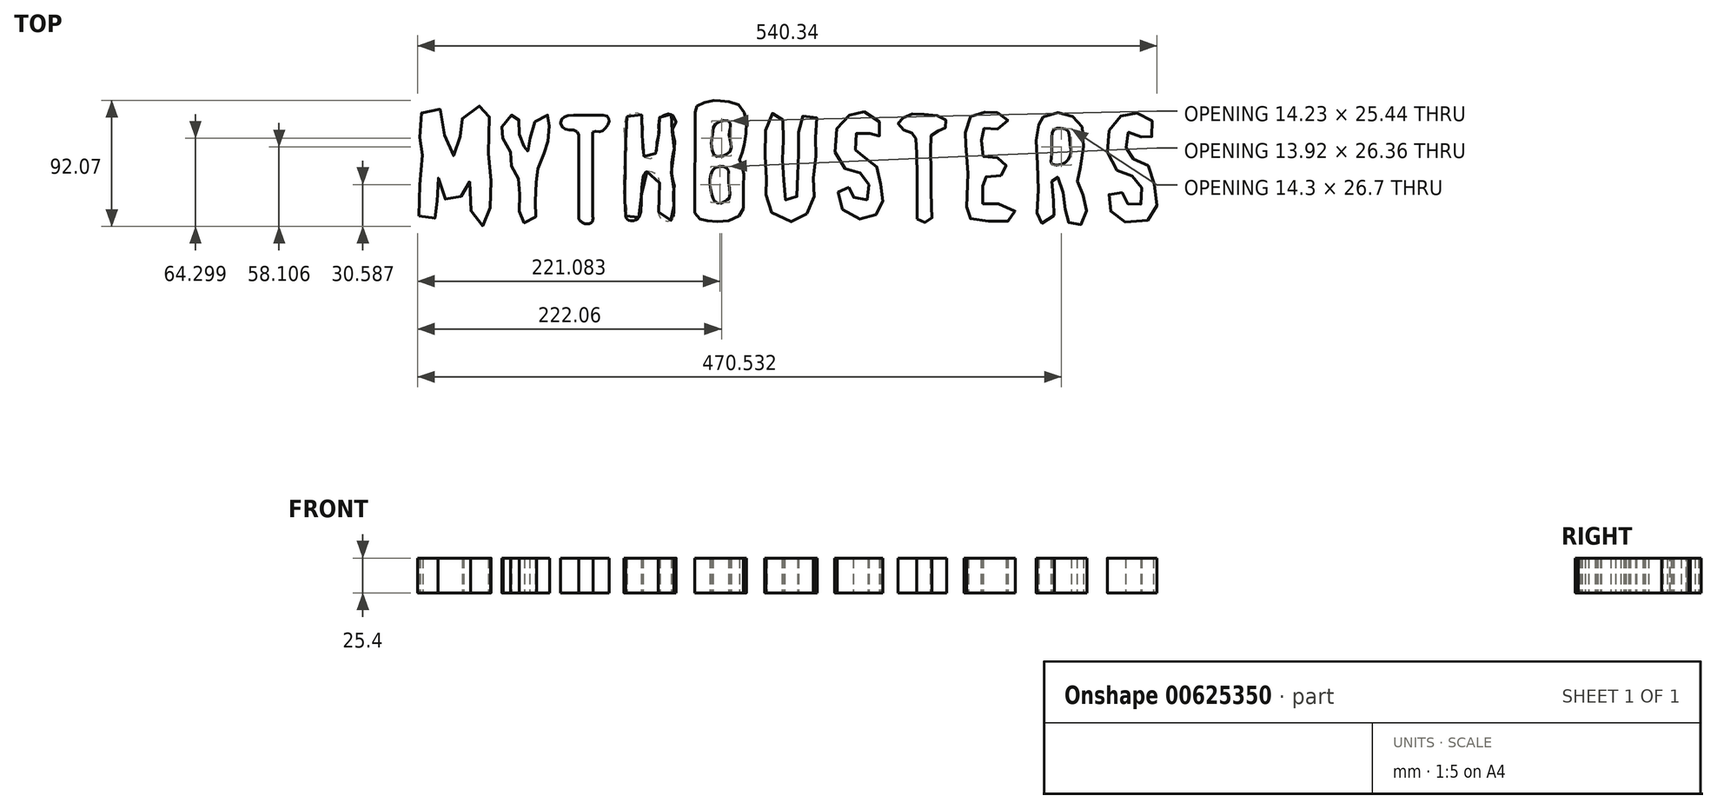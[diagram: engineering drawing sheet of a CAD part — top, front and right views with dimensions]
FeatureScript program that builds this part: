
annotation { "Feature Type Name" : "Feature", "Feature Type Description" : "" }
export const myFeature = defineFeature(function(context is Context, id is Id, definition is map)
    precondition{}
    {
        {
            var Q0;
            Q0=qCreatedBy(makeId("Top.planeOp"),FACE);
            var sketch = newSketch(context, id + "F0", { "sketchPlane" : qUnion([Q0])});
            skLineSegment(sketch, "E0", {"start": v(761.55, 2.5) * mm, "end": v(761.54, 2.5) * mm});
            skLineSegment(sketch, "E1", {"start": v(1000.17, -167.15) * mm, "end": v(1000.17, -167.15) * mm});
            skLineSegment(sketch, "E2", {"start": v(-212, -166.06) * mm, "end": v(-212, -166.06) * mm});
            skLineSegment(sketch, "E3", {"start": v(376.94, -160.6) * mm, "end": v(376.95, -160.6) * mm});
            skLineSegment(sketch, "E4", {"start": v(-451.88, -160.28) * mm, "end": v(-451.87, -160.28) * mm});
            skLineSegment(sketch, "E5", {"start": v(-22.25, -160.22) * mm, "end": v(-22.27, -160.22) * mm});
            skLineSegment(sketch, "E6", {"start": v(526.87, -156.12) * mm, "end": v(526.87, -156.12) * mm});
            skLineSegment(sketch, "E7", {"start": v(199.4, -158.96) * mm, "end": v(199.41, -158.96) * mm});
            skFitSpline(sketch, "E8", {"points": [v(827.87, -177.74) * mm, v(826.62, -176.42) * mm, v(824.58, -175.4) * mm, v(823.21, -175.4) * mm]});
            skFitSpline(sketch, "E9", {"points": [v(823.21, -175.4) * mm, v(821.38, -175.4) * mm, v(818.7, -173.24) * mm, v(812.38, -166.66) * mm]});
            skFitSpline(sketch, "E10", {"points": [v(812.38, -166.66) * mm, v(803.98, -157.92) * mm, v(803.98, -157.92) * mm, v(804.24, -147.06) * mm]});
            skFitSpline(sketch, "E11", {"points": [v(804.24, -147.06) * mm, v(804.47, -137.46) * mm, v(804.26, -135.72) * mm, v(802.42, -132.01) * mm]});
            skFitSpline(sketch, "E12", {"points": [v(802.42, -132.01) * mm, v(800.86, -128.86) * mm, v(800.35, -126.13) * mm, v(800.35, -121.02) * mm]});
            skFitSpline(sketch, "E13", {"points": [v(800.35, -121.02) * mm, v(800.35, -114.24) * mm, v(799.45, -111) * mm, v(796.32, -106.38) * mm]});
            skFitSpline(sketch, "E14", {"points": [v(796.32, -106.38) * mm, v(794.93, -104.33) * mm, v(794.84, -103.44) * mm, v(795.75, -100.82) * mm]});
            skFitSpline(sketch, "E15", {"points": [v(795.75, -100.82) * mm, v(796.71, -98.07) * mm, v(796.61, -97.52) * mm, v(794.93, -96.18) * mm]});
            skFitSpline(sketch, "E16", {"points": [v(794.93, -96.18) * mm, v(792.74, -94.43) * mm, v(791.1, -84.36) * mm, v(792.83, -83.3) * mm]});
            skFitSpline(sketch, "E17", {"points": [v(792.83, -83.3) * mm, v(793.5, -82.88) * mm, v(793.42, -82.2) * mm, v(792.6, -81.2) * mm]});
            skFitSpline(sketch, "E18", {"points": [v(792.6, -81.2) * mm, v(791.79, -80.22) * mm, v(791.36, -76.66) * mm, v(791.34, -70.66) * mm]});
            skFitSpline(sketch, "E19", {"points": [v(791.34, -70.66) * mm, v(791.32, -62.64) * mm, v(791.06, -61.25) * mm, v(789.09, -58.59) * mm]});
            skFitSpline(sketch, "E20", {"points": [v(789.09, -58.59) * mm, v(787.36, -56.25) * mm, v(786.98, -54.83) * mm, v(787.4, -52.24) * mm]});
            skFitSpline(sketch, "E21", {"points": [v(787.4, -52.24) * mm, v(787.91, -49.08) * mm, v(787.53, -48.46) * mm, v(780.65, -41.32) * mm]});
            skFitSpline(sketch, "E22", {"points": [v(780.65, -41.32) * mm, v(772.46, -32.82) * mm, v(772.52, -32.85) * mm, v(769.96, -36.1) * mm]});
            skFitSpline(sketch, "E23", {"points": [v(769.96, -36.1) * mm, v(768.72, -37.67) * mm, v(767.16, -38.46) * mm, v(765.3, -38.46) * mm]});
            skFitSpline(sketch, "E24", {"points": [v(765.3, -38.46) * mm, v(762.5, -38.46) * mm, v(762.5, -38.46) * mm, v(763.12, -45.42) * mm]});
            skFitSpline(sketch, "E25", {"points": [v(763.12, -45.42) * mm, v(763.56, -50.23) * mm, v(763.42, -52.58) * mm, v(762.67, -53.04) * mm]});
            skFitSpline(sketch, "E26", {"points": [v(762.67, -53.04) * mm, v(762.08, -53.4) * mm, v(761.86, -54.13) * mm, v(762.18, -54.64) * mm]});
            skFitSpline(sketch, "E27", {"points": [v(762.18, -54.64) * mm, v(763.28, -56.42) * mm, v(763.7, -92.06) * mm, v(762.63, -92.73) * mm]});
            skFitSpline(sketch, "E28", {"points": [v(762.63, -92.73) * mm, v(761.23, -93.6) * mm, v(761.37, -99.6) * mm, v(762.8, -100.09) * mm]});
            skFitSpline(sketch, "E29", {"points": [v(762.8, -100.09) * mm, v(763.73, -100.4) * mm, v(763.7, -100.82) * mm, v(762.7, -102.04) * mm]});
            skFitSpline(sketch, "E30", {"points": [v(762.7, -102.04) * mm, v(761, -104.1) * mm, v(761.91, -106.23) * mm, v(764.64, -106.62) * mm]});
            skFitSpline(sketch, "E31", {"points": [v(764.64, -106.62) * mm, v(766.75, -106.92) * mm, v(766.83, -107.25) * mm, v(767.02, -117.32) * mm]});
            skFitSpline(sketch, "E32", {"points": [v(767.02, -117.32) * mm, v(767.5, -143.53) * mm, v(767.34, -146.47) * mm, v(765.28, -148.22) * mm]});
            skFitSpline(sketch, "E33", {"points": [v(765.28, -148.22) * mm, v(764.22, -149.12) * mm, v(763.23, -150.95) * mm, v(763.09, -152.28) * mm]});
            skFitSpline(sketch, "E34", {"points": [v(763.09, -152.28) * mm, v(762.94, -153.61) * mm, v(761.92, -155.67) * mm, v(760.8, -156.85) * mm]});
            skFitSpline(sketch, "E35", {"points": [v(760.8, -156.85) * mm, v(759.7, -158.03) * mm, v(758.8, -159.92) * mm, v(758.8, -161.05) * mm]});
            skFitSpline(sketch, "E36", {"points": [v(758.8, -161.05) * mm, v(758.8, -162.22) * mm, v(757.07, -164.84) * mm, v(754.83, -167.08) * mm]});
            skFitSpline(sketch, "E37", {"points": [v(754.83, -167.08) * mm, v(750.86, -171.05) * mm, v(750.86, -171.05) * mm, v(739.06, -170.78) * mm]});
            skFitSpline(sketch, "E38", {"points": [v(739.06, -170.78) * mm, v(725.94, -170.49) * mm, v(724.88, -170) * mm, v(724.83, -164.25) * mm]});
            skFitSpline(sketch, "E39", {"points": [v(722.48, -159) * mm, v(720.17, -156.85) * mm, v(720.17, -156.85) * mm, v(720.1, -124.77) * mm]});
            skFitSpline(sketch, "E40", {"points": [v(720.1, -124.77) * mm, v(720.06, -102.89) * mm, v(720.37, -91.7) * mm, v(721.12, -89.58) * mm]});
            skFitSpline(sketch, "E41", {"points": [v(721.12, -89.58) * mm, v(721.96, -87.17) * mm, v(721.93, -85.97) * mm, v(721, -84.23) * mm]});
            skFitSpline(sketch, "E42", {"points": [v(721, -84.23) * mm, v(720.13, -82.6) * mm, v(719.99, -79.7) * mm, v(720.47, -73.68) * mm]});
            skFitSpline(sketch, "E43", {"points": [v(720.47, -73.68) * mm, v(720.83, -69.11) * mm, v(721.07, -64.63) * mm, v(720.99, -63.72) * mm]});
            skFitSpline(sketch, "E44", {"points": [v(720.99, -63.72) * mm, v(720.79, -61.46) * mm, v(720.59, -47.14) * mm, v(720.7, -43.66) * mm]});
            skFitSpline(sketch, "E45", {"points": [v(720.7, -43.66) * mm, v(720.75, -42.1) * mm, v(720.64, -26.59) * mm, v(720.44, -9.19) * mm]});
            skFitSpline(sketch, "E46", {"points": [v(720.44, -9.19) * mm, v(720.2, 12.32) * mm, v(720.42, 23.73) * mm, v(721.14, 26.46) * mm]});
            skFitSpline(sketch, "E47", {"points": [v(721.14, 26.46) * mm, v(721.86, 29.17) * mm, v(721.9, 30.85) * mm, v(721.25, 31.65) * mm]});
            skFitSpline(sketch, "E48", {"points": [v(721.25, 31.65) * mm, v(719.99, 33.22) * mm, v(719.67, 63.32) * mm, v(720.9, 64.8) * mm]});
            skFitSpline(sketch, "E49", {"points": [v(720.9, 64.8) * mm, v(721.5, 65.54) * mm, v(721.5, 67.46) * mm, v(720.87, 70.4) * mm]});
            skFitSpline(sketch, "E50", {"points": [v(720.87, 70.4) * mm, v(720.35, 72.87) * mm, v(720.16, 77.75) * mm, v(720.46, 81.25) * mm]});
            skFitSpline(sketch, "E51", {"points": [v(720.46, 81.25) * mm, v(721.35, 91.73) * mm, v(721.53, 98.62) * mm, v(720.92, 99) * mm]});
            skFitSpline(sketch, "E52", {"points": [v(720.92, 99) * mm, v(719.9, 99.64) * mm, v(719.98, 111.86) * mm, v(721.02, 113.11) * mm]});
            skFitSpline(sketch, "E53", {"points": [v(721.02, 113.11) * mm, v(721.75, 113.99) * mm, v(721.73, 115.57) * mm, v(720.96, 118.67) * mm]});
            skFitSpline(sketch, "E54", {"points": [v(720.96, 118.67) * mm, v(718.65, 127.82) * mm, v(722.57, 135.65) * mm, v(728.65, 134.06) * mm]});
            skFitSpline(sketch, "E55", {"points": [v(728.65, 134.06) * mm, v(729.6, 133.82) * mm, v(731.76, 134.63) * mm, v(733.44, 135.87) * mm]});
            skFitSpline(sketch, "E56", {"points": [v(733.44, 135.87) * mm, v(735.13, 137.12) * mm, v(737.68, 138.13) * mm, v(739.12, 138.13) * mm]});
            skFitSpline(sketch, "E57", {"points": [v(739.12, 138.13) * mm, v(740.74, 138.13) * mm, v(742.11, 138.83) * mm, v(742.72, 139.96) * mm]});
            skFitSpline(sketch, "E58", {"points": [v(742.72, 139.96) * mm, v(743.97, 142.3) * mm, v(746.9, 143.22) * mm, v(749.2, 142) * mm]});
            skFitSpline(sketch, "E59", {"points": [v(749.2, 142) * mm, v(750.57, 141.26) * mm, v(751.97, 141.49) * mm, v(754.86, 142.88) * mm]});
            skFitSpline(sketch, "E60", {"points": [v(754.86, 142.88) * mm, v(756.98, 143.9) * mm, v(759.1, 144.74) * mm, v(759.59, 144.74) * mm]});
            skFitSpline(sketch, "E61", {"points": [v(759.59, 144.74) * mm, v(760.07, 144.74) * mm, v(761, 145.38) * mm, v(761.64, 146.16) * mm]});
            skFitSpline(sketch, "E62", {"points": [v(761.64, 146.16) * mm, v(763.89, 148.87) * mm, v(776, 148.08) * mm, v(779.68, 145) * mm]});
            skFitSpline(sketch, "E63", {"points": [v(779.68, 145) * mm, v(782.74, 142.4) * mm, v(782.76, 142.4) * mm, v(795.72, 142.72) * mm]});
            skFitSpline(sketch, "E64", {"points": [v(795.72, 142.72) * mm, v(808.7, 143.04) * mm, v(808.7, 143.04) * mm, v(810.3, 140.59) * mm]});
            skFitSpline(sketch, "E65", {"points": [v(810.3, 140.59) * mm, v(811.79, 138.31) * mm, v(812.42, 138.13) * mm, v(818.86, 138.13) * mm]});
            skFitSpline(sketch, "E66", {"points": [v(818.86, 138.13) * mm, v(825.8, 138.13) * mm, v(825.8, 138.13) * mm, v(833.47, 130.34) * mm]});
            skFitSpline(sketch, "E67", {"points": [v(833.47, 130.34) * mm, v(841.9, 121.76) * mm, v(842.82, 120.2) * mm, v(842.15, 115.72) * mm]});
            skFitSpline(sketch, "E68", {"points": [v(842.15, 115.72) * mm, v(841.76, 113.07) * mm, v(842.1, 112.44) * mm, v(844.63, 111) * mm]});
            skFitSpline(sketch, "E69", {"points": [v(844.63, 111) * mm, v(847.48, 109.38) * mm, v(848.37, 107.57) * mm, v(846.8, 106.6) * mm]});
            skFitSpline(sketch, "E70", {"points": [v(846.8, 106.6) * mm, v(845.39, 105.73) * mm, v(847.8, 93.37) * mm, v(849.64, 92.04) * mm]});
            skFitSpline(sketch, "E71", {"points": [v(849.64, 92.04) * mm, v(851.69, 90.57) * mm, v(851.98, 83.8) * mm, v(850.2, 78.9) * mm]});
            skFitSpline(sketch, "E72", {"points": [v(850.2, 78.9) * mm, v(849.3, 76.41) * mm, v(849.3, 75.33) * mm, v(850.2, 73.9) * mm]});
            skFitSpline(sketch, "E73", {"points": [v(850.2, 73.9) * mm, v(851.67, 71.54) * mm, v(851.68, 65.04) * mm, v(850.21, 60.99) * mm]});
            skFitSpline(sketch, "E74", {"points": [v(850.21, 60.99) * mm, v(849.32, 58.52) * mm, v(849.33, 56.9) * mm, v(850.23, 53.5) * mm]});
            skFitSpline(sketch, "E75", {"points": [v(850.23, 53.5) * mm, v(851.11, 50.2) * mm, v(851.13, 48.83) * mm, v(850.3, 47.83) * mm]});
            skFitSpline(sketch, "E76", {"points": [v(850.3, 47.83) * mm, v(849.48, 46.84) * mm, v(849.47, 45.52) * mm, v(850.28, 42.5) * mm]});
            skFitSpline(sketch, "E77", {"points": [v(850.28, 42.5) * mm, v(850.99, 39.89) * mm, v(851.27, 30.32) * mm, v(851.11, 14.85) * mm]});
            skFitSpline(sketch, "E78", {"points": [v(851.11, 14.85) * mm, v(850.87, -8.8) * mm, v(850.87, -8.8) * mm, v(846.38, -13.16) * mm]});
            skFitSpline(sketch, "E79", {"points": [v(846.38, -13.16) * mm, v(843.38, -16.08) * mm, v(841.9, -18.3) * mm, v(841.9, -19.89) * mm]});
            skFitSpline(sketch, "E80", {"points": [v(841.9, -19.89) * mm, v(841.9, -21.41) * mm, v(840.46, -23.7) * mm, v(837.88, -26.31) * mm]});
            skFitSpline(sketch, "E81", {"points": [v(837.88, -26.31) * mm, v(833.87, -30.37) * mm, v(833.87, -30.37) * mm, v(833.7, -38.9) * mm]});
            skFitSpline(sketch, "E82", {"points": [v(833.7, -38.9) * mm, v(833.62, -43.6) * mm, v(833.24, -48.78) * mm, v(832.9, -50.43) * mm]});
            skFitSpline(sketch, "E83", {"points": [v(832.9, -50.43) * mm, v(832.3, -53.2) * mm, v(832.46, -53.45) * mm, v(834.95, -53.74) * mm]});
            skFitSpline(sketch, "E84", {"points": [v(834.95, -53.74) * mm, v(837.5, -54.03) * mm, v(837.66, -54.32) * mm, v(837.94, -59.17) * mm]});
            skFitSpline(sketch, "E85", {"points": [v(837.94, -59.17) * mm, v(838.15, -62.94) * mm, v(838.84, -65.02) * mm, v(840.53, -67.03) * mm]});
            skFitSpline(sketch, "E86", {"points": [v(840.53, -67.03) * mm, v(843.33, -70.36) * mm, v(843.43, -71.54) * mm, v(840.95, -72.19) * mm]});
            skFitSpline(sketch, "E87", {"points": [v(840.95, -72.19) * mm, v(838.02, -72.95) * mm, v(838.69, -74.96) * mm, v(843.35, -79.44) * mm]});
            skFitSpline(sketch, "E88", {"points": [v(843.35, -79.44) * mm, v(847.65, -83.55) * mm, v(847.65, -83.55) * mm, v(847.41, -90.27) * mm]});
            skFitSpline(sketch, "E89", {"points": [v(847.41, -90.27) * mm, v(847.21, -96.15) * mm, v(847.44, -97.24) * mm, v(849.26, -98.93) * mm]});
            skFitSpline(sketch, "E90", {"points": [v(849.26, -98.93) * mm, v(851.84, -101.33) * mm, v(852.33, -110.86) * mm, v(849.92, -111.78) * mm]});
            skFitSpline(sketch, "E91", {"points": [v(849.92, -111.78) * mm, v(847.52, -112.7) * mm, v(848.35, -115.82) * mm, v(851.81, -118.86) * mm]});
            skFitSpline(sketch, "E92", {"points": [v(851.81, -118.86) * mm, v(855.15, -121.8) * mm, v(855.93, -124.15) * mm, v(854.14, -125.94) * mm]});
            skFitSpline(sketch, "E93", {"points": [v(854.14, -125.94) * mm, v(853.07, -127.01) * mm, v(853.87, -130.07) * mm, v(855.22, -130.07) * mm]});
            skFitSpline(sketch, "E94", {"points": [v(855.22, -130.07) * mm, v(855.68, -130.07) * mm, v(856.06, -130.5) * mm, v(856.06, -131) * mm]});
            skFitSpline(sketch, "E95", {"points": [v(856.06, -131) * mm, v(856.06, -131.53) * mm, v(856.93, -132.82) * mm, v(857.98, -133.87) * mm]});
            skFitSpline(sketch, "E96", {"points": [v(857.98, -133.87) * mm, v(859.73, -135.63) * mm, v(859.89, -136.87) * mm, v(859.75, -147.98) * mm]});
            skFitSpline(sketch, "E97", {"points": [v(859.75, -147.98) * mm, v(859.6, -160.08) * mm, v(859.57, -160.19) * mm, v(856.88, -162.76) * mm]});
            skFitSpline(sketch, "E98", {"points": [v(856.88, -162.76) * mm, v(855.4, -164.2) * mm, v(854.17, -166.13) * mm, v(854.17, -167.07) * mm]});
            skFitSpline(sketch, "E99", {"points": [v(854.17, -167.07) * mm, v(854.17, -168.21) * mm, v(853.46, -168.79) * mm, v(852.05, -168.8) * mm]});
            skFitSpline(sketch, "E100", {"points": [v(852.05, -168.8) * mm, v(849.52, -168.82) * mm, v(848.4, -169.55) * mm, v(846.99, -172.09) * mm]});
            skFitSpline(sketch, "E101", {"points": [v(846.99, -172.09) * mm, v(846.41, -173.13) * mm, v(844.43, -174.4) * mm, v(842.58, -174.92) * mm]});
            skFitSpline(sketch, "E102", {"points": [v(842.58, -174.92) * mm, v(840.73, -175.44) * mm, v(838.2, -176.82) * mm, v(836.95, -178) * mm]});
            skFitSpline(sketch, "E103", {"points": [v(836.95, -178) * mm, v(834.01, -180.76) * mm, v(830.64, -180.66) * mm, v(827.87, -177.74) * mm]});
            skFitSpline(sketch, "E104", {"points": [v(761.54, 2.5) * mm, v(759.69, 3.43) * mm, v(759.32, 4.25) * mm, v(759.56, 6.9) * mm]});
            skFitSpline(sketch, "E105", {"points": [v(759.56, 6.9) * mm, v(760.68, 19.3) * mm, v(760.88, 24.3) * mm, v(760.86, 39.2) * mm]});
            skFitSpline(sketch, "E106", {"points": [v(760.86, 39.2) * mm, v(760.85, 49.16) * mm, v(761.21, 56.19) * mm, v(761.76, 56.53) * mm]});
            skFitSpline(sketch, "E107", {"points": [v(761.76, 56.53) * mm, v(762.92, 57.24) * mm, v(764.85, 61.79) * mm, v(764.53, 63.06) * mm]});
            skFitSpline(sketch, "E108", {"points": [v(764.53, 63.06) * mm, v(764.4, 63.58) * mm, v(764.3, 70.7) * mm, v(764.31, 78.88) * mm]});
            skFitSpline(sketch, "E109", {"points": [v(764.31, 78.88) * mm, v(764.33, 93.76) * mm, v(764.33, 93.76) * mm, v(768.14, 97.77) * mm]});
            skFitSpline(sketch, "E110", {"points": [v(768.14, 97.77) * mm, v(771.96, 101.77) * mm, v(771.96, 101.77) * mm, v(785.91, 101.77) * mm]});
            skFitSpline(sketch, "E111", {"points": [v(785.91, 101.77) * mm, v(799.87, 101.77) * mm, v(799.87, 101.77) * mm, v(805.07, 96.84) * mm]});
            skFitSpline(sketch, "E112", {"points": [v(805.07, 96.84) * mm, v(807.92, 94.12) * mm, v(810.58, 91.89) * mm, v(810.97, 91.88) * mm]});
            skFitSpline(sketch, "E113", {"points": [v(810.97, 91.88) * mm, v(812.3, 91.84) * mm, v(811.68, 88.29) * mm, v(810.26, 87.74) * mm]});
            skFitSpline(sketch, "E114", {"points": [v(810.26, 87.74) * mm, v(808.25, 86.97) * mm, v(808.5, 84.07) * mm, v(810.76, 82.14) * mm]});
            skFitSpline(sketch, "E115", {"points": [v(810.76, 82.14) * mm, v(812.4, 80.74) * mm, v(812.6, 79.8) * mm, v(812.06, 75.84) * mm]});
            skFitSpline(sketch, "E116", {"points": [v(812.06, 75.84) * mm, v(811.47, 71.38) * mm, v(811.55, 71.15) * mm, v(813.92, 70.56) * mm]});
            skFitSpline(sketch, "E117", {"points": [v(813.92, 70.56) * mm, v(816.27, 69.97) * mm, v(816.4, 69.62) * mm, v(816.4, 63.94) * mm]});
            skFitSpline(sketch, "E118", {"points": [v(816.4, 63.94) * mm, v(816.4, 59.42) * mm, v(816.03, 57.75) * mm, v(814.87, 57.1) * mm]});
            skFitSpline(sketch, "E119", {"points": [v(815.52, 52.2) * mm, v(816.7, 52.2) * mm, v(816.65, 48.68) * mm, v(815.46, 47.95) * mm]});
            skFitSpline(sketch, "E120", {"points": [v(815.46, 47.95) * mm, v(814.94, 47.63) * mm, v(814.52, 46.54) * mm, v(814.52, 45.53) * mm]});
            skFitSpline(sketch, "E121", {"points": [v(814.52, 45.53) * mm, v(814.52, 44.52) * mm, v(814.94, 43.7) * mm, v(815.46, 43.7) * mm]});
            skFitSpline(sketch, "E122", {"points": [v(815.46, 43.7) * mm, v(815.98, 43.7) * mm, v(816.4, 42.63) * mm, v(816.4, 41.34) * mm]});
            skFitSpline(sketch, "E123", {"points": [v(816.4, 41.34) * mm, v(816.4, 40.04) * mm, v(815.98, 38.98) * mm, v(815.46, 38.98) * mm]});
            skFitSpline(sketch, "E124", {"points": [v(815.46, 38.98) * mm, v(814.94, 38.98) * mm, v(814.52, 38.15) * mm, v(814.52, 37.14) * mm]});
            skFitSpline(sketch, "E125", {"points": [v(814.52, 37.14) * mm, v(814.52, 36.13) * mm, v(814.94, 35.05) * mm, v(815.46, 34.73) * mm]});
            skFitSpline(sketch, "E126", {"points": [v(815.46, 34.73) * mm, v(817.23, 33.63) * mm, v(816.47, 30) * mm, v(814.28, 29.05) * mm]});
            skFitSpline(sketch, "E127", {"points": [v(814.28, 29.05) * mm, v(812.7, 28.35) * mm, v(812.08, 27.18) * mm, v(811.86, 24.47) * mm]});
            skFitSpline(sketch, "E128", {"points": [v(811.86, 24.47) * mm, v(811.64, 21.8) * mm, v(811.06, 20.7) * mm, v(809.73, 20.34) * mm]});
            skFitSpline(sketch, "E129", {"points": [v(809.73, 20.34) * mm, v(808.49, 20.02) * mm, v(807.9, 19.04) * mm, v(807.9, 17.26) * mm]});
            skFitSpline(sketch, "E130", {"points": [v(807.9, 17.26) * mm, v(807.9, 14.42) * mm, v(803.9, 10.5) * mm, v(795.06, 4.68) * mm]});
            skFitSpline(sketch, "E131", {"points": [v(795.06, 4.68) * mm, v(790.23, 1.51) * mm, v(790.23, 1.51) * mm, v(777.03, 1.43) * mm]});
            skFitSpline(sketch, "E132", {"points": [v(777.03, 1.43) * mm, v(768.4, 1.38) * mm, v(763.04, 1.74) * mm, v(761.55, 2.5) * mm]});
            skFitSpline(sketch, "E133", {"points": [v(-892.4, -175.43) * mm, v(-892.77, -174.83) * mm, v(-893.99, -173.94) * mm, v(-895.1, -173.45) * mm]});
            skFitSpline(sketch, "E134", {"points": [v(-895.1, -173.45) * mm, v(-896.22, -172.96) * mm, v(-897.78, -172.2) * mm, v(-898.56, -171.77) * mm]});
            skFitSpline(sketch, "E135", {"points": [v(-898.56, -171.77) * mm, v(-899.33, -171.33) * mm, v(-900.82, -170.54) * mm, v(-901.86, -170.02) * mm]});
            skFitSpline(sketch, "E136", {"points": [v(-901.86, -170.02) * mm, v(-903.32, -169.28) * mm, v(-903.82, -167.94) * mm, v(-904.04, -164.17) * mm]});
            skFitSpline(sketch, "E137", {"points": [v(-904.04, -164.17) * mm, v(-904.23, -160.84) * mm, v(-905.09, -158.15) * mm, v(-906.7, -155.77) * mm]});
            skFitSpline(sketch, "E138", {"points": [v(-906.7, -155.77) * mm, v(-908.68, -152.86) * mm, v(-909, -151.53) * mm, v(-908.56, -148) * mm]});
            skFitSpline(sketch, "E139", {"points": [v(-908.56, -148) * mm, v(-907.5, -139.55) * mm, v(-907.9, -137.31) * mm, v(-910.86, -134.5) * mm]});
            skFitSpline(sketch, "E140", {"points": [v(-910.86, -134.5) * mm, v(-913.95, -131.59) * mm, v(-914.2, -130.27) * mm, v(-912.54, -125.68) * mm]});
            skFitSpline(sketch, "E141", {"points": [v(-912.54, -125.68) * mm, v(-911.66, -123.25) * mm, v(-911.68, -122.1) * mm, v(-912.61, -120.35) * mm]});
            skFitSpline(sketch, "E142", {"points": [v(-912.61, -120.35) * mm, v(-913.84, -118.05) * mm, v(-913.6, -84.08) * mm, v(-912.33, -82.04) * mm]});
            skFitSpline(sketch, "E143", {"points": [v(-912.33, -82.04) * mm, v(-912, -81.52) * mm, v(-912.18, -80.82) * mm, v(-912.7, -80.5) * mm]});
            skFitSpline(sketch, "E144", {"points": [v(-912.7, -80.5) * mm, v(-913.23, -80.17) * mm, v(-913.66, -76.33) * mm, v(-913.66, -71.96) * mm]});
            skFitSpline(sketch, "E145", {"points": [v(-913.66, -71.96) * mm, v(-913.66, -64.82) * mm, v(-913.87, -63.92) * mm, v(-915.69, -62.94) * mm]});
            skFitSpline(sketch, "E146", {"points": [v(-915.69, -62.94) * mm, v(-917.62, -61.91) * mm, v(-917.68, -61.41) * mm, v(-917.12, -52.29) * mm]});
            skFitSpline(sketch, "E147", {"points": [v(-917.12, -52.29) * mm, v(-916.53, -42.71) * mm, v(-916.53, -42.71) * mm, v(-918.64, -45.54) * mm]});
            skFitSpline(sketch, "E148", {"points": [v(-918.64, -45.54) * mm, v(-919.8, -47.1) * mm, v(-921.47, -49.09) * mm, v(-922.35, -49.97) * mm]});
            skFitSpline(sketch, "E149", {"points": [v(-922.35, -49.97) * mm, v(-923.23, -50.85) * mm, v(-924.16, -53.4) * mm, v(-924.41, -55.64) * mm]});
            skFitSpline(sketch, "E150", {"points": [v(-924.41, -55.64) * mm, v(-924.67, -57.88) * mm, v(-924.9, -59.82) * mm, v(-924.94, -59.95) * mm]});
            skFitSpline(sketch, "E151", {"points": [v(-924.94, -59.95) * mm, v(-924.97, -60.08) * mm, v(-925.59, -60.18) * mm, v(-926.31, -60.18) * mm]});
            skFitSpline(sketch, "E152", {"points": [v(-926.31, -60.18) * mm, v(-928.15, -60.18) * mm, v(-928.71, -62.15) * mm, v(-928.12, -66.54) * mm]});
            skFitSpline(sketch, "E153", {"points": [v(-928.12, -66.54) * mm, v(-927.67, -69.92) * mm, v(-927.9, -70.5) * mm, v(-930.56, -72.38) * mm]});
            skFitSpline(sketch, "E154", {"points": [v(-930.56, -72.38) * mm, v(-932.8, -73.98) * mm, v(-933.5, -75.2) * mm, v(-933.5, -77.5) * mm]});
            skFitSpline(sketch, "E155", {"points": [v(-933.5, -77.5) * mm, v(-933.5, -79.43) * mm, v(-934.14, -80.9) * mm, v(-935.3, -81.63) * mm]});
            skFitSpline(sketch, "E156", {"points": [v(-935.3, -81.63) * mm, v(-937.57, -83.05) * mm, v(-939.93, -89.67) * mm, v(-938.35, -90.2) * mm]});
            skFitSpline(sketch, "E157", {"points": [v(-938.35, -90.2) * mm, v(-934.38, -91.52) * mm, v(-939.2, -97.03) * mm, v(-944.16, -96.84) * mm]});
            skFitSpline(sketch, "E158", {"points": [v(-944.16, -96.84) * mm, v(-946.25, -96.76) * mm, v(-948.35, -97.34) * mm, v(-949.38, -98.28) * mm]});
            skFitSpline(sketch, "E159", {"points": [v(-949.38, -98.28) * mm, v(-950.77, -99.53) * mm, v(-953.12, -99.85) * mm, v(-961.16, -99.85) * mm]});
            skFitSpline(sketch, "E160", {"points": [v(-961.16, -99.85) * mm, v(-971.05, -99.85) * mm, v(-971.25, -99.89) * mm, v(-974.1, -102.68) * mm]});
            skFitSpline(sketch, "E161", {"points": [v(-974.1, -102.68) * mm, v(-977.96, -106.45) * mm, v(-978.77, -106.3) * mm, v(-984.4, -100.79) * mm]});
            skFitSpline(sketch, "E162", {"points": [v(-984.4, -100.79) * mm, v(-987.05, -98.2) * mm, v(-989.57, -96.07) * mm, v(-990, -96.07) * mm]});
            skFitSpline(sketch, "E163", {"points": [v(-990, -96.07) * mm, v(-990.43, -96.07) * mm, v(-991.24, -95.11) * mm, v(-991.8, -93.94) * mm]});
            skFitSpline(sketch, "E164", {"points": [v(-991.8, -93.94) * mm, v(-996.27, -84.63) * mm, v(-996.77, -82.9) * mm, v(-996.77, -76.81) * mm]});
            skFitSpline(sketch, "E165", {"points": [v(-996.77, -76.81) * mm, v(-996.77, -70.98) * mm, v(-997.01, -70.18) * mm, v(-999.6, -67.6) * mm]});
            skFitSpline(sketch, "E166", {"points": [v(-999.6, -67.6) * mm, v(-1001.16, -66.03) * mm, v(-1002.43, -63.87) * mm, v(-1002.43, -62.78) * mm]});
            skFitSpline(sketch, "E167", {"points": [v(-1002.43, -62.78) * mm, v(-1002.43, -61.7) * mm, v(-1003.02, -60.13) * mm, v(-1003.75, -59.31) * mm]});
            skFitSpline(sketch, "E168", {"points": [v(-1003.75, -59.31) * mm, v(-1005.84, -56.93) * mm, v(-1006.52, -52.12) * mm, v(-1004.97, -50.58) * mm]});
            skFitSpline(sketch, "E169", {"points": [v(-1004.97, -50.58) * mm, v(-1003.47, -49.08) * mm, v(-1004.8, -43.16) * mm, v(-1006.78, -42.51) * mm]});
            skFitSpline(sketch, "E170", {"points": [v(-1006.78, -42.51) * mm, v(-1008.16, -42.06) * mm, v(-1009.29, -64.8) * mm, v(-1008.36, -74.35) * mm]});
            skFitSpline(sketch, "E171", {"points": [v(-1008.36, -74.35) * mm, v(-1007.47, -83.4) * mm, v(-1007.82, -106.56) * mm, v(-1008.86, -107.6) * mm]});
            skFitSpline(sketch, "E172", {"points": [v(-1008.86, -107.6) * mm, v(-1009.3, -108.02) * mm, v(-1009.33, -110.6) * mm, v(-1008.94, -113.32) * mm]});
            skFitSpline(sketch, "E173", {"points": [v(-1008.94, -113.32) * mm, v(-1007.48, -123.56) * mm, v(-1007.88, -127.37) * mm, v(-1010.7, -130.32) * mm]});
            skFitSpline(sketch, "E174", {"points": [v(-1010.7, -130.32) * mm, v(-1013.27, -133) * mm, v(-1013.3, -133.16) * mm, v(-1013, -143.83) * mm]});
            skFitSpline(sketch, "E175", {"points": [v(-1013, -143.83) * mm, v(-1012.7, -154.63) * mm, v(-1012.7, -154.63) * mm, v(-1020.08, -162.55) * mm]});
            skFitSpline(sketch, "E176", {"points": [v(-1020.08, -162.55) * mm, v(-1027.5, -170.5) * mm, v(-1030.73, -172.25) * mm, v(-1032.43, -169.22) * mm]});
            skFitSpline(sketch, "E177", {"points": [v(-1032.43, -169.22) * mm, v(-1033.1, -168.01) * mm, v(-1033.46, -168.17) * mm, v(-1034.52, -170.16) * mm]});
            skFitSpline(sketch, "E178", {"points": [v(-1034.52, -170.16) * mm, v(-1035.23, -171.48) * mm, v(-1036.4, -172.56) * mm, v(-1037.13, -172.56) * mm]});
            skFitSpline(sketch, "E179", {"points": [v(-1037.13, -172.56) * mm, v(-1037.86, -172.56) * mm, v(-1039.1, -173.2) * mm, v(-1039.87, -173.98) * mm]});
            skFitSpline(sketch, "E180", {"points": [v(-1039.87, -173.98) * mm, v(-1041.79, -175.9) * mm, v(-1044.85, -175.77) * mm, v(-1045.62, -173.74) * mm]});
            skFitSpline(sketch, "E181", {"points": [v(-1045.62, -173.74) * mm, v(-1046.52, -171.4) * mm, v(-1049.5, -168.97) * mm, v(-1054.13, -166.8) * mm]});
            skFitSpline(sketch, "E182", {"points": [v(-1054.13, -166.8) * mm, v(-1056.97, -165.47) * mm, v(-1058.31, -164.18) * mm, v(-1058.74, -162.37) * mm]});
            skFitSpline(sketch, "E183", {"points": [v(-1058.74, -162.37) * mm, v(-1059.07, -160.96) * mm, v(-1060.35, -158.46) * mm, v(-1061.58, -156.8) * mm]});
            skFitSpline(sketch, "E184", {"points": [v(-1061.58, -156.8) * mm, v(-1063.8, -153.82) * mm, v(-1063.82, -153.6) * mm, v(-1063.82, -129.24) * mm]});
            skFitSpline(sketch, "E185", {"points": [v(-1063.82, -129.24) * mm, v(-1063.82, -115.19) * mm, v(-1063.44, -104.45) * mm, v(-1062.94, -104.14) * mm]});
            skFitSpline(sketch, "E186", {"points": [v(-1062.94, -104.14) * mm, v(-1062.4, -103.8) * mm, v(-1062.4, -102.42) * mm, v(-1062.94, -100.55) * mm]});
            skFitSpline(sketch, "E187", {"points": [v(-1062.94, -100.55) * mm, v(-1063.42, -98.87) * mm, v(-1063.82, -90.24) * mm, v(-1063.82, -81.37) * mm]});
            skFitSpline(sketch, "E188", {"points": [v(-1063.82, -81.37) * mm, v(-1063.82, -65.28) * mm, v(-1063.81, -65.23) * mm, v(-1061.4, -62.97) * mm]});
            skFitSpline(sketch, "E189", {"points": [v(-1061.4, -62.97) * mm, v(-1060.08, -61.72) * mm, v(-1059.17, -60) * mm, v(-1059.4, -59.16) * mm]});
            skFitSpline(sketch, "E190", {"points": [v(-1059.4, -59.16) * mm, v(-1059.61, -58.31) * mm, v(-1059.4, -56.9) * mm, v(-1058.91, -56.04) * mm]});
            skFitSpline(sketch, "E191", {"points": [v(-1058.91, -56.04) * mm, v(-1058.35, -55.03) * mm, v(-1058.44, -52.6) * mm, v(-1059.19, -49.28) * mm]});
            skFitSpline(sketch, "E192", {"points": [v(-1059.19, -49.28) * mm, v(-1060.12, -45.11) * mm, v(-1060.1, -43.66) * mm, v(-1059.12, -41.82) * mm]});
            skFitSpline(sketch, "E193", {"points": [v(-1059.12, -41.82) * mm, v(-1058.45, -40.56) * mm, v(-1058.2, -38.76) * mm, v(-1058.58, -37.82) * mm]});
            skFitSpline(sketch, "E194", {"points": [v(-1058.58, -37.82) * mm, v(-1060, -34.25) * mm, v(-1060.04, -11.02) * mm, v(-1058.63, -10.48) * mm]});
            skFitSpline(sketch, "E195", {"points": [v(-1058.63, -10.48) * mm, v(-1057.59, -10.08) * mm, v(-1057.54, -9.5) * mm, v(-1058.4, -7.62) * mm]});
            skFitSpline(sketch, "E196", {"points": [v(-1058.38, -3.53) * mm, v(-1057.53, -2.17) * mm, v(-1057.6, -1.55) * mm, v(-1058.67, -0.65) * mm]});
            skFitSpline(sketch, "E197", {"points": [v(-1058.67, -0.65) * mm, v(-1060.32, 0.72) * mm, v(-1060.56, 9.74) * mm, v(-1059, 11.31) * mm]});
            skFitSpline(sketch, "E198", {"points": [v(-1059, 11.31) * mm, v(-1058.23, 12.08) * mm, v(-1058.26, 13.31) * mm, v(-1059.12, 15.9) * mm]});
            skFitSpline(sketch, "E199", {"points": [v(-1059.12, 15.9) * mm, v(-1060.23, 19.28) * mm, v(-1060.17, 19.55) * mm, v(-1057.8, 21.27) * mm]});
            skFitSpline(sketch, "E200", {"points": [v(-1057.8, 21.27) * mm, v(-1055.71, 22.8) * mm, v(-1055.32, 23.8) * mm, v(-1055.32, 27.65) * mm]});
            skFitSpline(sketch, "E201", {"points": [v(-1055.32, 27.65) * mm, v(-1055.32, 30.59) * mm, v(-1054.78, 32.77) * mm, v(-1053.81, 33.74) * mm]});
            skFitSpline(sketch, "E202", {"points": [v(-1053.81, 33.74) * mm, v(-1051.96, 35.6) * mm, v(-1052.73, 38.03) * mm, v(-1055.17, 38.03) * mm]});
            skFitSpline(sketch, "E203", {"points": [v(-1055.17, 38.03) * mm, v(-1056.17, 38.03) * mm, v(-1057.4, 38.56) * mm, v(-1057.91, 39.21) * mm]});
            skFitSpline(sketch, "E204", {"points": [v(-1057.91, 39.21) * mm, v(-1059.15, 40.77) * mm, v(-1060.4, 63.2) * mm, v(-1059.3, 63.88) * mm]});
            skFitSpline(sketch, "E205", {"points": [v(-1059.3, 63.88) * mm, v(-1058.8, 64.18) * mm, v(-1058.76, 66.36) * mm, v(-1059.19, 68.92) * mm]});
            skFitSpline(sketch, "E206", {"points": [v(-1059.19, 68.92) * mm, v(-1060.39, 76.22) * mm, v(-1060.18, 81.12) * mm, v(-1058.62, 82.42) * mm]});
            skFitSpline(sketch, "E207", {"points": [v(-1058.62, 82.42) * mm, v(-1056.72, 84) * mm, v(-1056.83, 87.11) * mm, v(-1058.86, 88.69) * mm]});
            skFitSpline(sketch, "E208", {"points": [v(-1058.86, 88.69) * mm, v(-1060.32, 89.82) * mm, v(-1060.35, 90.1) * mm, v(-1059.09, 91.15) * mm]});
            skFitSpline(sketch, "E209", {"points": [v(-1059.09, 91.15) * mm, v(-1057.61, 92.38) * mm, v(-1057.66, 96.38) * mm, v(-1059.18, 97.95) * mm]});
            skFitSpline(sketch, "E210", {"points": [v(-1059.18, 97.95) * mm, v(-1060.28, 99.1) * mm, v(-1060.31, 111.96) * mm, v(-1059.22, 113.15) * mm]});
            skFitSpline(sketch, "E211", {"points": [v(-1059.22, 113.15) * mm, v(-1057.54, 114.99) * mm, v(-1057.17, 119.03) * mm, v(-1058.63, 119.59) * mm]});
            skFitSpline(sketch, "E212", {"points": [v(-1058.63, 119.59) * mm, v(-1060.43, 120.28) * mm, v(-1060.52, 126.17) * mm, v(-1058.75, 127.64) * mm]});
            skFitSpline(sketch, "E213", {"points": [v(-1058.75, 127.64) * mm, v(-1057.48, 128.7) * mm, v(-1057.56, 129.78) * mm, v(-1059.57, 138.73) * mm]});
            skFitSpline(sketch, "E214", {"points": [v(-1059.57, 138.73) * mm, v(-1060.36, 142.23) * mm, v(-1058.1, 146.37) * mm, v(-1054.95, 147.16) * mm]});
            skFitSpline(sketch, "E215", {"points": [v(-1054.95, 147.16) * mm, v(-1052.9, 147.68) * mm, v(-1048.7, 152.9) * mm, v(-1048.7, 154.95) * mm]});
            skFitSpline(sketch, "E216", {"points": [v(-1047.9, 156.08) * mm, v(-1047.47, 156.08) * mm, v(-1046.13, 156.93) * mm, v(-1044.93, 157.96) * mm]});
            skFitSpline(sketch, "E217", {"points": [v(-1044.93, 157.96) * mm, v(-1043.73, 159) * mm, v(-1042.15, 159.85) * mm, v(-1041.42, 159.85) * mm]});
            skFitSpline(sketch, "E218", {"points": [v(-1041.42, 159.85) * mm, v(-1040.68, 159.85) * mm, v(-1038.55, 161.02) * mm, v(-1036.68, 162.45) * mm]});
            skFitSpline(sketch, "E219", {"points": [v(-1036.68, 162.45) * mm, v(-1033.49, 164.89) * mm, v(-1032.58, 165.07) * mm, v(-1022.1, 165.38) * mm]});
            skFitSpline(sketch, "E220", {"points": [v(-1022.1, 165.38) * mm, v(-1015.35, 165.59) * mm, v(-1010.93, 165.36) * mm, v(-1010.93, 164.8) * mm]});
            skFitSpline(sketch, "E221", {"points": [v(-1010.93, 164.8) * mm, v(-1010.93, 164.31) * mm, v(-1007.32, 160.33) * mm, v(-1002.91, 155.97) * mm]});
            skFitSpline(sketch, "E222", {"points": [v(-1002.91, 155.97) * mm, v(-994.63, 147.8) * mm, v(-993.84, 146.16) * mm, v(-995.96, 141.51) * mm]});
            skFitSpline(sketch, "E223", {"points": [v(-995.96, 141.51) * mm, v(-996.78, 139.7) * mm, v(-996.78, 138.8) * mm, v(-995.94, 137.8) * mm]});
            skFitSpline(sketch, "E224", {"points": [v(-995.94, 137.8) * mm, v(-995.23, 136.94) * mm, v(-995.05, 135.04) * mm, v(-995.45, 132.57) * mm]});
            skFitSpline(sketch, "E225", {"points": [v(-995.45, 132.57) * mm, v(-996, 129.06) * mm, v(-995.88, 128.69) * mm, v(-994.1, 128.69) * mm]});
            skFitSpline(sketch, "E226", {"points": [v(-994.1, 128.69) * mm, v(-990.68, 128.69) * mm, v(-990.16, 125.83) * mm, v(-990.16, 107.1) * mm]});
            skFitSpline(sketch, "E227", {"points": [v(-990.16, 107.1) * mm, v(-990.16, 89.98) * mm, v(-990.07, 89.13) * mm, v(-988.27, 88.55) * mm]});
            skFitSpline(sketch, "E228", {"points": [v(-988.27, 88.55) * mm, v(-986.67, 88.05) * mm, v(-986.38, 87.12) * mm, v(-986.38, 82.53) * mm]});
            skFitSpline(sketch, "E229", {"points": [v(-986.38, 82.53) * mm, v(-986.38, 77.73) * mm, v(-986.05, 76.79) * mm, v(-983.55, 74.39) * mm]});
            skFitSpline(sketch, "E230", {"points": [v(-983.55, 74.39) * mm, v(-980.85, 71.8) * mm, v(-979.65, 67.3) * mm, v(-981.66, 67.3) * mm]});
            skFitSpline(sketch, "E231", {"points": [v(-981.66, 67.3) * mm, v(-982.18, 67.3) * mm, v(-982.6, 66.24) * mm, v(-982.6, 64.94) * mm]});
            skFitSpline(sketch, "E232", {"points": [v(-982.6, 64.94) * mm, v(-982.6, 63.3) * mm, v(-982.09, 62.58) * mm, v(-980.9, 62.58) * mm]});
            skFitSpline(sketch, "E233", {"points": [v(-980.9, 62.58) * mm, v(-976.83, 62.58) * mm, v(-975.67, 58.4) * mm, v(-979.3, 56.75) * mm]});
            skFitSpline(sketch, "E234", {"points": [v(-979.3, 56.75) * mm, v(-981.77, 55.62) * mm, v(-982.78, 51.57) * mm, v(-980.36, 52.5) * mm]});
            skFitSpline(sketch, "E235", {"points": [v(-980.36, 52.5) * mm, v(-978.74, 53.12) * mm, v(-976.94, 51.4) * mm, v(-976.94, 49.24) * mm]});
            skFitSpline(sketch, "E236", {"points": [v(-970.1, 39.62) * mm, v(-967.77, 38.28) * mm, v(-967.5, 37.58) * mm, v(-967.5, 33.1) * mm]});
            skFitSpline(sketch, "E237", {"points": [v(-967.5, 33.1) * mm, v(-967.5, 29.14) * mm, v(-967.07, 27.7) * mm, v(-965.5, 26.36) * mm]});
            skFitSpline(sketch, "E238", {"points": [v(-965.5, 26.36) * mm, v(-963.99, 25.06) * mm, v(-963.65, 24) * mm, v(-964.09, 21.9) * mm]});
            skFitSpline(sketch, "E239", {"points": [v(-964.09, 21.9) * mm, v(-964.4, 20.38) * mm, v(-964.93, 17.87) * mm, v(-965.25, 16.31) * mm]});
            skFitSpline(sketch, "E240", {"points": [v(-965.25, 16.31) * mm, v(-965.87, 13.36) * mm, v(-964.83, 12.75) * mm, v(-961.43, 14.05) * mm]});
            skFitSpline(sketch, "E241", {"points": [v(-961.43, 14.05) * mm, v(-959.76, 14.7) * mm, v(-959.38, 17.25) * mm, v(-960.95, 17.25) * mm]});
            skFitSpline(sketch, "E242", {"points": [v(-960.95, 17.25) * mm, v(-962.8, 17.25) * mm, v(-961.4, 21.49) * mm, v(-959.23, 22.44) * mm]});
            skFitSpline(sketch, "E243", {"points": [v(-959.23, 22.44) * mm, v(-957.3, 23.29) * mm, v(-957.1, 24) * mm, v(-957.1, 30.7) * mm]});
            skFitSpline(sketch, "E244", {"points": [v(-957.1, 30.7) * mm, v(-957.1, 37) * mm, v(-956.84, 38.18) * mm, v(-955.22, 39.2) * mm]});
            skFitSpline(sketch, "E245", {"points": [v(-955.22, 39.2) * mm, v(-954.07, 39.91) * mm, v(-953.33, 41.4) * mm, v(-953.33, 42.99) * mm]});
            skFitSpline(sketch, "E246", {"points": [v(-953.33, 42.99) * mm, v(-953.33, 44.62) * mm, v(-952.24, 46.74) * mm, v(-950.44, 48.63) * mm]});
            skFitSpline(sketch, "E247", {"points": [v(-950.44, 48.63) * mm, v(-948.38, 50.78) * mm, v(-947.72, 52.2) * mm, v(-948.14, 53.58) * mm]});
            skFitSpline(sketch, "E248", {"points": [v(-948.14, 53.58) * mm, v(-950.03, 59.74) * mm, v(-949.57, 62.36) * mm, v(-945.74, 66.99) * mm]});
            skFitSpline(sketch, "E249", {"points": [v(-945.74, 66.99) * mm, v(-941.92, 71.61) * mm, v(-941.26, 73.35) * mm, v(-942.94, 74.39) * mm]});
            skFitSpline(sketch, "E250", {"points": [v(-942.94, 74.39) * mm, v(-943.46, 74.7) * mm, v(-943.89, 77.63) * mm, v(-943.89, 80.88) * mm]});
            skFitSpline(sketch, "E251", {"points": [v(-943.89, 80.88) * mm, v(-943.89, 86.33) * mm, v(-943.67, 86.94) * mm, v(-941.08, 88.86) * mm]});
            skFitSpline(sketch, "E252", {"points": [v(-941.08, 88.86) * mm, v(-938.58, 90.7) * mm, v(-938.39, 91.2) * mm, v(-939.33, 93.26) * mm]});
            skFitSpline(sketch, "E253", {"points": [v(-939.33, 93.26) * mm, v(-940.13, 95.01) * mm, v(-940.1, 95.92) * mm, v(-939.24, 96.96) * mm]});
            skFitSpline(sketch, "E254", {"points": [v(-939.24, 96.96) * mm, v(-938.4, 97.98) * mm, v(-938.36, 98.86) * mm, v(-939.1, 100.24) * mm]});
            skFitSpline(sketch, "E255", {"points": [v(-939.1, 100.24) * mm, v(-940.65, 103.14) * mm, v(-940.39, 103.87) * mm, v(-936.33, 107.8) * mm]});
            skFitSpline(sketch, "E256", {"points": [v(-936.33, 107.8) * mm, v(-932.17, 111.84) * mm, v(-931.28, 116.22) * mm, v(-934.05, 119) * mm]});
            skFitSpline(sketch, "E257", {"points": [v(-934.05, 119) * mm, v(-935.18, 120.12) * mm, v(-935.4, 121.46) * mm, v(-934.93, 124.36) * mm]});
            skFitSpline(sketch, "E258", {"points": [v(-934.93, 124.36) * mm, v(-934.6, 126.48) * mm, v(-934.33, 130.08) * mm, v(-934.34, 132.36) * mm]});
            skFitSpline(sketch, "E259", {"points": [v(-934.34, 132.36) * mm, v(-934.36, 135.09) * mm, v(-933.74, 137.31) * mm, v(-932.52, 138.86) * mm]});
            skFitSpline(sketch, "E260", {"points": [v(-932.52, 138.86) * mm, v(-931.5, 140.16) * mm, v(-930.66, 141.84) * mm, v(-930.66, 142.6) * mm]});
            skFitSpline(sketch, "E261", {"points": [v(-928.78, 146.37) * mm, v(-927.74, 147.7) * mm, v(-926.89, 149.9) * mm, v(-926.89, 151.26) * mm]});
            skFitSpline(sketch, "E262", {"points": [v(-926.89, 151.26) * mm, v(-926.89, 152.63) * mm, v(-925.82, 155.31) * mm, v(-924.53, 157.22) * mm]});
            skFitSpline(sketch, "E263", {"points": [v(-924.53, 157.22) * mm, v(-923.23, 159.13) * mm, v(-922.17, 161.11) * mm, v(-922.17, 161.62) * mm]});
            skFitSpline(sketch, "E264", {"points": [v(-922.17, 161.62) * mm, v(-922.17, 164.13) * mm, v(-919.02, 165.56) * mm, v(-913.87, 165.39) * mm]});
            skFitSpline(sketch, "E265", {"points": [v(-913.87, 165.39) * mm, v(-909.4, 165.24) * mm, v(-908.38, 165.53) * mm, v(-907.24, 167.26) * mm]});
            skFitSpline(sketch, "E266", {"points": [v(-907.24, 167.26) * mm, v(-906, 169.13) * mm, v(-905.07, 169.3) * mm, v(-896.2, 169.3) * mm]});
            skFitSpline(sketch, "E267", {"points": [v(-896.2, 169.3) * mm, v(-887.27, 169.3) * mm, v(-886.4, 169.46) * mm, v(-885.14, 171.37) * mm]});
            skFitSpline(sketch, "E268", {"points": [v(-885.14, 171.37) * mm, v(-884, 173.07) * mm, v(-882.68, 173.5) * mm, v(-877.7, 173.77) * mm]});
            skFitSpline(sketch, "E269", {"points": [v(-877.7, 173.77) * mm, v(-870.2, 174.17) * mm, v(-867.34, 172.83) * mm, v(-866.2, 168.35) * mm]});
            skFitSpline(sketch, "E270", {"points": [v(-866.2, 168.35) * mm, v(-865.73, 166.53) * mm, v(-864.41, 163.98) * mm, v(-863.26, 162.69) * mm]});
            skFitSpline(sketch, "E271", {"points": [v(-863.26, 162.69) * mm, v(-861.16, 160.32) * mm, v(-861.16, 160.32) * mm, v(-861.33, 112.16) * mm]});
            skFitSpline(sketch, "E272", {"points": [v(-861.33, 112.16) * mm, v(-861.46, 77.7) * mm, v(-861.83, 63.2) * mm, v(-862.63, 61.17) * mm]});
            skFitSpline(sketch, "E273", {"points": [v(-862.63, 61.17) * mm, v(-863.51, 58.93) * mm, v(-863.48, 57.85) * mm, v(-862.49, 55.98) * mm]});
            skFitSpline(sketch, "E274", {"points": [v(-862.49, 55.98) * mm, v(-860.76, 52.73) * mm, v(-860.89, 33.34) * mm, v(-862.66, 30.02) * mm]});
            skFitSpline(sketch, "E275", {"points": [v(-862.66, 30.02) * mm, v(-863.66, 28.16) * mm, v(-863.7, 27.35) * mm, v(-862.84, 26.5) * mm]});
            skFitSpline(sketch, "E276", {"points": [v(-862.84, 26.5) * mm, v(-861.44, 25.1) * mm, v(-861.4, 21.74) * mm, v(-862.76, 20.38) * mm]});
            skFitSpline(sketch, "E277", {"points": [v(-862.76, 20.38) * mm, v(-863.5, 19.63) * mm, v(-863.45, 18.73) * mm, v(-862.57, 17.12) * mm]});
            skFitSpline(sketch, "E278", {"points": [v(-862.57, 17.12) * mm, v(-861.7, 15.53) * mm, v(-861.42, 11.2) * mm, v(-861.62, 1.87) * mm]});
            skFitSpline(sketch, "E279", {"points": [v(-861.62, 1.87) * mm, v(-861.88, -10.78) * mm, v(-861.82, -11.24) * mm, v(-859.52, -14.26) * mm]});
            skFitSpline(sketch, "E280", {"points": [v(-859.52, -14.26) * mm, v(-857.22, -17.28) * mm, v(-857.14, -17.84) * mm, v(-857.06, -32.88) * mm]});
            skFitSpline(sketch, "E281", {"points": [v(-857.06, -32.88) * mm, v(-857.02, -41.4) * mm, v(-857.38, -49.75) * mm, v(-857.87, -51.43) * mm]});
            skFitSpline(sketch, "E282", {"points": [v(-857.87, -51.43) * mm, v(-858.41, -53.3) * mm, v(-858.41, -54.7) * mm, v(-857.88, -55.03) * mm]});
            skFitSpline(sketch, "E283", {"points": [v(-857.88, -55.03) * mm, v(-856.37, -55.96) * mm, v(-856.8, -67.72) * mm, v(-858.36, -68.32) * mm]});
            skFitSpline(sketch, "E284", {"points": [v(-858.36, -68.32) * mm, v(-859.1, -68.6) * mm, v(-860, -70.19) * mm, v(-860.36, -71.83) * mm]});
            skFitSpline(sketch, "E285", {"points": [v(-860.36, -71.83) * mm, v(-860.71, -73.47) * mm, v(-861.4, -75.31) * mm, v(-861.88, -75.92) * mm]});
            skFitSpline(sketch, "E286", {"points": [v(-861.88, -75.92) * mm, v(-862.43, -76.6) * mm, v(-862.4, -77.24) * mm, v(-861.78, -77.62) * mm]});
            skFitSpline(sketch, "E287", {"points": [v(-861.78, -77.62) * mm, v(-860.57, -78.37) * mm, v(-860.72, -85.3) * mm, v(-862, -88.51) * mm]});
            skFitSpline(sketch, "E288", {"points": [v(-862, -88.51) * mm, v(-862.97, -90.9) * mm, v(-862.93, -94.86) * mm, v(-861.94, -96.48) * mm]});
            skFitSpline(sketch, "E289", {"points": [v(-861.94, -96.48) * mm, v(-860.93, -98.12) * mm, v(-861.4, -113.52) * mm, v(-862.5, -115.6) * mm]});
            skFitSpline(sketch, "E290", {"points": [v(-862.5, -115.6) * mm, v(-864.01, -118.4) * mm, v(-863.9, -120.47) * mm, v(-862.14, -122.23) * mm]});
            skFitSpline(sketch, "E291", {"points": [v(-862.14, -122.23) * mm, v(-861.05, -123.32) * mm, v(-860.82, -124.68) * mm, v(-861.27, -127.32) * mm]});
            skFitSpline(sketch, "E292", {"points": [v(-861.27, -127.32) * mm, v(-861.77, -130.31) * mm, v(-861.46, -131.48) * mm, v(-859.44, -134.13) * mm]});
            skFitSpline(sketch, "E293", {"points": [v(-859.44, -134.13) * mm, v(-856.27, -138.29) * mm, v(-856.2, -143.28) * mm, v(-859.25, -147.36) * mm]});
            skFitSpline(sketch, "E294", {"points": [v(-859.25, -147.36) * mm, v(-860.74, -149.35) * mm, v(-861.66, -152.12) * mm, v(-861.96, -155.52) * mm]});
            skFitSpline(sketch, "E295", {"points": [v(-861.96, -155.52) * mm, v(-862.22, -158.36) * mm, v(-862.92, -160.84) * mm, v(-863.51, -161.04) * mm]});
            skFitSpline(sketch, "E296", {"points": [v(-863.51, -161.04) * mm, v(-865.93, -161.84) * mm, v(-867.32, -164.2) * mm, v(-866.83, -166.7) * mm]});
            skFitSpline(sketch, "E297", {"points": [v(-866.83, -166.7) * mm, v(-865.97, -171.05) * mm, v(-872.64, -175.4) * mm, v(-880.2, -175.4) * mm]});
            skFitSpline(sketch, "E298", {"points": [v(-880.2, -175.4) * mm, v(-883.41, -175.4) * mm, v(-887.32, -175.65) * mm, v(-888.88, -175.96) * mm]});
            skFitSpline(sketch, "E299", {"points": [v(-888.88, -175.96) * mm, v(-890.6, -176.3) * mm, v(-891.98, -176.1) * mm, v(-892.4, -175.43) * mm]});
            skFitSpline(sketch, "E300", {"points": [v(-752.74, -170.95) * mm, v(-754.94, -170.67) * mm, v(-757.68, -168.48) * mm, v(-763.92, -162.03) * mm]});
            skFitSpline(sketch, "E301", {"points": [v(-763.92, -162.03) * mm, v(-772.18, -153.48) * mm, v(-772.18, -153.48) * mm, v(-771.62, -148.62) * mm]});
            skFitSpline(sketch, "E302", {"points": [v(-771.57, -135.62) * mm, v(-772, -132.76) * mm, v(-771.87, -131.03) * mm, v(-771.18, -130.6) * mm]});
            skFitSpline(sketch, "E303", {"points": [v(-771.18, -130.6) * mm, v(-769.87, -129.8) * mm, v(-769.79, -125.66) * mm, v(-771.07, -124.87) * mm]});
            skFitSpline(sketch, "E304", {"points": [v(-771.07, -124.87) * mm, v(-772.48, -124) * mm, v(-772.23, -114.3) * mm, v(-770.76, -112.92) * mm]});
            skFitSpline(sketch, "E305", {"points": [v(-770.76, -112.92) * mm, v(-769.46, -111.7) * mm, v(-769.73, -107.75) * mm, v(-771.18, -106.86) * mm]});
            skFitSpline(sketch, "E306", {"points": [v(-771.18, -106.86) * mm, v(-772.65, -105.95) * mm, v(-772.12, -100) * mm, v(-770.49, -99.09) * mm]});
            skFitSpline(sketch, "E307", {"points": [v(-770.14, -96.03) * mm, v(-771.64, -93.23) * mm, v(-772.14, -79.2) * mm, v(-770.82, -76.74) * mm]});
            skFitSpline(sketch, "E308", {"points": [v(-770.82, -76.74) * mm, v(-769.6, -74.44) * mm, v(-769.74, -68.7) * mm, v(-771.05, -67.38) * mm]});
            skFitSpline(sketch, "E309", {"points": [v(-771.05, -67.38) * mm, v(-771.58, -66.85) * mm, v(-772.01, -64.12) * mm, v(-772.01, -61.32) * mm]});
            skFitSpline(sketch, "E310", {"points": [v(-772.01, -61.32) * mm, v(-772.01, -57.6) * mm, v(-772.54, -55.56) * mm, v(-773.97, -53.74) * mm]});
            skFitSpline(sketch, "E311", {"points": [v(-773.97, -53.74) * mm, v(-775.68, -51.57) * mm, v(-775.89, -50.2) * mm, v(-775.62, -42.88) * mm]});
            skFitSpline(sketch, "E312", {"points": [v(-775.62, -42.88) * mm, v(-775.32, -34.72) * mm, v(-775.38, -34.45) * mm, v(-777.91, -32.44) * mm]});
            skFitSpline(sketch, "E313", {"points": [v(-777.91, -32.44) * mm, v(-779.34, -31.3) * mm, v(-780.51, -29.49) * mm, v(-780.51, -28.42) * mm]});
            skFitSpline(sketch, "E314", {"points": [v(-780.51, -28.42) * mm, v(-780.51, -27.35) * mm, v(-781.35, -25.45) * mm, v(-782.38, -24.2) * mm]});
            skFitSpline(sketch, "E315", {"points": [v(-782.38, -24.2) * mm, v(-784.26, -21.91) * mm, v(-784.7, -21.47) * mm, v(-788.23, -18.28) * mm]});
            skFitSpline(sketch, "E316", {"points": [v(-788.23, -18.28) * mm, v(-789.82, -16.84) * mm, v(-790.08, -15.79) * mm, v(-789.64, -12.57) * mm]});
            skFitSpline(sketch, "E317", {"points": [v(-789.64, -12.57) * mm, v(-789.19, -9.28) * mm, v(-789.48, -8.17) * mm, v(-791.42, -5.92) * mm]});
            skFitSpline(sketch, "E318", {"points": [v(-791.42, -5.92) * mm, v(-793.4, -3.62) * mm, v(-793.73, -2.27) * mm, v(-793.73, 3.34) * mm]});
            skFitSpline(sketch, "E319", {"points": [v(-793.73, 3.34) * mm, v(-793.73, 9.28) * mm, v(-793.97, 10.08) * mm, v(-796.18, 11.83) * mm]});
            skFitSpline(sketch, "E320", {"points": [v(-796.18, 11.83) * mm, v(-798.55, 13.69) * mm, v(-798.62, 14.05) * mm, v(-798.3, 22.3) * mm]});
            skFitSpline(sketch, "E321", {"points": [v(-798.3, 22.3) * mm, v(-798, 30.15) * mm, v(-798.16, 31.04) * mm, v(-800.1, 32.99) * mm]});
            skFitSpline(sketch, "E322", {"points": [v(-800.1, 32.99) * mm, v(-801.48, 34.36) * mm, v(-802.23, 36.25) * mm, v(-802.23, 38.35) * mm]});
            skFitSpline(sketch, "E323", {"points": [v(-802.23, 38.35) * mm, v(-802.23, 40.8) * mm, v(-802.7, 41.7) * mm, v(-804.12, 42.08) * mm]});
            skFitSpline(sketch, "E324", {"points": [v(-804.12, 42.08) * mm, v(-805.2, 42.36) * mm, v(-806, 43.37) * mm, v(-806, 44.44) * mm]});
            skFitSpline(sketch, "E325", {"points": [v(-806, 44.44) * mm, v(-806, 45.46) * mm, v(-806.65, 46.83) * mm, v(-807.43, 47.47) * mm]});
            skFitSpline(sketch, "E326", {"points": [v(-807.43, 47.47) * mm, v(-808.2, 48.12) * mm, v(-808.84, 49.05) * mm, v(-808.84, 49.55) * mm]});
            skFitSpline(sketch, "E327", {"points": [v(-808.84, 49.55) * mm, v(-808.84, 50.04) * mm, v(-809.48, 51.08) * mm, v(-810.26, 51.86) * mm]});
            skFitSpline(sketch, "E328", {"points": [v(-810.26, 51.86) * mm, v(-811.04, 52.64) * mm, v(-811.68, 54.75) * mm, v(-811.68, 56.54) * mm]});
            skFitSpline(sketch, "E329", {"points": [v(-813.1, 60.35) * mm, v(-813.87, 60.65) * mm, v(-814.5, 61.66) * mm, v(-814.5, 62.6) * mm]});
            skFitSpline(sketch, "E330", {"points": [v(-814.5, 62.6) * mm, v(-814.5, 63.53) * mm, v(-816.03, 66.1) * mm, v(-817.88, 68.33) * mm]});
            skFitSpline(sketch, "E331", {"points": [v(-817.88, 68.33) * mm, v(-821.25, 72.37) * mm, v(-821.25, 72.37) * mm, v(-821.01, 85.9) * mm]});
            skFitSpline(sketch, "E332", {"points": [v(-821.01, 85.9) * mm, v(-820.8, 98.2) * mm, v(-820.93, 99.54) * mm, v(-822.54, 100.72) * mm]});
            skFitSpline(sketch, "E333", {"points": [v(-822.54, 100.72) * mm, v(-823.88, 101.7) * mm, v(-824.42, 103.54) * mm, v(-824.7, 108.14) * mm]});
            skFitSpline(sketch, "E334", {"points": [v(-824.7, 108.14) * mm, v(-825.4, 118.96) * mm, v(-815.54, 134.53) * mm, v(-805.06, 139.18) * mm]});
            skFitSpline(sketch, "E335", {"points": [v(-805.06, 139.18) * mm, v(-802.73, 140.21) * mm, v(-799.5, 142.34) * mm, v(-797.88, 143.9) * mm]});
            skFitSpline(sketch, "E336", {"points": [v(-797.88, 143.9) * mm, v(-793.5, 148.13) * mm, v(-784.89, 148.98) * mm, v(-783.23, 145.34) * mm]});
            skFitSpline(sketch, "E337", {"points": [v(-783.23, 145.34) * mm, v(-782.6, 143.97) * mm, v(-781.82, 142.85) * mm, v(-781.48, 142.85) * mm]});
            skFitSpline(sketch, "E338", {"points": [v(-781.48, 142.85) * mm, v(-781.14, 142.85) * mm, v(-779.94, 142) * mm, v(-778.8, 140.94) * mm]});
            skFitSpline(sketch, "E339", {"points": [v(-778.8, 140.94) * mm, v(-776.87, 139.13) * mm, v(-776.77, 138.34) * mm, v(-777.1, 127.95) * mm]});
            skFitSpline(sketch, "E340", {"points": [v(-777.1, 127.95) * mm, v(-777.42, 117.98) * mm, v(-777.27, 116.68) * mm, v(-775.6, 114.85) * mm]});
            skFitSpline(sketch, "E341", {"points": [v(-775.6, 114.85) * mm, v(-774.17, 113.29) * mm, v(-773.75, 111.52) * mm, v(-773.8, 107.3) * mm]});
            skFitSpline(sketch, "E342", {"points": [v(-773.8, 107.3) * mm, v(-773.98, 90.17) * mm, v(-774.03, 90.55) * mm, v(-771.53, 88.71) * mm]});
            skFitSpline(sketch, "E343", {"points": [v(-771.53, 88.71) * mm, v(-768.85, 86.74) * mm, v(-768.56, 85.05) * mm, v(-770.57, 83.05) * mm]});
            skFitSpline(sketch, "E344", {"points": [v(-770.57, 83.05) * mm, v(-771.8, 81.82) * mm, v(-771.74, 81.38) * mm, v(-770.1, 79.3) * mm]});
            skFitSpline(sketch, "E345", {"points": [v(-770.1, 79.3) * mm, v(-769.07, 77.99) * mm, v(-768.23, 75.62) * mm, v(-768.23, 74.04) * mm]});
            skFitSpline(sketch, "E346", {"points": [v(-768.23, 74.04) * mm, v(-768.23, 72.12) * mm, v(-767.6, 70.81) * mm, v(-766.35, 70.14) * mm]});
            skFitSpline(sketch, "E347", {"points": [v(-766.35, 70.14) * mm, v(-764.1, 68.94) * mm, v(-763.97, 67.92) * mm, v(-765.82, 66.08) * mm]});
            skFitSpline(sketch, "E348", {"points": [v(-765.82, 66.08) * mm, v(-767.2, 64.69) * mm, v(-766.82, 60.7) * mm, v(-765.3, 60.7) * mm]});
            skFitSpline(sketch, "E349", {"points": [v(-765.3, 60.7) * mm, v(-764.83, 60.7) * mm, v(-764.46, 59.38) * mm, v(-764.46, 57.76) * mm]});
            skFitSpline(sketch, "E350", {"points": [v(-764.46, 57.76) * mm, v(-764.46, 56) * mm, v(-763.5, 53.7) * mm, v(-762.05, 51.97) * mm]});
            skFitSpline(sketch, "E351", {"points": [v(-762.05, 51.97) * mm, v(-759.84, 49.34) * mm, v(-759.66, 48.45) * mm, v(-759.81, 40.84) * mm]});
            skFitSpline(sketch, "E352", {"points": [v(-759.81, 40.84) * mm, v(-759.9, 36.3) * mm, v(-759.69, 32.1) * mm, v(-759.33, 31.53) * mm]});
            skFitSpline(sketch, "E353", {"points": [v(-759.33, 31.53) * mm, v(-758.08, 29.51) * mm, v(-755.08, 30.45) * mm, v(-753.6, 33.3) * mm]});
            skFitSpline(sketch, "E354", {"points": [v(-753.6, 33.3) * mm, v(-752.8, 34.87) * mm, v(-751.72, 36.14) * mm, v(-751.21, 36.14) * mm]});
            skFitSpline(sketch, "E355", {"points": [v(-751.21, 36.14) * mm, v(-750.7, 36.14) * mm, v(-750.3, 37.6) * mm, v(-750.3, 39.4) * mm]});
            skFitSpline(sketch, "E356", {"points": [v(-750.3, 39.4) * mm, v(-750.3, 41.49) * mm, v(-749.67, 43.08) * mm, v(-748.54, 43.88) * mm]});
            skFitSpline(sketch, "E357", {"points": [v(-748.54, 43.88) * mm, v(-745.64, 45.92) * mm, v(-745.19, 49.05) * mm, v(-747.4, 51.86) * mm]});
            skFitSpline(sketch, "E358", {"points": [v(-747.4, 51.86) * mm, v(-749.97, 55.13) * mm, v(-749.86, 56.77) * mm, v(-747, 57.86) * mm]});
            skFitSpline(sketch, "E359", {"points": [v(-747, 57.86) * mm, v(-744.9, 58.66) * mm, v(-744.67, 59.25) * mm, v(-744.77, 63.7) * mm]});
            skFitSpline(sketch, "E360", {"points": [v(-744.77, 63.7) * mm, v(-744.86, 67.76) * mm, v(-744.53, 68.87) * mm, v(-742.86, 69.97) * mm]});
            skFitSpline(sketch, "E361", {"points": [v(-742.86, 69.97) * mm, v(-741.03, 71.2) * mm, v(-740.85, 72.16) * mm, v(-740.85, 80.77) * mm]});
            skFitSpline(sketch, "E362", {"points": [v(-740.85, 80.77) * mm, v(-740.85, 89.75) * mm, v(-740.72, 90.34) * mm, v(-738.39, 92.5) * mm]});
            skFitSpline(sketch, "E363", {"points": [v(-738.39, 92.5) * mm, v(-736.24, 94.5) * mm, v(-736, 95.3) * mm, v(-736.51, 98.75) * mm]});
            skFitSpline(sketch, "E364", {"points": [v(-736.51, 98.75) * mm, v(-737.2, 103.36) * mm, v(-735.92, 108.58) * mm, v(-733.72, 110.19) * mm]});
            skFitSpline(sketch, "E365", {"points": [v(-733.72, 110.19) * mm, v(-732.88, 110.8) * mm, v(-731.97, 112.99) * mm, v(-731.7, 115.04) * mm]});
            skFitSpline(sketch, "E366", {"points": [v(-731.7, 115.04) * mm, v(-731.42, 117.1) * mm, v(-730.44, 119.84) * mm, v(-729.52, 121.13) * mm]});
            skFitSpline(sketch, "E367", {"points": [v(-729.52, 121.13) * mm, v(-728.6, 122.43) * mm, v(-727.64, 125.34) * mm, v(-727.38, 127.6) * mm]});
            skFitSpline(sketch, "E368", {"points": [v(-727.38, 127.6) * mm, v(-726.8, 132.63) * mm, v(-725.13, 134.42) * mm, v(-720.62, 134.84) * mm]});
            skFitSpline(sketch, "E369", {"points": [v(-720.62, 134.84) * mm, v(-717.43, 135.14) * mm, v(-715.4, 136.72) * mm, v(-712.37, 141.28) * mm]});
            skFitSpline(sketch, "E370", {"points": [v(-712.37, 141.28) * mm, v(-712.03, 141.8) * mm, v(-707.26, 142.41) * mm, v(-701.78, 142.66) * mm]});
            skFitSpline(sketch, "E371", {"points": [v(-701.78, 142.66) * mm, v(-691.83, 143.1) * mm, v(-691.81, 143.1) * mm, v(-690.71, 140.69) * mm]});
            skFitSpline(sketch, "E372", {"points": [v(-690.71, 140.69) * mm, v(-690.11, 139.36) * mm, v(-688.66, 138.04) * mm, v(-687.49, 137.74) * mm]});
            skFitSpline(sketch, "E373", {"points": [v(-687.49, 137.74) * mm, v(-686.31, 137.45) * mm, v(-685.1, 136.25) * mm, v(-684.78, 135.07) * mm]});
            skFitSpline(sketch, "E374", {"points": [v(-684.78, 135.07) * mm, v(-683.67, 130.93) * mm, v(-684.13, 102.32) * mm, v(-685.33, 100.38) * mm]});
            skFitSpline(sketch, "E375", {"points": [v(-685.33, 100.38) * mm, v(-686.24, 98.94) * mm, v(-686.24, 97.86) * mm, v(-685.33, 95.37) * mm]});
            skFitSpline(sketch, "E376", {"points": [v(-685.33, 95.37) * mm, v(-683.73, 90.93) * mm, v(-683.9, 89.34) * mm, v(-686.12, 87.78) * mm]});
            skFitSpline(sketch, "E377", {"points": [v(-686.12, 87.78) * mm, v(-687.8, 86.6) * mm, v(-688.2, 84.78) * mm, v(-689.1, 74.27) * mm]});
            skFitSpline(sketch, "E378", {"points": [v(-689.1, 74.27) * mm, v(-690.12, 62.11) * mm, v(-690.12, 62.11) * mm, v(-693.86, 58.7) * mm]});
            skFitSpline(sketch, "E379", {"points": [v(-693.86, 58.7) * mm, v(-696.56, 56.23) * mm, v(-697.68, 54.4) * mm, v(-697.85, 52.16) * mm]});
            skFitSpline(sketch, "E380", {"points": [v(-697.85, 52.16) * mm, v(-697.99, 50.45) * mm, v(-698.72, 48.6) * mm, v(-699.49, 48.03) * mm]});
            skFitSpline(sketch, "E381", {"points": [v(-699.49, 48.03) * mm, v(-701.18, 46.78) * mm, v(-702.18, 43.1) * mm, v(-702.79, 35.9) * mm]});
            skFitSpline(sketch, "E382", {"points": [v(-702.79, 35.9) * mm, v(-703.13, 31.83) * mm, v(-703.73, 30.13) * mm, v(-705.18, 29.11) * mm]});
            skFitSpline(sketch, "E383", {"points": [v(-705.18, 29.11) * mm, v(-706.8, 27.97) * mm, v(-707.03, 27.05) * mm, v(-706.62, 23.39) * mm]});
            skFitSpline(sketch, "E384", {"points": [v(-706.62, 23.39) * mm, v(-706.13, 19.04) * mm, v(-706.36, 18.52) * mm, v(-709.91, 16.04) * mm]});
            skFitSpline(sketch, "E385", {"points": [v(-709.91, 16.04) * mm, v(-711.2, 15.15) * mm, v(-711.58, 13.44) * mm, v(-711.64, 8.28) * mm]});
            skFitSpline(sketch, "E386", {"points": [v(-711.64, 8.28) * mm, v(-711.73, 0.36) * mm, v(-712.2, -1.63) * mm, v(-714, -1.63) * mm]});
            skFitSpline(sketch, "E387", {"points": [v(-714, -1.63) * mm, v(-715.01, -1.63) * mm, v(-715.35, -2.96) * mm, v(-715.35, -6.92) * mm]});
            skFitSpline(sketch, "E388", {"points": [v(-715.35, -6.92) * mm, v(-715.35, -11.76) * mm, v(-716.51, -15.2) * mm, v(-719.6, -19.48) * mm]});
            skFitSpline(sketch, "E389", {"points": [v(-719.6, -19.48) * mm, v(-720.12, -20.21) * mm, v(-720.65, -23.82) * mm, v(-720.77, -27.51) * mm]});
            skFitSpline(sketch, "E390", {"points": [v(-720.77, -27.51) * mm, v(-720.9, -31.2) * mm, v(-721.26, -35.58) * mm, v(-721.58, -37.25) * mm]});
            skFitSpline(sketch, "E391", {"points": [v(-721.58, -37.25) * mm, v(-721.9, -38.92) * mm, v(-721.75, -41.48) * mm, v(-721.25, -42.92) * mm]});
            skFitSpline(sketch, "E392", {"points": [v(-721.25, -42.92) * mm, v(-720.22, -45.89) * mm, v(-721.27, -49.8) * mm, v(-723.43, -51.01) * mm]});
            skFitSpline(sketch, "E393", {"points": [v(-723.43, -51.01) * mm, v(-724.5, -51.62) * mm, v(-724.8, -54.28) * mm, v(-724.8, -63.55) * mm]});
            skFitSpline(sketch, "E394", {"points": [v(-724.8, -63.55) * mm, v(-724.8, -71.28) * mm, v(-725.2, -75.96) * mm, v(-725.97, -77.2) * mm]});
            skFitSpline(sketch, "E395", {"points": [v(-725.97, -77.2) * mm, v(-726.9, -78.69) * mm, v(-726.9, -79.45) * mm, v(-725.97, -80.95) * mm]});
            skFitSpline(sketch, "E396", {"points": [v(-725.97, -80.95) * mm, v(-724.4, -83.46) * mm, v(-724.34, -106.57) * mm, v(-725.9, -108.13) * mm]});
            skFitSpline(sketch, "E397", {"points": [v(-725.9, -108.13) * mm, v(-726.75, -108.98) * mm, v(-726.75, -109.8) * mm, v(-725.9, -111.67) * mm]});
            skFitSpline(sketch, "E398", {"points": [v(-725.9, -111.67) * mm, v(-724.5, -114.74) * mm, v(-724.45, -124.63) * mm, v(-725.84, -126) * mm]});
            skFitSpline(sketch, "E399", {"points": [v(-725.84, -126) * mm, v(-726.6, -126.77) * mm, v(-726.6, -128.37) * mm, v(-725.84, -131.9) * mm]});
            skFitSpline(sketch, "E400", {"points": [v(-725.84, -131.9) * mm, v(-723.86, -141.11) * mm, v(-724.44, -150.2) * mm, v(-727.15, -152.55) * mm]});
            skFitSpline(sketch, "E401", {"points": [v(-727.15, -152.55) * mm, v(-728.46, -153.7) * mm, v(-729.52, -155.63) * mm, v(-729.52, -156.9) * mm]});
            skFitSpline(sketch, "E402", {"points": [v(-729.52, -156.9) * mm, v(-729.52, -159.72) * mm, v(-731.8, -162.17) * mm, v(-734.45, -162.17) * mm]});
            skFitSpline(sketch, "E403", {"points": [v(-734.45, -162.17) * mm, v(-735.53, -162.17) * mm, v(-738.66, -164.3) * mm, v(-741.4, -166.9) * mm]});
            skFitSpline(sketch, "E404", {"points": [v(-741.4, -166.9) * mm, v(-744.15, -169.5) * mm, v(-747.17, -171.55) * mm, v(-748.11, -171.47) * mm]});
            skFitSpline(sketch, "E405", {"points": [v(-748.11, -171.47) * mm, v(-749.05, -171.38) * mm, v(-751.13, -171.15) * mm, v(-752.74, -170.95) * mm]});
            skFitSpline(sketch, "E406", {"points": [v(-588.8, -169.1) * mm, v(-590.26, -167.9) * mm, v(-592.23, -166.9) * mm, v(-593.2, -166.89) * mm]});
            skFitSpline(sketch, "E407", {"points": [v(-593.2, -166.89) * mm, v(-594.16, -166.88) * mm, v(-596.7, -165.2) * mm, v(-598.85, -163.14) * mm]});
            skFitSpline(sketch, "E408", {"points": [v(-598.85, -163.14) * mm, v(-602.75, -159.41) * mm, v(-602.75, -159.41) * mm, v(-602.77, -134.59) * mm]});
            skFitSpline(sketch, "E409", {"points": [v(-602.77, -134.59) * mm, v(-602.79, -118.34) * mm, v(-602.43, -109) * mm, v(-601.75, -107.58) * mm]});
            skFitSpline(sketch, "E410", {"points": [v(-601.75, -107.58) * mm, v(-600.97, -105.95) * mm, v(-601, -104.93) * mm, v(-601.84, -103.58) * mm]});
            skFitSpline(sketch, "E411", {"points": [v(-601.84, -103.58) * mm, v(-603.25, -101.32) * mm, v(-603.41, -78.51) * mm, v(-602.03, -77.65) * mm]});
            skFitSpline(sketch, "E412", {"points": [v(-602.03, -77.65) * mm, v(-601.5, -77.33) * mm, v(-601.08, -76.06) * mm, v(-601.08, -74.82) * mm]});
            skFitSpline(sketch, "E413", {"points": [v(-601.08, -74.82) * mm, v(-601.08, -73.58) * mm, v(-601.5, -72.3) * mm, v(-602.03, -71.99) * mm]});
            skFitSpline(sketch, "E414", {"points": [v(-602.03, -71.99) * mm, v(-602.56, -71.66) * mm, v(-602.97, -66.96) * mm, v(-602.97, -61.13) * mm]});
            skFitSpline(sketch, "E415", {"points": [v(-602.97, -61.13) * mm, v(-602.97, -55.3) * mm, v(-602.56, -50.6) * mm, v(-602.03, -50.27) * mm]});
            skFitSpline(sketch, "E416", {"points": [v(-602.03, -50.27) * mm, v(-600.83, -49.52) * mm, v(-600.8, -45.73) * mm, v(-601.99, -44.55) * mm]});
            skFitSpline(sketch, "E417", {"points": [v(-601.99, -44.55) * mm, v(-603.1, -43.43) * mm, v(-603.4, -28.71) * mm, v(-602.63, -12.55) * mm]});
            skFitSpline(sketch, "E418", {"points": [v(-602.63, -12.55) * mm, v(-602.04, -0.34) * mm, v(-602.04, -0.34) * mm, v(-605.41, 2.75) * mm]});
            skFitSpline(sketch, "E419", {"points": [v(-605.41, 2.75) * mm, v(-609.25, 6.26) * mm, v(-609.2, 8.76) * mm, v(-605.25, 12.1) * mm]});
            skFitSpline(sketch, "E420", {"points": [v(-605.25, 12.1) * mm, v(-603.73, 13.38) * mm, v(-602.97, 15.01) * mm, v(-602.97, 17) * mm]});
            skFitSpline(sketch, "E421", {"points": [v(-602.97, 17) * mm, v(-602.97, 18.64) * mm, v(-602.55, 20.24) * mm, v(-602.03, 20.56) * mm]});
            skFitSpline(sketch, "E422", {"points": [v(-602.03, 20.56) * mm, v(-601.5, 20.88) * mm, v(-601.08, 22.16) * mm, v(-601.08, 23.4) * mm]});
            skFitSpline(sketch, "E423", {"points": [v(-601.08, 23.4) * mm, v(-601.08, 24.63) * mm, v(-601.5, 25.9) * mm, v(-602.03, 26.23) * mm]});
            skFitSpline(sketch, "E424", {"points": [v(-602.03, 26.23) * mm, v(-602.55, 26.55) * mm, v(-602.97, 29.3) * mm, v(-602.97, 32.36) * mm]});
            skFitSpline(sketch, "E425", {"points": [v(-602.97, 32.36) * mm, v(-602.97, 35.42) * mm, v(-602.55, 38.18) * mm, v(-602.03, 38.5) * mm]});
            skFitSpline(sketch, "E426", {"points": [v(-602.03, 38.5) * mm, v(-601.5, 38.82) * mm, v(-601.08, 40.1) * mm, v(-601.08, 41.34) * mm]});
            skFitSpline(sketch, "E427", {"points": [v(-601.08, 41.34) * mm, v(-601.08, 42.57) * mm, v(-601.5, 43.85) * mm, v(-602.03, 44.17) * mm]});
            skFitSpline(sketch, "E428", {"points": [v(-602.03, 44.17) * mm, v(-602.55, 44.49) * mm, v(-602.97, 45.95) * mm, v(-602.97, 47.42) * mm]});
            skFitSpline(sketch, "E429", {"points": [v(-602.97, 47.42) * mm, v(-602.97, 49.23) * mm, v(-603.74, 50.6) * mm, v(-605.33, 51.64) * mm]});
            skFitSpline(sketch, "E430", {"points": [v(-605.33, 51.64) * mm, v(-607.52, 53.07) * mm, v(-608.68, 56.92) * mm, v(-606.92, 56.92) * mm]});
            skFitSpline(sketch, "E431", {"points": [v(-606.92, 56.92) * mm, v(-606.5, 56.92) * mm, v(-605.47, 58.36) * mm, v(-604.63, 60.12) * mm]});
            skFitSpline(sketch, "E432", {"points": [v(-604.63, 60.12) * mm, v(-603.11, 63.3) * mm, v(-603.12, 63.35) * mm, v(-605.91, 65.84) * mm]});
            skFitSpline(sketch, "E433", {"points": [v(-605.91, 65.84) * mm, v(-609.16, 68.73) * mm, v(-608.97, 71.2) * mm, v(-605.26, 74.58) * mm]});
            skFitSpline(sketch, "E434", {"points": [v(-605.26, 74.58) * mm, v(-600.23, 79.16) * mm, v(-604.53, 90.91) * mm, v(-611.24, 90.91) * mm]});
            skFitSpline(sketch, "E435", {"points": [v(-611.24, 90.91) * mm, v(-612.36, 90.91) * mm, v(-614.29, 91.93) * mm, v(-615.52, 93.17) * mm]});
            skFitSpline(sketch, "E436", {"points": [v(-615.52, 93.17) * mm, v(-617.64, 95.28) * mm, v(-618.28, 95.4) * mm, v(-626.2, 94.97) * mm]});
            skFitSpline(sketch, "E437", {"points": [v(-626.2, 94.97) * mm, v(-634.6, 94.53) * mm, v(-634.6, 94.53) * mm, v(-643.27, 103.07) * mm]});
            skFitSpline(sketch, "E438", {"points": [v(-643.27, 103.07) * mm, v(-651.94, 111.62) * mm, v(-651.94, 111.62) * mm, v(-651.73, 119.79) * mm]});
            skFitSpline(sketch, "E439", {"points": [v(-651.73, 119.79) * mm, v(-651.53, 127.6) * mm, v(-651.4, 128.02) * mm, v(-648.99, 129.29) * mm]});
            skFitSpline(sketch, "E440", {"points": [v(-648.99, 129.29) * mm, v(-647.6, 130.02) * mm, v(-646, 131.46) * mm, v(-645.46, 132.48) * mm]});
            skFitSpline(sketch, "E441", {"points": [v(-645.46, 132.48) * mm, v(-644.9, 133.51) * mm, v(-644, 134.36) * mm, v(-643.46, 134.36) * mm]});
            skFitSpline(sketch, "E442", {"points": [v(-643.46, 134.36) * mm, v(-642.9, 134.36) * mm, v(-641.33, 135.16) * mm, v(-639.95, 136.14) * mm]});
            skFitSpline(sketch, "E443", {"points": [v(-639.95, 136.14) * mm, v(-637.2, 138.09) * mm, v(-638.99, 138) * mm, v(-603.43, 138.02) * mm]});
            skFitSpline(sketch, "E444", {"points": [v(-603.43, 138.02) * mm, v(-591.48, 138.03) * mm, v(-580.1, 137.68) * mm, v(-578.17, 137.24) * mm]});
            skFitSpline(sketch, "E445", {"points": [v(-578.17, 137.24) * mm, v(-576.13, 136.78) * mm, v(-574.64, 136.8) * mm, v(-574.64, 137.29) * mm]});
            skFitSpline(sketch, "E446", {"points": [v(-574.64, 137.29) * mm, v(-574.64, 138.45) * mm, v(-557.9, 138.36) * mm, v(-557.17, 137.19) * mm]});
            skFitSpline(sketch, "E447", {"points": [v(-557.17, 137.19) * mm, v(-556.85, 136.67) * mm, v(-555.15, 136.24) * mm, v(-553.4, 136.24) * mm]});
            skFitSpline(sketch, "E448", {"points": [v(-553.4, 136.24) * mm, v(-551.64, 136.24) * mm, v(-549.94, 136.67) * mm, v(-549.61, 137.19) * mm]});
            skFitSpline(sketch, "E449", {"points": [v(-549.61, 137.19) * mm, v(-548.8, 138.5) * mm, v(-545.04, 138.37) * mm, v(-543.64, 136.98) * mm]});
            skFitSpline(sketch, "E450", {"points": [v(-543.64, 136.98) * mm, v(-542.73, 136.06) * mm, v(-542.1, 136.06) * mm, v(-540.63, 136.98) * mm]});
            skFitSpline(sketch, "E451", {"points": [v(-540.63, 136.98) * mm, v(-538.2, 138.5) * mm, v(-524.4, 138.51) * mm, v(-522.89, 137) * mm]});
            skFitSpline(sketch, "E452", {"points": [v(-522.89, 137) * mm, v(-522.27, 136.38) * mm, v(-521.76, 134.7) * mm, v(-521.76, 133.26) * mm]});
            skFitSpline(sketch, "E453", {"points": [v(-521.76, 133.26) * mm, v(-521.76, 131.67) * mm, v(-520.8, 129.77) * mm, v(-519.31, 128.39) * mm]});
            skFitSpline(sketch, "E454", {"points": [v(-519.31, 128.39) * mm, v(-517.55, 126.75) * mm, v(-516.76, 124.9) * mm, v(-516.46, 121.73) * mm]});
            skFitSpline(sketch, "E455", {"points": [v(-516.46, 121.73) * mm, v(-516.05, 117.33) * mm, v(-516.05, 117.33) * mm, v(-524.18, 108.9) * mm]});
            skFitSpline(sketch, "E456", {"points": [v(-524.18, 108.9) * mm, v(-529.59, 103.29) * mm, v(-533.25, 100.26) * mm, v(-535.14, 99.85) * mm]});
            skFitSpline(sketch, "E457", {"points": [v(-535.14, 99.85) * mm, v(-536.7, 99.5) * mm, v(-538.89, 98.2) * mm, v(-539.98, 96.93) * mm]});
            skFitSpline(sketch, "E458", {"points": [v(-539.98, 96.93) * mm, v(-541.85, 94.78) * mm, v(-542.47, 94.66) * mm, v(-549.57, 95.02) * mm]});
            skFitSpline(sketch, "E459", {"points": [v(-549.57, 95.02) * mm, v(-561.95, 95.65) * mm, v(-560.75, 99.09) * mm, v(-561.09, 62.04) * mm]});
            skFitSpline(sketch, "E460", {"points": [v(-561.09, 62.04) * mm, v(-561.25, 44.42) * mm, v(-561.41, 28.94) * mm, v(-561.45, 27.64) * mm]});
            skFitSpline(sketch, "E461", {"points": [v(-561.45, 27.64) * mm, v(-561.5, 26.34) * mm, v(-561.25, 23.77) * mm, v(-560.92, 21.92) * mm]});
            skFitSpline(sketch, "E462", {"points": [v(-560.92, 21.92) * mm, v(-560.47, 19.45) * mm, v(-560.7, 18.24) * mm, v(-561.8, 17.32) * mm]});
            skFitSpline(sketch, "E463", {"points": [v(-561.8, 17.32) * mm, v(-563.7, 15.76) * mm, v(-563.75, 10.65) * mm, v(-561.92, 8.23) * mm]});
            skFitSpline(sketch, "E464", {"points": [v(-561.92, 8.23) * mm, v(-559.84, 5.47) * mm, v(-559.84, -25.42) * mm, v(-561.93, -27.5) * mm]});
            skFitSpline(sketch, "E465", {"points": [v(-561.93, -27.5) * mm, v(-563.24, -28.82) * mm, v(-563.24, -29.24) * mm, v(-561.93, -31.78) * mm]});
            skFitSpline(sketch, "E466", {"points": [v(-561.93, -31.78) * mm, v(-559.9, -35.7) * mm, v(-559.87, -51.9) * mm, v(-561.89, -53.57) * mm]});
            skFitSpline(sketch, "E467", {"points": [v(-561.89, -53.57) * mm, v(-563.77, -55.13) * mm, v(-563.69, -57.99) * mm, v(-561.73, -59.08) * mm]});
            skFitSpline(sketch, "E468", {"points": [v(-561.73, -59.08) * mm, v(-560.26, -59.9) * mm, v(-560.27, -60.2) * mm, v(-561.81, -63.45) * mm]});
            skFitSpline(sketch, "E469", {"points": [v(-561.81, -63.45) * mm, v(-563.32, -66.64) * mm, v(-563.34, -67.08) * mm, v(-561.97, -68.6) * mm]});
            skFitSpline(sketch, "E470", {"points": [v(-561.97, -68.6) * mm, v(-560.1, -70.66) * mm, v(-560.06, -73.44) * mm, v(-561.86, -75.82) * mm]});
            skFitSpline(sketch, "E471", {"points": [v(-561.86, -75.82) * mm, v(-563.56, -78.07) * mm, v(-563.7, -80.67) * mm, v(-562.15, -81.19) * mm]});
            skFitSpline(sketch, "E472", {"points": [v(-562.15, -81.19) * mm, v(-560.57, -81.71) * mm, v(-560.12, -112.3) * mm, v(-561.63, -116.55) * mm]});
            skFitSpline(sketch, "E473", {"points": [v(-561.63, -116.55) * mm, v(-562.32, -118.49) * mm, v(-562.38, -120) * mm, v(-561.8, -120.8) * mm]});
            skFitSpline(sketch, "E474", {"points": [v(-561.8, -120.8) * mm, v(-561.29, -121.5) * mm, v(-560.9, -130.26) * mm, v(-560.92, -140.7) * mm]});
            skFitSpline(sketch, "E475", {"points": [v(-560.92, -140.7) * mm, v(-560.95, -159.35) * mm, v(-560.95, -159.35) * mm, v(-565.9, -163.84) * mm]});
            skFitSpline(sketch, "E476", {"points": [v(-565.9, -163.84) * mm, v(-568.63, -166.31) * mm, v(-570.86, -168.86) * mm, v(-570.86, -169.5) * mm]});
            skFitSpline(sketch, "E477", {"points": [v(-570.86, -169.5) * mm, v(-570.86, -170.83) * mm, v(-570.88, -170.83) * mm, v(-579.7, -171.11) * mm]});
            skFitSpline(sketch, "E478", {"points": [v(-579.7, -171.11) * mm, v(-585.3, -171.3) * mm, v(-586.54, -171.02) * mm, v(-588.8, -169.1) * mm]});
            skFitSpline(sketch, "E479", {"points": [v(1000.17, -167.15) * mm, v(999.84, -166.82) * mm, v(993.4, -166.66) * mm, v(985.87, -166.8) * mm]});
            skFitSpline(sketch, "E480", {"points": [v(985.87, -166.8) * mm, v(972.17, -167.04) * mm, v(972.17, -167.04) * mm, v(967.79, -162.72) * mm]});
            skFitSpline(sketch, "E481", {"points": [v(967.79, -162.72) * mm, v(964.8, -159.78) * mm, v(962.6, -158.4) * mm, v(960.9, -158.4) * mm]});
            skFitSpline(sketch, "E482", {"points": [v(960.9, -158.4) * mm, v(959.22, -158.4) * mm, v(957.72, -157.47) * mm, v(956.31, -155.56) * mm]});
            skFitSpline(sketch, "E483", {"points": [v(956.31, -155.56) * mm, v(954.82, -153.54) * mm, v(953.43, -152.73) * mm, v(951.46, -152.73) * mm]});
            skFitSpline(sketch, "E484", {"points": [v(951.46, -152.73) * mm, v(949.87, -152.73) * mm, v(948.33, -152.06) * mm, v(947.82, -151.16) * mm]});
            skFitSpline(sketch, "E485", {"points": [v(947.82, -151.16) * mm, v(947.3, -150.23) * mm, v(945.23, -149.35) * mm, v(942.82, -149.02) * mm]});
            skFitSpline(sketch, "E486", {"points": [v(942.82, -149.02) * mm, v(939.01, -148.51) * mm, v(938.69, -148.25) * mm, v(938.61, -145.64) * mm]});
            skFitSpline(sketch, "E487", {"points": [v(938.61, -145.64) * mm, v(938.48, -140.85) * mm, v(938.34, -140.69) * mm, v(933.97, -140.03) * mm]});
            skFitSpline(sketch, "E488", {"points": [v(933.97, -140.03) * mm, v(929.97, -139.43) * mm, v(929.72, -139.22) * mm, v(929.72, -136.43) * mm]});
            skFitSpline(sketch, "E489", {"points": [v(929.72, -136.43) * mm, v(929.72, -134.4) * mm, v(928.81, -132.52) * mm, v(926.86, -130.5) * mm]});
            skFitSpline(sketch, "E490", {"points": [v(926.86, -130.5) * mm, v(923.8, -127.36) * mm, v(923.93, -128.25) * mm, v(924.3, -112.6) * mm]});
            skFitSpline(sketch, "E491", {"points": [v(924.3, -112.6) * mm, v(924.37, -109.48) * mm, v(924.29, -106.08) * mm, v(924.1, -105.04) * mm]});
            skFitSpline(sketch, "E492", {"points": [v(924.1, -105.04) * mm, v(923.9, -104) * mm, v(923.83, -99.75) * mm, v(923.92, -95.6) * mm]});
            skFitSpline(sketch, "E493", {"points": [v(923.92, -95.6) * mm, v(924.07, -88.13) * mm, v(924.12, -88) * mm, v(927.92, -84.03) * mm]});
            skFitSpline(sketch, "E494", {"points": [v(927.92, -84.03) * mm, v(931.51, -80.27) * mm, v(932.07, -80.01) * mm, v(936.9, -80.01) * mm]});
            skFitSpline(sketch, "E495", {"points": [v(936.9, -80.01) * mm, v(940.65, -80.01) * mm, v(942.2, -80.4) * mm, v(942.61, -81.45) * mm]});
            skFitSpline(sketch, "E496", {"points": [v(942.61, -81.45) * mm, v(943.01, -82.5) * mm, v(943.49, -82.63) * mm, v(944.37, -81.9) * mm]});
            skFitSpline(sketch, "E497", {"points": [v(944.37, -81.9) * mm, v(946.77, -79.9) * mm, v(964.51, -79.16) * mm, v(965.83, -81) * mm]});
            skFitSpline(sketch, "E498", {"points": [v(965.83, -81) * mm, v(970.66, -87.68) * mm, v(971.37, -89.47) * mm, v(971.4, -94.9) * mm]});
            skFitSpline(sketch, "E499", {"points": [v(971.4, -94.9) * mm, v(971.42, -99.91) * mm, v(971.75, -100.9) * mm, v(974.15, -103.2) * mm]});
            skFitSpline(sketch, "E500", {"points": [v(974.15, -103.2) * mm, v(976.1, -105.06) * mm, v(976.84, -106.64) * mm, v(976.76, -108.75) * mm]});
            skFitSpline(sketch, "E501", {"points": [v(976.76, -108.75) * mm, v(976.7, -110.37) * mm, v(977.68, -113.55) * mm, v(978.94, -115.82) * mm]});
            skFitSpline(sketch, "E502", {"points": [v(978.94, -115.82) * mm, v(981.23, -119.93) * mm, v(981.23, -119.93) * mm, v(995.71, -119.9) * mm]});
            skFitSpline(sketch, "E503", {"points": [v(995.71, -119.9) * mm, v(1011.68, -119.85) * mm, v(1011.8, -119.8) * mm, v(1012.56, -113.89) * mm]});
            skFitSpline(sketch, "E504", {"points": [v(1012.56, -113.89) * mm, v(1012.85, -111.62) * mm, v(1013.88, -109) * mm, v(1014.84, -108.07) * mm]});
            skFitSpline(sketch, "E505", {"points": [v(1014.84, -108.07) * mm, v(1016.64, -106.34) * mm, v(1016.9, -105.27) * mm, v(1016.66, -100.32) * mm]});
            skFitSpline(sketch, "E506", {"points": [v(1016.66, -100.32) * mm, v(1016.58, -98.43) * mm, v(1017.36, -96.6) * mm, v(1019.03, -94.82) * mm]});
            skFitSpline(sketch, "E507", {"points": [v(1019.03, -94.82) * mm, v(1020.44, -93.32) * mm, v(1021.6, -90.88) * mm, v(1021.73, -89.21) * mm]});
            skFitSpline(sketch, "E508", {"points": [v(1021.73, -89.21) * mm, v(1021.84, -87.6) * mm, v(1022.43, -86.1) * mm, v(1023.04, -85.9) * mm]});
            skFitSpline(sketch, "E509", {"points": [v(1023.04, -85.9) * mm, v(1024.68, -85.35) * mm, v(1024.4, -82.13) * mm, v(1022.63, -81.14) * mm]});
            skFitSpline(sketch, "E510", {"points": [v(1022.63, -81.14) * mm, v(1021.3, -80.4) * mm, v(1021.26, -79.86) * mm, v(1022.34, -76.88) * mm]});
            skFitSpline(sketch, "E511", {"points": [v(1022.34, -76.88) * mm, v(1023.35, -74.08) * mm, v(1023.35, -73.06) * mm, v(1022.34, -71.17) * mm]});
            skFitSpline(sketch, "E512", {"points": [v(1022.34, -71.17) * mm, v(1021.66, -69.9) * mm, v(1021.36, -68.45) * mm, v(1021.67, -67.94) * mm]});
            skFitSpline(sketch, "E513", {"points": [v(1021.67, -67.94) * mm, v(1021.99, -67.43) * mm, v(1020.95, -65.39) * mm, v(1019.36, -63.4) * mm]});
            skFitSpline(sketch, "E514", {"points": [v(1019.36, -63.4) * mm, v(1016.81, -60.19) * mm, v(1016.51, -59.16) * mm, v(1016.7, -54.3) * mm]});
            skFitSpline(sketch, "E515", {"points": [v(1016.7, -54.3) * mm, v(1016.9, -49.68) * mm, v(1016.6, -48.52) * mm, v(1014.83, -46.86) * mm]});
            skFitSpline(sketch, "E516", {"points": [v(1014.83, -46.86) * mm, v(1013.6, -45.72) * mm, v(1012.84, -44.04) * mm, v(1013, -42.86) * mm]});
            skFitSpline(sketch, "E517", {"points": [v(1013, -42.86) * mm, v(1013.45, -39.72) * mm, v(1008.8, -36.13) * mm, v(1006.14, -37.56) * mm]});
            skFitSpline(sketch, "E518", {"points": [v(1006.14, -37.56) * mm, v(1005.02, -38.16) * mm, v(1001.04, -38.71) * mm, v(997.3, -38.8) * mm]});
            skFitSpline(sketch, "E519", {"points": [v(997.3, -38.8) * mm, v(990.77, -38.93) * mm, v(990.36, -38.8) * mm, v(987.37, -35.82) * mm]});
            skFitSpline(sketch, "E520", {"points": [v(987.37, -35.82) * mm, v(984.81, -33.26) * mm, v(983.77, -32.8) * mm, v(981.56, -33.3) * mm]});
            skFitSpline(sketch, "E521", {"points": [v(981.56, -33.3) * mm, v(977.5, -34.18) * mm, v(969.12, -31.37) * mm, v(965.47, -27.9) * mm]});
            skFitSpline(sketch, "E522", {"points": [v(965.47, -27.9) * mm, v(963.73, -26.23) * mm, v(961.65, -24.96) * mm, v(960.84, -25.08) * mm]});
            skFitSpline(sketch, "E523", {"points": [v(960.84, -25.08) * mm, v(960.04, -25.2) * mm, v(958.37, -24.22) * mm, v(957.13, -22.9) * mm]});
            skFitSpline(sketch, "E524", {"points": [v(957.13, -22.9) * mm, v(955.9, -21.6) * mm, v(953.86, -20.52) * mm, v(952.6, -20.52) * mm]});
            skFitSpline(sketch, "E525", {"points": [v(952.6, -20.52) * mm, v(949.62, -20.52) * mm, v(932.07, -3.32) * mm, v(932.88, -1.2) * mm]});
            skFitSpline(sketch, "E526", {"points": [v(932.88, -1.2) * mm, v(933.18, -0.43) * mm, v(932.66, 0.75) * mm, v(931.73, 1.41) * mm]});
            skFitSpline(sketch, "E527", {"points": [v(931.73, 1.41) * mm, v(929.4, 3.08) * mm, v(928.65, 6.6) * mm, v(930.28, 8.24) * mm]});
            skFitSpline(sketch, "E528", {"points": [v(930.28, 8.24) * mm, v(931.93, 9.89) * mm, v(928.86, 15.86) * mm, v(925.88, 16.8) * mm]});
            skFitSpline(sketch, "E529", {"points": [v(925.88, 16.8) * mm, v(923.51, 17.56) * mm, v(922.55, 21.53) * mm, v(924.06, 24.34) * mm]});
            skFitSpline(sketch, "E530", {"points": [v(924.06, 24.34) * mm, v(924.74, 25.62) * mm, v(924.98, 27.7) * mm, v(924.63, 29.23) * mm]});
            skFitSpline(sketch, "E531", {"points": [v(924.63, 29.23) * mm, v(923.58, 33.77) * mm, v(923.28, 53.52) * mm, v(924.23, 55.33) * mm]});
            skFitSpline(sketch, "E532", {"points": [v(924.23, 55.33) * mm, v(924.84, 56.49) * mm, v(924.76, 57.49) * mm, v(923.98, 58.43) * mm]});
            skFitSpline(sketch, "E533", {"points": [v(923.98, 58.43) * mm, v(923.07, 59.53) * mm, v(923.07, 61.22) * mm, v(924, 66.44) * mm]});
            skFitSpline(sketch, "E534", {"points": [v(924, 66.44) * mm, v(924.65, 70.07) * mm, v(924.88, 74.2) * mm, v(924.51, 75.6) * mm]});
            skFitSpline(sketch, "E535", {"points": [v(924.51, 75.6) * mm, v(924.15, 77.01) * mm, v(923.82, 81.94) * mm, v(923.8, 86.54) * mm]});
            skFitSpline(sketch, "E536", {"points": [v(923.8, 86.54) * mm, v(923.74, 94.92) * mm, v(923.74, 94.92) * mm, v(927.6, 98.13) * mm]});
            skFitSpline(sketch, "E537", {"points": [v(927.6, 98.13) * mm, v(932.09, 101.86) * mm, v(937.02, 109.8) * mm, v(934.85, 109.8) * mm]});
            skFitSpline(sketch, "E538", {"points": [v(934.85, 109.8) * mm, v(933.04, 109.8) * mm, v(933.13, 113.2) * mm, v(934.98, 114.72) * mm]});
            skFitSpline(sketch, "E539", {"points": [v(934.98, 114.72) * mm, v(935.8, 115.4) * mm, v(937.34, 116.73) * mm, v(938.4, 117.7) * mm]});
            skFitSpline(sketch, "E540", {"points": [v(938.4, 117.7) * mm, v(939.46, 118.67) * mm, v(941.43, 119.76) * mm, v(942.77, 120.12) * mm]});
            skFitSpline(sketch, "E541", {"points": [v(942.77, 120.12) * mm, v(944.48, 120.58) * mm, v(945.45, 121.68) * mm, v(945.99, 123.78) * mm]});
            skFitSpline(sketch, "E542", {"points": [v(945.99, 123.78) * mm, v(946.42, 125.44) * mm, v(947.82, 127.48) * mm, v(949.1, 128.32) * mm]});
            skFitSpline(sketch, "E543", {"points": [v(949.1, 128.32) * mm, v(950.4, 129.16) * mm, v(951.44, 130.6) * mm, v(951.44, 131.53) * mm]});
            skFitSpline(sketch, "E544", {"points": [v(951.44, 131.53) * mm, v(951.44, 133.66) * mm, v(953.32, 134.38) * mm, v(957.29, 133.78) * mm]});
            skFitSpline(sketch, "E545", {"points": [v(957.29, 133.78) * mm, v(961.43, 133.16) * mm, v(973.16, 140.43) * mm, v(973.16, 143.62) * mm]});
            skFitSpline(sketch, "E546", {"points": [v(973.16, 143.62) * mm, v(973.16, 144.08) * mm, v(973.98, 145.2) * mm, v(974.98, 146.1) * mm]});
            skFitSpline(sketch, "E547", {"points": [v(974.98, 146.1) * mm, v(977.53, 148.4) * mm, v(1013.54, 147.77) * mm, v(1018.26, 145.34) * mm]});
            skFitSpline(sketch, "E548", {"points": [v(1018.26, 145.34) * mm, v(1019.9, 144.5) * mm, v(1021.8, 143.8) * mm, v(1022.5, 143.8) * mm]});
            skFitSpline(sketch, "E549", {"points": [v(1022.5, 143.8) * mm, v(1023.19, 143.8) * mm, v(1025.23, 142.54) * mm, v(1027.03, 141) * mm]});
            skFitSpline(sketch, "E550", {"points": [v(1027.03, 141) * mm, v(1028.82, 139.47) * mm, v(1031.09, 138.2) * mm, v(1032.06, 138.17) * mm]});
            skFitSpline(sketch, "E551", {"points": [v(1032.06, 138.17) * mm, v(1034.4, 138.12) * mm, v(1041.42, 131.02) * mm, v(1041.7, 128.4) * mm]});
            skFitSpline(sketch, "E552", {"points": [v(1041.7, 128.4) * mm, v(1041.84, 127.26) * mm, v(1041.98, 126) * mm, v(1042.02, 125.62) * mm]});
            skFitSpline(sketch, "E553", {"points": [v(1042.02, 125.62) * mm, v(1042.06, 125.23) * mm, v(1043.3, 124.91) * mm, v(1044.79, 124.91) * mm]});
            skFitSpline(sketch, "E554", {"points": [v(1044.79, 124.91) * mm, v(1049.97, 124.91) * mm, v(1050.6, 123) * mm, v(1050.6, 107.14) * mm]});
            skFitSpline(sketch, "E555", {"points": [v(1050.6, 107.14) * mm, v(1050.6, 93.84) * mm, v(1050.46, 92.74) * mm, v(1048.7, 91.64) * mm]});
            skFitSpline(sketch, "E556", {"points": [v(1048.7, 91.64) * mm, v(1047.05, 90.6) * mm, v(1046.82, 89.44) * mm, v(1046.82, 81.93) * mm]});
            skFitSpline(sketch, "E557", {"points": [v(1046.82, 81.93) * mm, v(1046.82, 70.06) * mm, v(1046.12, 69.2) * mm, v(1036.58, 69.2) * mm]});
            skFitSpline(sketch, "E558", {"points": [v(1036.58, 69.2) * mm, v(1029.27, 69.2) * mm, v(1029.27, 69.2) * mm, v(1025.1, 73.44) * mm]});
            skFitSpline(sketch, "E559", {"points": [v(1025.1, 73.44) * mm, v(1022.8, 75.78) * mm, v(1020.45, 77.7) * mm, v(1019.87, 77.7) * mm]});
            skFitSpline(sketch, "E560", {"points": [v(1019.87, 77.7) * mm, v(1019.3, 77.7) * mm, v(1017.57, 79.26) * mm, v(1016.06, 81.17) * mm]});
            skFitSpline(sketch, "E561", {"points": [v(1016.06, 81.17) * mm, v(1014.54, 83.08) * mm, v(1012.13, 85.73) * mm, v(1010.7, 87.05) * mm]});
            skFitSpline(sketch, "E562", {"points": [v(1010.7, 87.05) * mm, v(1009.27, 88.37) * mm, v(1008.1, 90.39) * mm, v(1008.1, 91.54) * mm]});
            skFitSpline(sketch, "E563", {"points": [v(1008.1, 91.54) * mm, v(1008.1, 94.32) * mm, v(1007.3, 94.7) * mm, v(1000.47, 95.14) * mm]});
            skFitSpline(sketch, "E564", {"points": [v(1000.47, 95.14) * mm, v(995.29, 95.47) * mm, v(994.44, 95.26) * mm, v(992.54, 93.21) * mm]});
            skFitSpline(sketch, "E565", {"points": [v(992.54, 93.21) * mm, v(991.3, 91.86) * mm, v(989.35, 90.91) * mm, v(987.84, 90.91) * mm]});
            skFitSpline(sketch, "E566", {"points": [v(987.84, 90.91) * mm, v(985.37, 90.91) * mm, v(979.77, 86.73) * mm, v(979.77, 84.88) * mm]});
            skFitSpline(sketch, "E567", {"points": [v(979.77, 84.88) * mm, v(979.77, 84.42) * mm, v(979.08, 83.54) * mm, v(978.24, 82.92) * mm]});
            skFitSpline(sketch, "E568", {"points": [v(978.24, 82.92) * mm, v(975.76, 81.1) * mm, v(975.21, 72.6) * mm, v(976.33, 53.14) * mm]});
            skFitSpline(sketch, "E569", {"points": [v(976.33, 53.14) * mm, v(976.56, 49.24) * mm, v(976.32, 45.55) * mm, v(975.82, 44.92) * mm]});
            skFitSpline(sketch, "E570", {"points": [v(975.82, 44.92) * mm, v(975.3, 44.3) * mm, v(975.17, 42.91) * mm, v(975.51, 41.84) * mm]});
            skFitSpline(sketch, "E571", {"points": [v(975.51, 41.84) * mm, v(975.85, 40.77) * mm, v(976.26, 37.24) * mm, v(976.42, 34) * mm]});
            skFitSpline(sketch, "E572", {"points": [v(976.42, 34) * mm, v(976.7, 28.38) * mm, v(979.78, 21.18) * mm, v(981.96, 21.07) * mm]});
            skFitSpline(sketch, "E573", {"points": [v(981.96, 21.07) * mm, v(982.4, 21.05) * mm, v(983.38, 20.4) * mm, v(984.15, 19.62) * mm]});
            skFitSpline(sketch, "E574", {"points": [v(984.15, 19.62) * mm, v(984.93, 18.84) * mm, v(986.58, 18.2) * mm, v(987.8, 18.2) * mm]});
            skFitSpline(sketch, "E575", {"points": [v(987.8, 18.2) * mm, v(989.26, 18.2) * mm, v(991.6, 16.53) * mm, v(994.58, 13.37) * mm]});
            skFitSpline(sketch, "E576", {"points": [v(994.58, 13.37) * mm, v(999.13, 8.54) * mm, v(999.13, 8.54) * mm, v(1005.6, 9.07) * mm]});
            skFitSpline(sketch, "E577", {"points": [v(1005.6, 9.07) * mm, v(1011.53, 9.56) * mm, v(1012.25, 9.42) * mm, v(1014.32, 7.34) * mm]});
            skFitSpline(sketch, "E578", {"points": [v(1014.32, 7.34) * mm, v(1015.98, 5.69) * mm, v(1017.54, 5.11) * mm, v(1020.14, 5.2) * mm]});
            skFitSpline(sketch, "E579", {"points": [v(1020.14, 5.2) * mm, v(1025.64, 5.39) * mm, v(1039.53, -3.77) * mm, v(1039.08, -7.3) * mm]});
            skFitSpline(sketch, "E580", {"points": [v(1039.08, -7.3) * mm, v(1038.98, -8.08) * mm, v(1040.68, -10.57) * mm, v(1042.86, -12.85) * mm]});
            skFitSpline(sketch, "E581", {"points": [v(1042.86, -12.85) * mm, v(1045.04, -15.12) * mm, v(1046.82, -17.86) * mm, v(1046.82, -18.95) * mm]});
            skFitSpline(sketch, "E582", {"points": [v(1046.82, -18.95) * mm, v(1046.82, -20.04) * mm, v(1048.83, -22.97) * mm, v(1051.29, -25.46) * mm]});
            skFitSpline(sketch, "E583", {"points": [v(1051.29, -25.46) * mm, v(1055.23, -29.47) * mm, v(1055.62, -30.21) * mm, v(1054.6, -31.86) * mm]});
            skFitSpline(sketch, "E584", {"points": [v(1054.6, -31.86) * mm, v(1053.16, -34.14) * mm, v(1053.09, -37.2) * mm, v(1054.43, -38.03) * mm]});
            skFitSpline(sketch, "E585", {"points": [v(1054.43, -38.03) * mm, v(1055.1, -38.44) * mm, v(1055.37, -44.68) * mm, v(1055.24, -56.48) * mm]});
            skFitSpline(sketch, "E586", {"points": [v(1055.24, -56.48) * mm, v(1055.03, -74.32) * mm, v(1055.03, -74.32) * mm, v(1057.53, -76.3) * mm]});
            skFitSpline(sketch, "E587", {"points": [v(1057.53, -76.3) * mm, v(1060, -78.23) * mm, v(1060.04, -78.44) * mm, v(1060.04, -89.8) * mm]});
            skFitSpline(sketch, "E588", {"points": [v(1060.04, -89.8) * mm, v(1060.04, -96.16) * mm, v(1059.66, -101.76) * mm, v(1059.2, -102.25) * mm]});
            skFitSpline(sketch, "E589", {"points": [v(1059.2, -102.25) * mm, v(1057.88, -103.66) * mm, v(1059.09, -108.92) * mm, v(1061.27, -111.27) * mm]});
            skFitSpline(sketch, "E590", {"points": [v(1061.27, -111.27) * mm, v(1063.86, -114.04) * mm, v(1064.75, -123.66) * mm, v(1062.65, -126.09) * mm]});
            skFitSpline(sketch, "E591", {"points": [v(1062.65, -126.09) * mm, v(1061.87, -126.98) * mm, v(1060.95, -128.94) * mm, v(1060.59, -130.45) * mm]});
            skFitSpline(sketch, "E592", {"points": [v(1060.59, -130.45) * mm, v(1060.23, -131.95) * mm, v(1058.68, -134.35) * mm, v(1057.15, -135.78) * mm]});
            skFitSpline(sketch, "E593", {"points": [v(1057.15, -135.78) * mm, v(1055.63, -137.2) * mm, v(1054.38, -139.11) * mm, v(1054.38, -140) * mm]});
            skFitSpline(sketch, "E594", {"points": [v(1054.38, -140) * mm, v(1054.38, -140.9) * mm, v(1049.8, -146.2) * mm, v(1044.22, -151.76) * mm]});
            skFitSpline(sketch, "E595", {"points": [v(1044.22, -151.76) * mm, v(1034.8, -161.17) * mm, v(1033.75, -161.93) * mm, v(1029.57, -162.49) * mm]});
            skFitSpline(sketch, "E596", {"points": [v(1029.57, -162.49) * mm, v(1027.1, -162.82) * mm, v(1023.9, -163.9) * mm, v(1022.49, -164.9) * mm]});
            skFitSpline(sketch, "E597", {"points": [v(1022.49, -164.9) * mm, v(1019.89, -166.72) * mm, v(1001.59, -168.57) * mm, v(1000.17, -167.15) * mm]});
            skFitSpline(sketch, "E598", {"points": [v(-212, -166.06) * mm, v(-212, -165.6) * mm, v(-212.86, -165) * mm, v(-213.9, -164.73) * mm]});
            skFitSpline(sketch, "E599", {"points": [v(-213.9, -164.73) * mm, v(-214.94, -164.46) * mm, v(-215.78, -163.67) * mm, v(-215.78, -162.97) * mm]});
            skFitSpline(sketch, "E600", {"points": [v(-215.78, -162.97) * mm, v(-215.78, -161.94) * mm, v(-219.1, -161.75) * mm, v(-233.07, -161.98) * mm]});
            skFitSpline(sketch, "E601", {"points": [v(-233.07, -161.98) * mm, v(-252.16, -162.28) * mm, v(-252.23, -162.26) * mm, v(-254.22, -156.03) * mm]});
            skFitSpline(sketch, "E602", {"points": [v(-254.22, -156.03) * mm, v(-254.88, -153.96) * mm, v(-255.8, -153.12) * mm, v(-257.63, -152.9) * mm]});
            skFitSpline(sketch, "E603", {"points": [v(-257.63, -152.9) * mm, v(-260.62, -152.55) * mm, v(-263, -149.5) * mm, v(-263, -146.04) * mm]});
            skFitSpline(sketch, "E604", {"points": [v(-263, -146.04) * mm, v(-263, -144.66) * mm, v(-263.83, -142.49) * mm, v(-264.85, -141.2) * mm]});
            skFitSpline(sketch, "E605", {"points": [v(-264.85, -141.2) * mm, v(-266.76, -138.76) * mm, v(-266.82, -137.92) * mm, v(-266.64, -114.96) * mm]});
            skFitSpline(sketch, "E606", {"points": [v(-266.64, -114.96) * mm, v(-266.61, -110.54) * mm, v(-266.6, -101.4) * mm, v(-266.63, -94.65) * mm]});
            skFitSpline(sketch, "E607", {"points": [v(-266.63, -94.65) * mm, v(-266.65, -87.9) * mm, v(-266.63, -80.89) * mm, v(-266.57, -79.07) * mm]});
            skFitSpline(sketch, "E608", {"points": [v(-266.57, -79.07) * mm, v(-266.5, -77.25) * mm, v(-266.48, -67.48) * mm, v(-266.5, -57.35) * mm]});
            skFitSpline(sketch, "E609", {"points": [v(-266.5, -57.35) * mm, v(-266.53, -47.22) * mm, v(-266.53, -37.23) * mm, v(-266.5, -35.16) * mm]});
            skFitSpline(sketch, "E610", {"points": [v(-266.5, -35.16) * mm, v(-266.44, -29.65) * mm, v(-266.5, 102.98) * mm, v(-266.57, 107.44) * mm]});
            skFitSpline(sketch, "E611", {"points": [v(-266.57, 107.44) * mm, v(-267.25, 153.7) * mm, v(-266.95, 157.77) * mm, v(-262.52, 161.84) * mm]});
            skFitSpline(sketch, "E612", {"points": [v(-262.52, 161.84) * mm, v(-260, 164.17) * mm, v(-258.28, 166.6) * mm, v(-258.28, 167.8) * mm]});
            skFitSpline(sketch, "E613", {"points": [v(-258.28, 167.8) * mm, v(-258.28, 168.96) * mm, v(-256.54, 171.56) * mm, v(-254.26, 173.78) * mm]});
            skFitSpline(sketch, "E614", {"points": [v(-254.26, 173.78) * mm, v(-250.25, 177.72) * mm, v(-250.25, 177.72) * mm, v(-236.56, 177.83) * mm]});
            skFitSpline(sketch, "E615", {"points": [v(-236.56, 177.83) * mm, v(-229.02, 177.89) * mm, v(-221.09, 178.33) * mm, v(-218.91, 178.8) * mm]});
            skFitSpline(sketch, "E616", {"points": [v(-218.91, 178.8) * mm, v(-216.74, 179.27) * mm, v(-210.16, 179.77) * mm, v(-204.28, 179.9) * mm]});
            skFitSpline(sketch, "E617", {"points": [v(-204.28, 179.9) * mm, v(-193.79, 180.15) * mm, v(-193.49, 180.1) * mm, v(-188.26, 177.14) * mm]});
            skFitSpline(sketch, "E618", {"points": [v(-188.26, 177.14) * mm, v(-182.93, 174.12) * mm, v(-182.93, 174.12) * mm, v(-170.96, 175.18) * mm]});
            skFitSpline(sketch, "E619", {"points": [v(-170.96, 175.18) * mm, v(-161.87, 175.99) * mm, v(-158.25, 175.97) * mm, v(-155.92, 175.13) * mm]});
            skFitSpline(sketch, "E620", {"points": [v(-155.92, 175.13) * mm, v(-154.23, 174.52) * mm, v(-151.48, 174.02) * mm, v(-149.82, 174.02) * mm]});
            skFitSpline(sketch, "E621", {"points": [v(-149.82, 174.02) * mm, v(-147.5, 174.02) * mm, v(-146.6, 173.5) * mm, v(-145.94, 171.76) * mm]});
            skFitSpline(sketch, "E622", {"points": [v(-145.94, 171.76) * mm, v(-145.46, 170.51) * mm, v(-144.73, 169.34) * mm, v(-144.3, 169.16) * mm]});
            skFitSpline(sketch, "E623", {"points": [v(-144.3, 169.16) * mm, v(-143.88, 168.97) * mm, v(-142.55, 166.8) * mm, v(-141.34, 164.34) * mm]});
            skFitSpline(sketch, "E624", {"points": [v(-141.34, 164.34) * mm, v(-139.63, 160.83) * mm, v(-138.66, 159.85) * mm, v(-136.88, 159.85) * mm]});
            skFitSpline(sketch, "E625", {"points": [v(-136.88, 159.85) * mm, v(-132.63, 159.85) * mm, v(-127.65, 153.81) * mm, v(-127.72, 148.76) * mm]});
            skFitSpline(sketch, "E626", {"points": [v(-127.72, 148.76) * mm, v(-127.77, 145.12) * mm, v(-127.33, 143.98) * mm, v(-125.04, 141.83) * mm]});
            skFitSpline(sketch, "E627", {"points": [v(-125.04, 141.83) * mm, v(-122.29, 139.26) * mm, v(-122.29, 139.26) * mm, v(-122.29, 114.52) * mm]});
            skFitSpline(sketch, "E628", {"points": [v(-122.29, 114.52) * mm, v(-122.29, 89.78) * mm, v(-122.29, 89.78) * mm, v(-125.2, 87.07) * mm]});
            skFitSpline(sketch, "E629", {"points": [v(-125.2, 87.07) * mm, v(-128.1, 84.35) * mm, v(-128.1, 84.35) * mm, v(-127.54, 75.12) * mm]});
            skFitSpline(sketch, "E630", {"points": [v(-127.54, 75.12) * mm, v(-127.22, 70.04) * mm, v(-126.56, 64.19) * mm, v(-126.07, 62.11) * mm]});
            skFitSpline(sketch, "E631", {"points": [v(-126.07, 62.11) * mm, v(-124.43, 55.25) * mm, v(-124.87, 51.25) * mm, v(-127.48, 49.2) * mm]});
            skFitSpline(sketch, "E632", {"points": [v(-127.48, 49.2) * mm, v(-129.77, 47.4) * mm, v(-130.7, 44.64) * mm, v(-129, 44.64) * mm]});
            skFitSpline(sketch, "E633", {"points": [v(-129, 44.64) * mm, v(-127.68, 44.64) * mm, v(-127, 40.6) * mm, v(-128.1, 39.28) * mm]});
            skFitSpline(sketch, "E634", {"points": [v(-128.1, 39.28) * mm, v(-128.76, 38.47) * mm, v(-128.8, 37.2) * mm, v(-128.2, 35.45) * mm]});
            skFitSpline(sketch, "E635", {"points": [v(-128.2, 35.45) * mm, v(-126.84, 31.48) * mm, v(-127.9, 21.02) * mm, v(-129.87, 18.9) * mm]});
            skFitSpline(sketch, "E636", {"points": [v(-129.87, 18.9) * mm, v(-131.8, 16.83) * mm, v(-131.37, 9.9) * mm, v(-129.22, 8.28) * mm]});
            skFitSpline(sketch, "E637", {"points": [v(-129.22, 8.28) * mm, v(-127.44, 6.95) * mm, v(-127.04, -5.2) * mm, v(-128.74, -6.25) * mm]});
            skFitSpline(sketch, "E638", {"points": [v(-128.74, -6.25) * mm, v(-129.69, -6.84) * mm, v(-129.49, -7.17) * mm, v(-127.94, -7.58) * mm]});
            skFitSpline(sketch, "E639", {"points": [v(-127.94, -7.58) * mm, v(-126.57, -7.93) * mm, v(-126.13, -8.52) * mm, v(-126.62, -9.32) * mm]});
            skFitSpline(sketch, "E640", {"points": [v(-126.62, -9.32) * mm, v(-127.45, -10.66) * mm, v(-128.2, -75.8) * mm, v(-127.41, -78.31) * mm]});
            skFitSpline(sketch, "E641", {"points": [v(-127.41, -78.31) * mm, v(-127.14, -79.2) * mm, v(-126.15, -80.16) * mm, v(-125.22, -80.46) * mm]});
            skFitSpline(sketch, "E642", {"points": [v(-125.22, -80.46) * mm, v(-120.77, -81.87) * mm, v(-120.9, -87.72) * mm, v(-125.46, -90.7) * mm]});
            skFitSpline(sketch, "E643", {"points": [v(-125.46, -90.7) * mm, v(-127.95, -92.33) * mm, v(-129, -101.45) * mm, v(-126.85, -102.78) * mm]});
            skFitSpline(sketch, "E644", {"points": [v(-126.85, -102.78) * mm, v(-125.33, -103.72) * mm, v(-127.87, -116.93) * mm, v(-129.97, -118.98) * mm]});
            skFitSpline(sketch, "E645", {"points": [v(-129.97, -118.98) * mm, v(-130.9, -119.89) * mm, v(-131.51, -121.16) * mm, v(-131.32, -121.8) * mm]});
            skFitSpline(sketch, "E646", {"points": [v(-131.32, -121.8) * mm, v(-128.8, -130.31) * mm, v(-128.7, -131.81) * mm, v(-130.4, -135.66) * mm]});
            skFitSpline(sketch, "E647", {"points": [v(-130.4, -135.66) * mm, v(-131.33, -137.77) * mm, v(-132.45, -139.5) * mm, v(-132.89, -139.5) * mm]});
            skFitSpline(sketch, "E648", {"points": [v(-132.89, -139.5) * mm, v(-133.33, -139.5) * mm, v(-135.1, -140.9) * mm, v(-136.83, -142.58) * mm]});
            skFitSpline(sketch, "E649", {"points": [v(-136.83, -142.58) * mm, v(-145.39, -150.92) * mm, v(-147.74, -152.73) * mm, v(-150.03, -152.73) * mm]});
            skFitSpline(sketch, "E650", {"points": [v(-150.03, -152.73) * mm, v(-151.62, -152.73) * mm, v(-153.17, -153.7) * mm, v(-154.55, -155.56) * mm]});
            skFitSpline(sketch, "E651", {"points": [v(-154.55, -155.56) * mm, v(-156.32, -157.96) * mm, v(-157.28, -158.4) * mm, v(-160.75, -158.4) * mm]});
            skFitSpline(sketch, "E652", {"points": [v(-160.75, -158.4) * mm, v(-163.6, -158.4) * mm, v(-165.5, -159) * mm, v(-166.94, -160.33) * mm]});
            skFitSpline(sketch, "E653", {"points": [v(-166.94, -160.33) * mm, v(-168.09, -161.4) * mm, v(-169.77, -162.08) * mm, v(-170.68, -161.84) * mm]});
            skFitSpline(sketch, "E654", {"points": [v(-170.68, -161.84) * mm, v(-171.6, -161.6) * mm, v(-172.34, -161.68) * mm, v(-172.34, -162.03) * mm]});
            skFitSpline(sketch, "E655", {"points": [v(-172.34, -162.03) * mm, v(-172.34, -162.37) * mm, v(-179.46, -162.5) * mm, v(-188.16, -162.32) * mm]});
            skFitSpline(sketch, "E656", {"points": [v(-188.16, -162.32) * mm, v(-203.98, -162) * mm, v(-203.98, -162) * mm, v(-206.62, -164.44) * mm]});
            skFitSpline(sketch, "E657", {"points": [v(-206.62, -164.44) * mm, v(-209.23, -166.86) * mm, v(-212, -167.7) * mm, v(-212, -166.06) * mm]});
            skFitSpline(sketch, "E658", {"points": [v(-199.38, -114.3) * mm, v(-200.48, -114.09) * mm, v(-202.36, -112.87) * mm, v(-203.55, -111.6) * mm]});
            skFitSpline(sketch, "E659", {"points": [v(-203.55, -111.6) * mm, v(-204.85, -110.22) * mm, v(-206.79, -109.29) * mm, v(-208.36, -109.29) * mm]});
            skFitSpline(sketch, "E660", {"points": [v(-208.36, -109.29) * mm, v(-209.93, -109.29) * mm, v(-211.36, -108.6) * mm, v(-211.9, -107.6) * mm]});
            skFitSpline(sketch, "E661", {"points": [v(-211.9, -107.6) * mm, v(-212.4, -106.67) * mm, v(-213.88, -105.33) * mm, v(-215.2, -104.63) * mm]});
            skFitSpline(sketch, "E662", {"points": [v(-215.2, -104.63) * mm, v(-217.3, -103.5) * mm, v(-217.63, -102.64) * mm, v(-217.87, -97.68) * mm]});
            skFitSpline(sketch, "E663", {"points": [v(-217.87, -97.68) * mm, v(-218.09, -93.17) * mm, v(-218.53, -91.8) * mm, v(-220.03, -90.97) * mm]});
            skFitSpline(sketch, "E664", {"points": [v(-220.03, -90.97) * mm, v(-222.89, -89.4) * mm, v(-223.2, -88.57) * mm, v(-222.25, -85.1) * mm]});
            skFitSpline(sketch, "E665", {"points": [v(-222.29, -80.22) * mm, v(-222.81, -79.24) * mm, v(-223.17, -69.04) * mm, v(-223.12, -56.38) * mm]});
            skFitSpline(sketch, "E666", {"points": [v(-223.12, -56.38) * mm, v(-223.05, -34.26) * mm, v(-223.05, -34.26) * mm, v(-220.4, -31.94) * mm]});
            skFitSpline(sketch, "E667", {"points": [v(-220.4, -31.94) * mm, v(-218.05, -29.88) * mm, v(-217.82, -29.17) * mm, v(-218.3, -25.59) * mm]});
            skFitSpline(sketch, "E668", {"points": [v(-218.3, -25.59) * mm, v(-218.83, -21.77) * mm, v(-218.63, -21.33) * mm, v(-214.56, -17.26) * mm]});
            skFitSpline(sketch, "E669", {"points": [v(-214.56, -17.26) * mm, v(-212.1, -14.8) * mm, v(-209.4, -12.96) * mm, v(-208.22, -12.96) * mm]});
            skFitSpline(sketch, "E670", {"points": [v(-208.22, -12.96) * mm, v(-207.09, -12.96) * mm, v(-205.09, -12.11) * mm, v(-203.77, -11.08) * mm]});
            skFitSpline(sketch, "E671", {"points": [v(-203.77, -11.08) * mm, v(-200.23, -8.3) * mm, v(-187.05, -8.3) * mm, v(-185.56, -11.08) * mm]});
            skFitSpline(sketch, "E672", {"points": [v(-185.56, -11.08) * mm, v(-184.74, -12.61) * mm, v(-183.59, -12.96) * mm, v(-179.4, -12.96) * mm]});
            skFitSpline(sketch, "E673", {"points": [v(-179.4, -12.96) * mm, v(-171.9, -12.96) * mm, v(-170.46, -14.7) * mm, v(-170.46, -23.77) * mm]});
            skFitSpline(sketch, "E674", {"points": [v(-170.46, -23.77) * mm, v(-170.46, -27.63) * mm, v(-170.83, -31.03) * mm, v(-171.29, -31.3) * mm]});
            skFitSpline(sketch, "E675", {"points": [v(-171.29, -31.3) * mm, v(-172.77, -32.23) * mm, v(-173.08, -36.52) * mm, v(-171.74, -37.63) * mm]});
            skFitSpline(sketch, "E676", {"points": [v(-171.74, -37.63) * mm, v(-170.1, -38.99) * mm, v(-170.01, -49.85) * mm, v(-171.6, -54.25) * mm]});
            skFitSpline(sketch, "E677", {"points": [v(-171.6, -54.25) * mm, v(-172.5, -56.74) * mm, v(-172.5, -57.82) * mm, v(-171.6, -59.26) * mm]});
            skFitSpline(sketch, "E678", {"points": [v(-171.6, -59.26) * mm, v(-170.8, -60.55) * mm, v(-170.46, -67) * mm, v(-170.46, -80.95) * mm]});
            skFitSpline(sketch, "E679", {"points": [v(-170.46, -80.95) * mm, v(-170.46, -102.69) * mm, v(-170.93, -104.57) * mm, v(-176.48, -104.57) * mm]});
            skFitSpline(sketch, "E680", {"points": [v(-176.48, -104.57) * mm, v(-177.84, -104.57) * mm, v(-179.35, -105.5) * mm, v(-180.28, -106.93) * mm]});
            skFitSpline(sketch, "E681", {"points": [v(-180.28, -106.93) * mm, v(-181.2, -108.34) * mm, v(-182.72, -109.29) * mm, v(-184.05, -109.29) * mm]});
            skFitSpline(sketch, "E682", {"points": [v(-184.05, -109.29) * mm, v(-186.95, -109.29) * mm, v(-192.46, -111.61) * mm, v(-194.02, -113.48) * mm]});
            skFitSpline(sketch, "E683", {"points": [v(-194.02, -113.48) * mm, v(-195.24, -114.96) * mm, v(-195.68, -115.03) * mm, v(-199.38, -114.3) * mm]});
            skFitSpline(sketch, "E684", {"points": [v(-211.84, 26.05) * mm, v(-212.97, 27.25) * mm, v(-213.9, 28.78) * mm, v(-213.9, 29.45) * mm]});
            skFitSpline(sketch, "E685", {"points": [v(-213.9, 29.45) * mm, v(-213.9, 30.11) * mm, v(-214.82, 31.96) * mm, v(-215.96, 33.55) * mm]});
            skFitSpline(sketch, "E686", {"points": [v(-215.96, 33.55) * mm, v(-217.94, 36.33) * mm, v(-218.03, 37.45) * mm, v(-218.3, 63.09) * mm]});
            skFitSpline(sketch, "E687", {"points": [v(-218.3, 63.09) * mm, v(-218.58, 89.73) * mm, v(-218.58, 89.73) * mm, v(-215.77, 92.67) * mm]});
            skFitSpline(sketch, "E688", {"points": [v(-215.77, 92.67) * mm, v(-212.8, 95.78) * mm, v(-211.93, 100.85) * mm, v(-214.02, 102.93) * mm]});
            skFitSpline(sketch, "E689", {"points": [v(-214.02, 102.93) * mm, v(-215.6, 104.51) * mm, v(-214.17, 108.77) * mm, v(-211.69, 109.9) * mm]});
            skFitSpline(sketch, "E690", {"points": [v(-211.69, 109.9) * mm, v(-210.5, 110.44) * mm, v(-209.07, 112.13) * mm, v(-208.5, 113.65) * mm]});
            skFitSpline(sketch, "E691", {"points": [v(-208.5, 113.65) * mm, v(-207.51, 116.25) * mm, v(-207.14, 116.41) * mm, v(-202.17, 116.41) * mm]});
            skFitSpline(sketch, "E692", {"points": [v(-202.17, 116.41) * mm, v(-198.16, 116.41) * mm, v(-196.45, 116.86) * mm, v(-195, 118.3) * mm]});
            skFitSpline(sketch, "E693", {"points": [v(-195, 118.3) * mm, v(-193.37, 119.94) * mm, v(-191.86, 120.19) * mm, v(-183.57, 120.19) * mm]});
            skFitSpline(sketch, "E694", {"points": [v(-183.57, 120.19) * mm, v(-174.01, 120.19) * mm, v(-174.01, 120.19) * mm, v(-170.24, 116.18) * mm]});
            skFitSpline(sketch, "E695", {"points": [v(-170.24, 116.18) * mm, v(-166.46, 112.17) * mm, v(-166.46, 112.17) * mm, v(-166.86, 101) * mm]});
            skFitSpline(sketch, "E696", {"points": [v(-166.86, 101) * mm, v(-167.26, 89.83) * mm, v(-167.26, 89.83) * mm, v(-164.72, 88.52) * mm]});
            skFitSpline(sketch, "E697", {"points": [v(-164.72, 88.52) * mm, v(-161.17, 86.68) * mm, v(-159.8, 79.58) * mm, v(-163, 79.58) * mm]});
            skFitSpline(sketch, "E698", {"points": [v(-163, 79.58) * mm, v(-164.16, 79.58) * mm, v(-164.07, 75.11) * mm, v(-162.9, 74.39) * mm]});
            skFitSpline(sketch, "E699", {"points": [v(-162.9, 74.39) * mm, v(-161.36, 73.44) * mm, v(-161.82, 70.88) * mm, v(-163.94, 68.62) * mm]});
            skFitSpline(sketch, "E700", {"points": [v(-163.94, 68.62) * mm, v(-165.93, 66.5) * mm, v(-165.93, 66.5) * mm, v(-163.94, 64.8) * mm]});
            skFitSpline(sketch, "E701", {"points": [v(-163.94, 64.8) * mm, v(-161.9, 63.06) * mm, v(-161.07, 56.92) * mm, v(-162.88, 56.92) * mm]});
            skFitSpline(sketch, "E702", {"points": [v(-162.88, 56.92) * mm, v(-164.82, 56.92) * mm, v(-166.99, 50.78) * mm, v(-166.77, 45.91) * mm]});
            skFitSpline(sketch, "E703", {"points": [v(-166.77, 45.91) * mm, v(-166.65, 43.23) * mm, v(-167, 40.15) * mm, v(-167.56, 39.06) * mm]});
            skFitSpline(sketch, "E704", {"points": [v(-167.56, 39.06) * mm, v(-168.11, 37.98) * mm, v(-169, 36.24) * mm, v(-169.51, 35.21) * mm]});
            skFitSpline(sketch, "E705", {"points": [v(-169.51, 35.21) * mm, v(-170.03, 34.18) * mm, v(-170.46, 32.73) * mm, v(-170.46, 31.98) * mm]});
            skFitSpline(sketch, "E706", {"points": [v(-170.46, 31.98) * mm, v(-170.46, 31.24) * mm, v(-171.9, 29.74) * mm, v(-173.67, 28.64) * mm]});
            skFitSpline(sketch, "E707", {"points": [v(-173.67, 28.64) * mm, v(-175.43, 27.55) * mm, v(-177.12, 26.03) * mm, v(-177.42, 25.26) * mm]});
            skFitSpline(sketch, "E708", {"points": [v(-177.42, 25.26) * mm, v(-177.86, 24.1) * mm, v(-180.69, 23.87) * mm, v(-193.87, 23.87) * mm]});
            skFitSpline(sketch, "E709", {"points": [v(-193.87, 23.87) * mm, v(-209.29, 23.87) * mm, v(-209.85, 23.93) * mm, v(-211.84, 26.05) * mm]});
            skFitSpline(sketch, "E710", {"points": [v(376.95, -160.6) * mm, v(373.54, -157.13) * mm, v(370.48, -153.12) * mm, v(370.17, -151.69) * mm]});
            skFitSpline(sketch, "E711", {"points": [v(370.17, -151.69) * mm, v(369.56, -148.92) * mm, v(371.81, -143.4) * mm, v(374.1, -142.06) * mm]});
            skFitSpline(sketch, "E712", {"points": [v(374.1, -142.06) * mm, v(375.94, -140.98) * mm, v(375.69, -137.6) * mm, v(373.59, -135.32) * mm]});
            skFitSpline(sketch, "E713", {"points": [v(373.59, -135.32) * mm, v(370.6, -132.09) * mm, v(370.01, -122.3) * mm, v(370.43, -83.32) * mm]});
            skFitSpline(sketch, "E714", {"points": [v(370.43, -83.32) * mm, v(370.84, -44.27) * mm, v(370.84, -45) * mm, v(370.87, -30.44) * mm]});
            skFitSpline(sketch, "E715", {"points": [v(370.87, -30.44) * mm, v(370.88, -25.24) * mm, v(370.9, -18.02) * mm, v(370.91, -14.38) * mm]});
            skFitSpline(sketch, "E716", {"points": [v(370.91, -14.38) * mm, v(370.93, -10.75) * mm, v(370.86, 10.1) * mm, v(370.75, 31.92) * mm]});
            skFitSpline(sketch, "E717", {"points": [v(370.75, 31.92) * mm, v(370.64, 53.75) * mm, v(370.82, 72.32) * mm, v(371.16, 73.2) * mm]});
            skFitSpline(sketch, "E718", {"points": [v(371.16, 73.2) * mm, v(371.55, 74.21) * mm, v(370.9, 75.65) * mm, v(369.32, 77.22) * mm]});
            skFitSpline(sketch, "E719", {"points": [v(369.32, 77.22) * mm, v(366.5, 80.04) * mm, v(366.22, 81.95) * mm, v(368.44, 83.2) * mm]});
            skFitSpline(sketch, "E720", {"points": [v(368.44, 83.2) * mm, v(370.34, 84.26) * mm, v(369.4, 87.58) * mm, v(367.42, 86.82) * mm]});
            skFitSpline(sketch, "E721", {"points": [v(367.42, 86.82) * mm, v(366.02, 86.29) * mm, v(357.92, 92.06) * mm, v(357.12, 94.16) * mm]});
            skFitSpline(sketch, "E722", {"points": [v(357.12, 94.16) * mm, v(356.76, 95.08) * mm, v(354.48, 95.28) * mm, v(347.83, 94.96) * mm]});
            skFitSpline(sketch, "E723", {"points": [v(347.83, 94.96) * mm, v(339.02, 94.53) * mm, v(339.02, 94.53) * mm, v(333.84, 99.33) * mm]});
            skFitSpline(sketch, "E724", {"points": [v(333.84, 99.33) * mm, v(331, 101.97) * mm, v(327.98, 104.14) * mm, v(327.14, 104.14) * mm]});
            skFitSpline(sketch, "E725", {"points": [v(327.14, 104.14) * mm, v(323.48, 104.14) * mm, v(322.03, 107.69) * mm, v(321.7, 117.51) * mm]});
            skFitSpline(sketch, "E726", {"points": [v(321.7, 117.51) * mm, v(321.28, 129.32) * mm, v(322.26, 132.08) * mm, v(327.35, 133.45) * mm]});
            skFitSpline(sketch, "E727", {"points": [v(327.35, 133.45) * mm, v(329.37, 134) * mm, v(331.55, 135.27) * mm, v(332.18, 136.29) * mm]});
            skFitSpline(sketch, "E728", {"points": [v(332.18, 136.29) * mm, v(332.94, 137.5) * mm, v(334.38, 138.13) * mm, v(336.36, 138.13) * mm]});
            skFitSpline(sketch, "E729", {"points": [v(336.36, 138.13) * mm, v(338.02, 138.13) * mm, v(339.65, 138.56) * mm, v(339.97, 139.1) * mm]});
            skFitSpline(sketch, "E730", {"points": [v(339.97, 139.1) * mm, v(342.22, 142.72) * mm, v(372.53, 144.69) * mm, v(380.7, 141.73) * mm]});
            skFitSpline(sketch, "E731", {"points": [v(386.06, 141.81) * mm, v(387.75, 142.72) * mm, v(392.45, 142.88) * mm, v(405.21, 142.47) * mm]});
            skFitSpline(sketch, "E732", {"points": [v(405.21, 142.47) * mm, v(414.51, 142.17) * mm, v(423.66, 141.9) * mm, v(425.54, 141.88) * mm]});
            skFitSpline(sketch, "E733", {"points": [v(425.54, 141.88) * mm, v(427.71, 141.86) * mm, v(429.58, 141.17) * mm, v(430.65, 140) * mm]});
            skFitSpline(sketch, "E734", {"points": [v(430.65, 140) * mm, v(432.1, 138.39) * mm, v(433.58, 138.13) * mm, v(441.51, 138.13) * mm]});
            skFitSpline(sketch, "E735", {"points": [v(441.51, 138.13) * mm, v(451.56, 138.13) * mm, v(452.15, 137.85) * mm, v(453.3, 132.48) * mm]});
            skFitSpline(sketch, "E736", {"points": [v(453.3, 132.48) * mm, v(453.69, 130.67) * mm, v(454.65, 128.72) * mm, v(455.44, 128.14) * mm]});
            skFitSpline(sketch, "E737", {"points": [v(455.44, 128.14) * mm, v(456.54, 127.33) * mm, v(456.92, 124.76) * mm, v(457.09, 117.04) * mm]});
            skFitSpline(sketch, "E738", {"points": [v(457.09, 117.04) * mm, v(457.3, 106.36) * mm, v(457.1, 105.8) * mm, v(452.55, 104.71) * mm]});
            skFitSpline(sketch, "E739", {"points": [v(452.55, 104.71) * mm, v(451.1, 104.37) * mm, v(449.2, 103.25) * mm, v(448.32, 102.22) * mm]});
            skFitSpline(sketch, "E740", {"points": [v(448.32, 102.22) * mm, v(447.3, 101.02) * mm, v(445.54, 100.36) * mm, v(443.38, 100.36) * mm]});
            skFitSpline(sketch, "E741", {"points": [v(443.38, 100.36) * mm, v(440.83, 100.36) * mm, v(439.82, 99.86) * mm, v(439.1, 98.25) * mm]});
            skFitSpline(sketch, "E742", {"points": [v(439.1, 98.25) * mm, v(438.6, 97.09) * mm, v(436.9, 95.76) * mm, v(435.34, 95.3) * mm]});
            skFitSpline(sketch, "E743", {"points": [v(435.34, 95.3) * mm, v(433.78, 94.83) * mm, v(430.43, 93.65) * mm, v(427.9, 92.68) * mm]});
            skFitSpline(sketch, "E744", {"points": [v(427.9, 92.68) * mm, v(425.36, 91.7) * mm, v(421.05, 90.91) * mm, v(418.32, 90.91) * mm]});
            skFitSpline(sketch, "E745", {"points": [v(418.32, 90.91) * mm, v(413.19, 90.91) * mm, v(411.56, 89.68) * mm, v(413.22, 87.05) * mm]});
            skFitSpline(sketch, "E746", {"points": [v(413.22, 87.05) * mm, v(413.7, 86.3) * mm, v(414.02, 37.55) * mm, v(413.97, -25.54) * mm]});
            skFitSpline(sketch, "E747", {"points": [v(413.97, -25.54) * mm, v(413.9, -136.8) * mm, v(413.9, -136.8) * mm, v(416.02, -139.07) * mm]});
            skFitSpline(sketch, "E748", {"points": [v(416.02, -139.07) * mm, v(418.51, -141.73) * mm, v(418.19, -150.53) * mm, v(415.53, -152.02) * mm]});
            skFitSpline(sketch, "E749", {"points": [v(415.53, -152.02) * mm, v(414.74, -152.46) * mm, v(414.1, -153.78) * mm, v(414.1, -154.95) * mm]});
            skFitSpline(sketch, "E750", {"points": [v(414.1, -154.95) * mm, v(414.1, -156.97) * mm, v(412.2, -160.02) * mm, v(407.98, -164.79) * mm]});
            skFitSpline(sketch, "E751", {"points": [v(407.98, -164.79) * mm, v(406.25, -166.75) * mm, v(405.33, -166.9) * mm, v(394.64, -166.9) * mm]});
            skFitSpline(sketch, "E752", {"points": [v(394.64, -166.9) * mm, v(383.15, -166.9) * mm, v(383.15, -166.9) * mm, v(376.94, -160.6) * mm]});
            skFitSpline(sketch, "E753", {"points": [v(-451.87, -160.28) * mm, v(-452.58, -158.96) * mm, v(-453.85, -158.4) * mm, v(-456.12, -158.4) * mm]});
            skFitSpline(sketch, "E754", {"points": [v(-456.12, -158.4) * mm, v(-458.52, -158.4) * mm, v(-459.65, -157.85) * mm, v(-460.47, -156.27) * mm]});
            skFitSpline(sketch, "E755", {"points": [v(-460.47, -156.27) * mm, v(-461.08, -155.1) * mm, v(-462.85, -153.07) * mm, v(-464.4, -151.76) * mm]});
            skFitSpline(sketch, "E756", {"points": [v(-464.4, -151.76) * mm, v(-467.38, -149.22) * mm, v(-467.45, -148.4) * mm, v(-465.52, -137.5) * mm]});
            skFitSpline(sketch, "E757", {"points": [v(-465.52, -137.5) * mm, v(-465.15, -135.39) * mm, v(-465.31, -133.82) * mm, v(-465.95, -133.43) * mm]});
            skFitSpline(sketch, "E758", {"points": [v(-465.95, -133.43) * mm, v(-467.97, -132.18) * mm, v(-467, -128.37) * mm, v(-464.05, -125.87) * mm]});
            skFitSpline(sketch, "E759", {"points": [v(-464.05, -125.87) * mm, v(-461.11, -123.4) * mm, v(-461.11, -123.4) * mm, v(-463.6, -120.92) * mm]});
            skFitSpline(sketch, "E760", {"points": [v(-463.6, -120.92) * mm, v(-464.96, -119.55) * mm, v(-466.3, -117.55) * mm, v(-466.57, -116.46) * mm]});
            skFitSpline(sketch, "E761", {"points": [v(-466.57, -116.46) * mm, v(-466.95, -114.92) * mm, v(-466.53, -52.56) * mm, v(-466.05, -38.93) * mm]});
            skFitSpline(sketch, "E762", {"points": [v(-466.05, -38.93) * mm, v(-466, -37.38) * mm, v(-466.21, -26.7) * mm, v(-466.54, -15.23) * mm]});
            skFitSpline(sketch, "E763", {"points": [v(-466.54, -15.23) * mm, v(-467.06, 3.04) * mm, v(-466.94, 5.83) * mm, v(-465.64, 7.13) * mm]});
            skFitSpline(sketch, "E764", {"points": [v(-465.64, 7.13) * mm, v(-463.83, 8.94) * mm, v(-463.8, 10.56) * mm, v(-465.51, 12.83) * mm]});
            skFitSpline(sketch, "E765", {"points": [v(-465.51, 12.83) * mm, v(-467.38, 15.3) * mm, v(-467.41, 28) * mm, v(-465.55, 29.54) * mm]});
            skFitSpline(sketch, "E766", {"points": [v(-465.55, 29.54) * mm, v(-463.74, 31.05) * mm, v(-463.75, 34.84) * mm, v(-465.57, 35.54) * mm]});
            skFitSpline(sketch, "E767", {"points": [v(-465.57, 35.54) * mm, v(-468.83, 36.8) * mm, v(-466.92, 47.52) * mm, v(-463.24, 48.61) * mm]});
            skFitSpline(sketch, "E768", {"points": [v(-463.24, 48.61) * mm, v(-462.15, 48.94) * mm, v(-462.3, 49.41) * mm, v(-463.95, 50.82) * mm]});
            skFitSpline(sketch, "E769", {"points": [v(-463.95, 50.82) * mm, v(-466.42, 52.94) * mm, v(-466.69, 56.46) * mm, v(-464.47, 57.7) * mm]});
            skFitSpline(sketch, "E770", {"points": [v(-464.47, 57.7) * mm, v(-463.04, 58.5) * mm, v(-463.08, 58.82) * mm, v(-464.94, 61.18) * mm]});
            skFitSpline(sketch, "E771", {"points": [v(-464.94, 61.18) * mm, v(-466.82, 63.57) * mm, v(-466.99, 64.87) * mm, v(-466.99, 77.3) * mm]});
            skFitSpline(sketch, "E772", {"points": [v(-466.99, 77.3) * mm, v(-466.99, 85.28) * mm, v(-466.6, 91.04) * mm, v(-466.04, 91.39) * mm]});
            skFitSpline(sketch, "E773", {"points": [v(-466.04, 91.39) * mm, v(-464.86, 92.12) * mm, v(-464.8, 97.23) * mm, v(-465.97, 97.95) * mm]});
            skFitSpline(sketch, "E774", {"points": [v(-465.97, 97.95) * mm, v(-466.46, 98.25) * mm, v(-466.75, 106.26) * mm, v(-466.64, 116.36) * mm]});
            skFitSpline(sketch, "E775", {"points": [v(-466.64, 116.36) * mm, v(-466.42, 136.11) * mm, v(-465.83, 138.13) * mm, v(-460.31, 138.13) * mm]});
            skFitSpline(sketch, "E776", {"points": [v(-460.31, 138.13) * mm, v(-458.64, 138.13) * mm, v(-456.92, 139.06) * mm, v(-455.5, 140.73) * mm]});
            skFitSpline(sketch, "E777", {"points": [v(-455.5, 140.73) * mm, v(-450.42, 146.7) * mm, v(-448.44, 147.58) * mm, v(-439.98, 147.58) * mm]});
            skFitSpline(sketch, "E778", {"points": [v(-439.98, 147.58) * mm, v(-432.5, 147.58) * mm, v(-431.96, 147.43) * mm, v(-429.21, 144.74) * mm]});
            skFitSpline(sketch, "E779", {"points": [v(-429.21, 144.74) * mm, v(-427.62, 143.18) * mm, v(-425.51, 141.9) * mm, v(-424.53, 141.9) * mm]});
            skFitSpline(sketch, "E780", {"points": [v(-424.53, 141.9) * mm, v(-420.69, 141.9) * mm, v(-419.77, 140.88) * mm, v(-419.77, 136.59) * mm]});
            skFitSpline(sketch, "E781", {"points": [v(-419.77, 136.59) * mm, v(-419.77, 133.74) * mm, v(-420.22, 132.23) * mm, v(-421.19, 131.86) * mm]});
            skFitSpline(sketch, "E782", {"points": [v(-421.19, 131.86) * mm, v(-421.96, 131.56) * mm, v(-422.6, 130.77) * mm, v(-422.6, 130.1) * mm]});
            skFitSpline(sketch, "E783", {"points": [v(-422.6, 130.1) * mm, v(-422.6, 129.44) * mm, v(-421.96, 128.65) * mm, v(-421.19, 128.35) * mm]});
            skFitSpline(sketch, "E784", {"points": [v(-421.19, 128.35) * mm, v(-420.21, 127.97) * mm, v(-419.77, 126.45) * mm, v(-419.77, 123.5) * mm]});
            skFitSpline(sketch, "E785", {"points": [v(-419.77, 123.5) * mm, v(-419.77, 120.54) * mm, v(-420.21, 119.02) * mm, v(-421.19, 118.64) * mm]});
            skFitSpline(sketch, "E786", {"points": [v(-421.19, 118.64) * mm, v(-422.99, 117.95) * mm, v(-422.99, 116.66) * mm, v(-421.17, 114.85) * mm]});
            skFitSpline(sketch, "E787", {"points": [v(-421.17, 114.85) * mm, v(-419.42, 113.1) * mm, v(-419.33, 81.2) * mm, v(-421.06, 78.43) * mm]});
            skFitSpline(sketch, "E788", {"points": [v(-421.06, 78.43) * mm, v(-421.8, 77.23) * mm, v(-421.77, 76.49) * mm, v(-420.92, 75.64) * mm]});
            skFitSpline(sketch, "E789", {"points": [v(-420.92, 75.64) * mm, v(-419.46, 74.18) * mm, v(-419.43, 70.85) * mm, v(-420.86, 69.42) * mm]});
            skFitSpline(sketch, "E790", {"points": [v(-420.86, 69.42) * mm, v(-421.59, 68.7) * mm, v(-421.64, 67.92) * mm, v(-421.04, 67.1) * mm]});
            skFitSpline(sketch, "E791", {"points": [v(-421.04, 67.1) * mm, v(-420.52, 66.42) * mm, v(-420.04, 56.62) * mm, v(-419.93, 44.64) * mm]});
            skFitSpline(sketch, "E792", {"points": [v(-419.93, 44.64) * mm, v(-419.74, 23.4) * mm, v(-419.74, 23.4) * mm, v(-416.69, 20.82) * mm]});
            skFitSpline(sketch, "E793", {"points": [v(-416.69, 20.82) * mm, v(-415, 19.4) * mm, v(-412.45, 18.24) * mm, v(-411, 18.22) * mm]});
            skFitSpline(sketch, "E794", {"points": [v(-411, 18.22) * mm, v(-409.1, 18.2) * mm, v(-408.15, 17.56) * mm, v(-407.5, 15.84) * mm]});
            skFitSpline(sketch, "E795", {"points": [v(-407.5, 15.84) * mm, v(-406.45, 13.11) * mm, v(-403.94, 12.71) * mm, v(-403.04, 15.13) * mm]});
            skFitSpline(sketch, "E796", {"points": [v(-403.04, 15.13) * mm, v(-402.12, 17.63) * mm, v(-400.84, 18.17) * mm, v(-395.8, 18.18) * mm]});
            skFitSpline(sketch, "E797", {"points": [v(-395.8, 18.18) * mm, v(-391.42, 18.2) * mm, v(-390.96, 18.46) * mm, v(-386.16, 23.63) * mm]});
            skFitSpline(sketch, "E798", {"points": [v(-386.16, 23.63) * mm, v(-382.28, 27.8) * mm, v(-381.11, 29.76) * mm, v(-381.08, 32.1) * mm]});
            skFitSpline(sketch, "E799", {"points": [v(-381.08, 32.1) * mm, v(-381.06, 34.12) * mm, v(-380.43, 35.46) * mm, v(-379.2, 36.12) * mm]});
            skFitSpline(sketch, "E800", {"points": [v(-379.2, 36.12) * mm, v(-377.68, 36.93) * mm, v(-377.38, 37.99) * mm, v(-377.54, 41.95) * mm]});
            skFitSpline(sketch, "E801", {"points": [v(-377.54, 41.95) * mm, v(-377.7, 45.56) * mm, v(-377.35, 47.04) * mm, v(-376.2, 47.77) * mm]});
            skFitSpline(sketch, "E802", {"points": [v(-376.2, 47.77) * mm, v(-374.78, 48.66) * mm, v(-374.8, 49) * mm, v(-376.43, 51.92) * mm]});
            skFitSpline(sketch, "E803", {"points": [v(-376.43, 51.92) * mm, v(-378.6, 55.79) * mm, v(-378.65, 57.12) * mm, v(-376.7, 60.9) * mm]});
            skFitSpline(sketch, "E804", {"points": [v(-376.7, 60.9) * mm, v(-375.28, 63.63) * mm, v(-375.29, 64.05) * mm, v(-376.75, 66.53) * mm]});
            skFitSpline(sketch, "E805", {"points": [v(-376.75, 66.53) * mm, v(-378.77, 69.95) * mm, v(-378, 72.31) * mm, v(-373.86, 75.48) * mm]});
            skFitSpline(sketch, "E806", {"points": [v(-373.86, 75.48) * mm, v(-371.57, 77.22) * mm, v(-370.87, 78.28) * mm, v(-371.56, 78.97) * mm]});
            skFitSpline(sketch, "E807", {"points": [v(-371.56, 78.97) * mm, v(-373.17, 80.58) * mm, v(-372.82, 95.18) * mm, v(-371.13, 96.58) * mm]});
            skFitSpline(sketch, "E808", {"points": [v(-371.13, 96.58) * mm, v(-370.35, 97.23) * mm, v(-369.72, 98.3) * mm, v(-369.72, 98.96) * mm]});
            skFitSpline(sketch, "E809", {"points": [v(-369.72, 98.96) * mm, v(-369.72, 99.62) * mm, v(-370.35, 100.4) * mm, v(-371.13, 100.7) * mm]});
            skFitSpline(sketch, "E810", {"points": [v(-371.13, 100.7) * mm, v(-371.91, 101) * mm, v(-372.55, 102.33) * mm, v(-372.55, 103.66) * mm]});
            skFitSpline(sketch, "E811", {"points": [v(-372.55, 103.66) * mm, v(-372.55, 105) * mm, v(-371.91, 106.33) * mm, v(-371.13, 106.63) * mm]});
            skFitSpline(sketch, "E812", {"points": [v(-371.13, 106.63) * mm, v(-369.23, 107.36) * mm, v(-369.35, 108.5) * mm, v(-371.55, 110.7) * mm]});
            skFitSpline(sketch, "E813", {"points": [v(-371.55, 110.7) * mm, v(-373.65, 112.79) * mm, v(-372.84, 118) * mm, v(-370.2, 119.48) * mm]});
            skFitSpline(sketch, "E814", {"points": [v(-370.2, 119.48) * mm, v(-369.11, 120.1) * mm, v(-368.77, 122.07) * mm, v(-368.77, 127.72) * mm]});
            skFitSpline(sketch, "E815", {"points": [v(-368.77, 127.72) * mm, v(-368.77, 135.16) * mm, v(-368.77, 135.16) * mm, v(-364.76, 139) * mm]});
            skFitSpline(sketch, "E816", {"points": [v(-364.76, 139) * mm, v(-360.38, 143.18) * mm, v(-358.9, 143.59) * mm, v(-355.84, 141.44) * mm]});
            skFitSpline(sketch, "E817", {"points": [v(-355.84, 141.44) * mm, v(-354.73, 140.66) * mm, v(-353.68, 140.36) * mm, v(-353.5, 140.77) * mm]});
            skFitSpline(sketch, "E818", {"points": [v(-353.5, 140.77) * mm, v(-352.78, 142.5) * mm, v(-342.88, 148.02) * mm, v(-341.03, 147.74) * mm]});
            skFitSpline(sketch, "E819", {"points": [v(-341.03, 147.74) * mm, v(-335.64, 146.9) * mm, v(-323.01, 131.18) * mm, v(-326.16, 129.23) * mm]});
            skFitSpline(sketch, "E820", {"points": [v(-326.16, 129.23) * mm, v(-327.52, 128.4) * mm, v(-328.08, 123.6) * mm, v(-326.97, 122.26) * mm]});
            skFitSpline(sketch, "E821", {"points": [v(-326.97, 122.26) * mm, v(-326.2, 121.32) * mm, v(-326.57, 120.44) * mm, v(-328.47, 118.68) * mm]});
            skFitSpline(sketch, "E822", {"points": [v(-328.47, 118.68) * mm, v(-330.27, 117) * mm, v(-331, 115.4) * mm, v(-331, 113.07) * mm]});
            skFitSpline(sketch, "E823", {"points": [v(-331, 113.07) * mm, v(-331, 111.27) * mm, v(-331.42, 109.8) * mm, v(-331.94, 109.8) * mm]});
            skFitSpline(sketch, "E824", {"points": [v(-331.94, 109.8) * mm, v(-332.46, 109.8) * mm, v(-332.89, 108.98) * mm, v(-332.89, 107.97) * mm]});
            skFitSpline(sketch, "E825", {"points": [v(-332.89, 107.97) * mm, v(-332.89, 106.96) * mm, v(-332.46, 105.87) * mm, v(-331.94, 105.55) * mm]});
            skFitSpline(sketch, "E826", {"points": [v(-331.94, 105.55) * mm, v(-330.4, 104.6) * mm, v(-330.8, 97.55) * mm, v(-332.41, 96.92) * mm]});
            skFitSpline(sketch, "E827", {"points": [v(-332.41, 96.92) * mm, v(-333.2, 96.62) * mm, v(-333.83, 95.36) * mm, v(-333.83, 94.12) * mm]});
            skFitSpline(sketch, "E828", {"points": [v(-333.83, 94.12) * mm, v(-333.83, 92.74) * mm, v(-333.28, 91.86) * mm, v(-332.41, 91.86) * mm]});
            skFitSpline(sketch, "E829", {"points": [v(-332.41, 91.86) * mm, v(-330.77, 91.86) * mm, v(-330.71, 91.5) * mm, v(-330.98, 83.5) * mm]});
            skFitSpline(sketch, "E830", {"points": [v(-330.98, 83.5) * mm, v(-331.16, 78.07) * mm, v(-330.93, 77.25) * mm, v(-328.5, 74.7) * mm]});
            skFitSpline(sketch, "E831", {"points": [v(-328.5, 74.7) * mm, v(-324.24, 70.28) * mm, v(-324.16, 38.4) * mm, v(-328.39, 34.17) * mm]});
            skFitSpline(sketch, "E832", {"points": [v(-328.39, 34.17) * mm, v(-331.12, 31.44) * mm, v(-331.12, 31.44) * mm, v(-330.9, 20.14) * mm]});
            skFitSpline(sketch, "E833", {"points": [v(-330.9, 20.14) * mm, v(-330.78, 13.1) * mm, v(-331.08, 8.38) * mm, v(-331.72, 7.6) * mm]});
            skFitSpline(sketch, "E834", {"points": [v(-331.72, 7.6) * mm, v(-332.46, 6.72) * mm, v(-332.4, 4.89) * mm, v(-331.5, 1.01) * mm]});
            skFitSpline(sketch, "E835", {"points": [v(-331.5, 1.01) * mm, v(-330.81, -1.94) * mm, v(-330.41, -4.51) * mm, v(-330.61, -4.71) * mm]});
            skFitSpline(sketch, "E836", {"points": [v(-330.61, -4.71) * mm, v(-330.81, -4.91) * mm, v(-330.96, -13.33) * mm, v(-330.94, -23.42) * mm]});
            skFitSpline(sketch, "E837", {"points": [v(-330.94, -23.42) * mm, v(-330.91, -33.51) * mm, v(-330.94, -43.8) * mm, v(-331, -46.28) * mm]});
            skFitSpline(sketch, "E838", {"points": [v(-331, -46.28) * mm, v(-331.08, -50) * mm, v(-330.59, -51.4) * mm, v(-328.21, -54.28) * mm]});
            skFitSpline(sketch, "E839", {"points": [v(-328.21, -54.28) * mm, v(-324.64, -58.62) * mm, v(-324.64, -59.4) * mm, v(-328.17, -63.02) * mm]});
            skFitSpline(sketch, "E840", {"points": [v(-328.17, -63.02) * mm, v(-331, -65.91) * mm, v(-331, -65.91) * mm, v(-331, -83.82) * mm]});
            skFitSpline(sketch, "E841", {"points": [v(-331, -83.82) * mm, v(-331, -94.65) * mm, v(-330.64, -101.73) * mm, v(-330.1, -101.73) * mm]});
            skFitSpline(sketch, "E842", {"points": [v(-330.1, -101.73) * mm, v(-324.35, -101.73) * mm, v(-323.6, -121.77) * mm, v(-329.15, -126.8) * mm]});
            skFitSpline(sketch, "E843", {"points": [v(-329.15, -126.8) * mm, v(-330.8, -128.28) * mm, v(-331, -129.74) * mm, v(-331, -140.03) * mm]});
            skFitSpline(sketch, "E844", {"points": [v(-331, -140.03) * mm, v(-331, -149.23) * mm, v(-331.28, -151.7) * mm, v(-332.36, -152.1) * mm]});
            skFitSpline(sketch, "E845", {"points": [v(-332.36, -152.1) * mm, v(-333.11, -152.4) * mm, v(-334.24, -154.36) * mm, v(-334.88, -156.47) * mm]});
            skFitSpline(sketch, "E846", {"points": [v(-334.88, -156.47) * mm, v(-336.55, -162.06) * mm, v(-337.32, -162.4) * mm, v(-347.75, -162.03) * mm]});
            skFitSpline(sketch, "E847", {"points": [v(-347.75, -162.03) * mm, v(-357, -161.7) * mm, v(-357, -161.7) * mm, v(-364.54, -154.16) * mm]});
            skFitSpline(sketch, "E848", {"points": [v(-364.54, -154.16) * mm, v(-372.08, -146.63) * mm, v(-372.08, -146.63) * mm, v(-372.4, -135.15) * mm]});
            skFitSpline(sketch, "E849", {"points": [v(-372.4, -135.15) * mm, v(-372.56, -128.84) * mm, v(-372.28, -122.14) * mm, v(-371.76, -120.27) * mm]});
            skFitSpline(sketch, "E850", {"points": [v(-371.76, -120.27) * mm, v(-371.2, -118.22) * mm, v(-371.16, -116.65) * mm, v(-371.69, -116.32) * mm]});
            skFitSpline(sketch, "E851", {"points": [v(-371.69, -116.32) * mm, v(-372.18, -116.02) * mm, v(-372.55, -104.76) * mm, v(-372.55, -90.35) * mm]});
            skFitSpline(sketch, "E852", {"points": [v(-372.55, -90.35) * mm, v(-372.55, -66.16) * mm, v(-372.46, -64.81) * mm, v(-370.66, -63.02) * mm]});
            skFitSpline(sketch, "E853", {"points": [v(-370.66, -63.02) * mm, v(-367.88, -60.23) * mm, v(-367.9, -48.04) * mm, v(-370.7, -45.51) * mm]});
            skFitSpline(sketch, "E854", {"points": [v(-370.7, -45.51) * mm, v(-372.15, -44.2) * mm, v(-372.57, -42.78) * mm, v(-372.41, -39.69) * mm]});
            skFitSpline(sketch, "E855", {"points": [v(-372.41, -39.69) * mm, v(-372.17, -34.98) * mm, v(-373.05, -33.79) * mm, v(-377.42, -32.9) * mm]});
            skFitSpline(sketch, "E856", {"points": [v(-377.42, -32.9) * mm, v(-380.14, -32.35) * mm, v(-380.62, -31.82) * mm, v(-380.88, -29.17) * mm]});
            skFitSpline(sketch, "E857", {"points": [v(-380.88, -29.17) * mm, v(-381.25, -25.4) * mm, v(-384.4, -23.5) * mm, v(-387.54, -25.18) * mm]});
            skFitSpline(sketch, "E858", {"points": [v(-387.54, -25.18) * mm, v(-390.14, -26.57) * mm, v(-393.33, -24.98) * mm, v(-393.33, -22.3) * mm]});
            skFitSpline(sketch, "E859", {"points": [v(-393.33, -22.3) * mm, v(-393.33, -20.08) * mm, v(-393.04, -20) * mm, v(-400.18, -24.15) * mm]});
            skFitSpline(sketch, "E860", {"points": [v(-400.18, -24.15) * mm, v(-403.16, -25.89) * mm, v(-406.47, -28.52) * mm, v(-407.52, -30) * mm]});
            skFitSpline(sketch, "E861", {"points": [v(-407.52, -30) * mm, v(-408.57, -31.48) * mm, v(-410.37, -32.98) * mm, v(-411.52, -33.35) * mm]});
            skFitSpline(sketch, "E862", {"points": [v(-411.52, -33.35) * mm, v(-412.67, -33.71) * mm, v(-415.01, -35.33) * mm, v(-416.73, -36.94) * mm]});
            skFitSpline(sketch, "E863", {"points": [v(-416.73, -36.94) * mm, v(-419.85, -39.88) * mm, v(-419.85, -39.88) * mm, v(-419.8, -57.35) * mm]});
            skFitSpline(sketch, "E864", {"points": [v(-419.8, -57.35) * mm, v(-419.54, -139.75) * mm, v(-419.62, -141.56) * mm, v(-424, -145.84) * mm]});
            skFitSpline(sketch, "E865", {"points": [v(-424, -145.84) * mm, v(-426.49, -148.28) * mm, v(-428.27, -151) * mm, v(-428.63, -152.92) * mm]});
            skFitSpline(sketch, "E866", {"points": [v(-428.63, -152.92) * mm, v(-429.89, -159.55) * mm, v(-433.93, -162.17) * mm, v(-442.92, -162.17) * mm]});
            skFitSpline(sketch, "E867", {"points": [v(-442.92, -162.17) * mm, v(-449.9, -162.17) * mm, v(-451, -161.94) * mm, v(-451.88, -160.28) * mm]});
            skFitSpline(sketch, "E868", {"points": [v(-22.27, -160.22) * mm, v(-23.5, -159.14) * mm, v(-25.7, -158.03) * mm, v(-27.12, -157.74) * mm]});
            skFitSpline(sketch, "E869", {"points": [v(-27.12, -157.74) * mm, v(-28.73, -157.42) * mm, v(-32.65, -154.19) * mm, v(-37.52, -149.17) * mm]});
            skFitSpline(sketch, "E870", {"points": [v(-37.52, -149.17) * mm, v(-41.81, -144.75) * mm, v(-46.35, -140.23) * mm, v(-47.59, -139.14) * mm]});
            skFitSpline(sketch, "E871", {"points": [v(-47.59, -139.14) * mm, v(-54.03, -133.47) * mm, v(-55.24, -131.39) * mm, v(-53.26, -129.4) * mm]});
            skFitSpline(sketch, "E872", {"points": [v(-53.26, -129.4) * mm, v(-51.95, -128.1) * mm, v(-54.1, -121.57) * mm, v(-55.85, -121.57) * mm]});
            skFitSpline(sketch, "E873", {"points": [v(-55.85, -121.57) * mm, v(-58.79, -121.57) * mm, v(-60.02, -106.5) * mm, v(-57.3, -103.8) * mm]});
            skFitSpline(sketch, "E874", {"points": [v(-60.34, -95.17) * mm, v(-64.5, -91.2) * mm, v(-64.64, -88.6) * mm, v(-60.91, -84.88) * mm]});
            skFitSpline(sketch, "E875", {"points": [v(-60.91, -84.88) * mm, v(-59.35, -83.32) * mm, v(-58.08, -81.46) * mm, v(-58.08, -80.74) * mm]});
            skFitSpline(sketch, "E876", {"points": [v(-60.91, -76.7) * mm, v(-64.9, -72.89) * mm, v(-65.2, -62.12) * mm, v(-61.38, -59.62) * mm]});
            skFitSpline(sketch, "E877", {"points": [v(-61.38, -59.62) * mm, v(-58.42, -57.68) * mm, v(-58.38, -55.76) * mm, v(-61.27, -53.5) * mm]});
            skFitSpline(sketch, "E878", {"points": [v(-61.27, -53.5) * mm, v(-64.7, -50.79) * mm, v(-64.52, -44.67) * mm, v(-60.9, -41.28) * mm]});
            skFitSpline(sketch, "E879", {"points": [v(-60.9, -41.28) * mm, v(-58.16, -38.73) * mm, v(-58.16, -38.73) * mm, v(-60.95, -36.06) * mm]});
            skFitSpline(sketch, "E880", {"points": [v(-60.95, -36.06) * mm, v(-63.94, -33.2) * mm, v(-64.43, -30.48) * mm, v(-62.42, -27.84) * mm]});
            skFitSpline(sketch, "E881", {"points": [v(-62.42, -27.84) * mm, v(-61.39, -26.48) * mm, v(-61.4, -25.36) * mm, v(-62.45, -21.26) * mm]});
            skFitSpline(sketch, "E882", {"points": [v(-62.45, -21.26) * mm, v(-64.04, -15.13) * mm, v(-64.12, -4.11) * mm, v(-62.58, -1.66) * mm]});
            skFitSpline(sketch, "E883", {"points": [v(-62.58, -1.66) * mm, v(-61.68, -0.22) * mm, v(-61.68, 0.86) * mm, v(-62.58, 3.35) * mm]});
            skFitSpline(sketch, "E884", {"points": [v(-62.58, 3.35) * mm, v(-63.98, 7.2) * mm, v(-64.06, 10.33) * mm, v(-62.79, 11.12) * mm]});
            skFitSpline(sketch, "E885", {"points": [v(-62.8, 17.73) * mm, v(-64.08, 18.53) * mm, v(-64, 64.2) * mm, v(-62.71, 65) * mm]});
            skFitSpline(sketch, "E886", {"points": [v(-62.71, 65) * mm, v(-62.12, 65.37) * mm, v(-62.1, 65.99) * mm, v(-62.66, 66.68) * mm]});
            skFitSpline(sketch, "E887", {"points": [v(-62.66, 66.68) * mm, v(-63.15, 67.29) * mm, v(-63.6, 77.8) * mm, v(-63.68, 90.26) * mm]});
            skFitSpline(sketch, "E888", {"points": [v(-63.68, 90.26) * mm, v(-63.75, 105.5) * mm, v(-64.16, 113.3) * mm, v(-64.9, 114.5) * mm]});
            skFitSpline(sketch, "E889", {"points": [v(-64.9, 114.5) * mm, v(-65.83, 115.98) * mm, v(-65.46, 116.9) * mm, v(-62.63, 120.36) * mm]});
            skFitSpline(sketch, "E890", {"points": [v(-62.63, 120.36) * mm, v(-59.9, 123.7) * mm, v(-59.14, 125.56) * mm, v(-58.58, 130.38) * mm]});
            skFitSpline(sketch, "E891", {"points": [v(-58.58, 130.38) * mm, v(-57.93, 135.98) * mm, v(-57.65, 136.5) * mm, v(-53.3, 140.17) * mm]});
            skFitSpline(sketch, "E892", {"points": [v(-53.3, 140.17) * mm, v(-50.76, 142.3) * mm, v(-48.44, 144.85) * mm, v(-48.13, 145.82) * mm]});
            skFitSpline(sketch, "E893", {"points": [v(-48.13, 145.82) * mm, v(-47.65, 147.33) * mm, v(-46.56, 147.58) * mm, v(-40.23, 147.58) * mm]});
            skFitSpline(sketch, "E894", {"points": [v(-40.23, 147.58) * mm, v(-32.88, 147.58) * mm, v(-32.88, 147.58) * mm, v(-28.9, 142.85) * mm]});
            skFitSpline(sketch, "E895", {"points": [v(-28.9, 142.85) * mm, v(-25.56, 138.9) * mm, v(-24.4, 138.13) * mm, v(-21.7, 138.13) * mm]});
            skFitSpline(sketch, "E896", {"points": [v(-21.7, 138.13) * mm, v(-18.16, 138.13) * mm, v(-16.54, 136.22) * mm, v(-16.54, 132.03) * mm]});
            skFitSpline(sketch, "E897", {"points": [v(-16.54, 132.03) * mm, v(-16.54, 130.3) * mm, v(-15.85, 129.33) * mm, v(-14.17, 128.69) * mm]});
            skFitSpline(sketch, "E898", {"points": [v(-14.17, 128.69) * mm, v(-11.45, 127.65) * mm, v(-11.28, 126.92) * mm, v(-13.2, 124.38) * mm]});
            skFitSpline(sketch, "E899", {"points": [v(-13.2, 124.38) * mm, v(-14.97, 122.05) * mm, v(-15.04, 119.25) * mm, v(-13.33, 119.25) * mm]});
            skFitSpline(sketch, "E900", {"points": [v(-13.33, 119.25) * mm, v(-12.22, 119.25) * mm, v(-10.87, 117.37) * mm, v(-10.87, 115.83) * mm]});
            skFitSpline(sketch, "E901", {"points": [v(-10.87, 115.83) * mm, v(-10.87, 115.6) * mm, v(-12.1, 114.2) * mm, v(-13.62, 112.71) * mm]});
            skFitSpline(sketch, "E902", {"points": [v(-13.62, 112.71) * mm, v(-16.37, 110.02) * mm, v(-16.37, 110.02) * mm, v(-16.65, 94.36) * mm]});
            skFitSpline(sketch, "E903", {"points": [v(-16.65, 94.36) * mm, v(-16.92, 79.15) * mm, v(-16.86, 78.64) * mm, v(-14.76, 76.4) * mm]});
            skFitSpline(sketch, "E904", {"points": [v(-14.76, 76.4) * mm, v(-11.5, 72.92) * mm, v(-10.92, 68.6) * mm, v(-10.88, 47.47) * mm]});
            skFitSpline(sketch, "E905", {"points": [v(-10.88, 47.47) * mm, v(-10.86, 28.11) * mm, v(-10.86, 28.11) * mm, v(-13.93, 25.57) * mm]});
            skFitSpline(sketch, "E906", {"points": [v(-13.93, 25.57) * mm, v(-16.6, 23.36) * mm, v(-16.86, 22.78) * mm, v(-15.88, 21.18) * mm]});
            skFitSpline(sketch, "E907", {"points": [v(-15.88, 21.18) * mm, v(-14.95, 19.66) * mm, v(-15.07, 19.06) * mm, v(-16.59, 17.68) * mm]});
            skFitSpline(sketch, "E908", {"points": [v(-16.59, 17.68) * mm, v(-18.49, 15.95) * mm, v(-19.13, 11.59) * mm, v(-17.47, 11.59) * mm]});
            skFitSpline(sketch, "E909", {"points": [v(-17.47, 11.59) * mm, v(-16.9, 11.59) * mm, v(-16.53, 7.66) * mm, v(-16.53, 1.7) * mm]});
            skFitSpline(sketch, "E910", {"points": [v(-16.53, 1.7) * mm, v(-16.53, -8.2) * mm, v(-16.53, -8.2) * mm, v(-13.7, -9.66) * mm]});
            skFitSpline(sketch, "E911", {"points": [v(-13.7, -9.66) * mm, v(-10.38, -11.37) * mm, v(-10.38, -11.38) * mm, v(-12.46, -14.9) * mm]});
            skFitSpline(sketch, "E912", {"points": [v(-12.46, -14.9) * mm, v(-13.97, -17.47) * mm, v(-13.97, -17.71) * mm, v(-12.33, -19.52) * mm]});
            skFitSpline(sketch, "E913", {"points": [v(-12.33, -19.52) * mm, v(-10.49, -21.55) * mm, v(-11.56, -24.3) * mm, v(-14.2, -24.3) * mm]});
            skFitSpline(sketch, "E914", {"points": [v(-14.2, -24.3) * mm, v(-16.06, -24.3) * mm, v(-14.74, -27.83) * mm, v(-12.66, -28.37) * mm]});
            skFitSpline(sketch, "E915", {"points": [v(-12.66, -28.37) * mm, v(-10.5, -28.94) * mm, v(-10.36, -30.27) * mm, v(-12.28, -32.19) * mm]});
            skFitSpline(sketch, "E916", {"points": [v(-12.28, -32.19) * mm, v(-14.14, -34.05) * mm, v(-14.08, -36.56) * mm, v(-12.15, -37.97) * mm]});
            skFitSpline(sketch, "E917", {"points": [v(-12.15, -37.97) * mm, v(-10.77, -38.98) * mm, v(-10.7, -40.33) * mm, v(-11.54, -50.34) * mm]});
            skFitSpline(sketch, "E918", {"points": [v(-11.54, -50.34) * mm, v(-12.14, -57.6) * mm, v(-12.15, -62.75) * mm, v(-11.56, -64.89) * mm]});
            skFitSpline(sketch, "E919", {"points": [v(-11.56, -64.89) * mm, v(-11.06, -66.7) * mm, v(-10.84, -73.5) * mm, v(-11.09, -80) * mm]});
            skFitSpline(sketch, "E920", {"points": [v(-11.09, -80) * mm, v(-11.49, -90.85) * mm, v(-11.37, -92) * mm, v(-9.63, -93.92) * mm]});
            skFitSpline(sketch, "E921", {"points": [v(-9.63, -93.92) * mm, v(-8.35, -95.34) * mm, v(-7.65, -97.62) * mm, v(-7.48, -100.92) * mm]});
            skFitSpline(sketch, "E922", {"points": [v(-7.48, -100.92) * mm, v(-7.26, -105.36) * mm, v(-6.86, -106.13) * mm, v(-3.15, -109.43) * mm]});
            skFitSpline(sketch, "E923", {"points": [v(-3.15, -109.43) * mm, v(0.75, -112.89) * mm, v(4.25, -114.16) * mm, v(4.25, -112.12) * mm]});
            skFitSpline(sketch, "E924", {"points": [v(4.25, -112.12) * mm, v(4.25, -111.6) * mm, v(5.96, -111.18) * mm, v(8.05, -111.18) * mm]});
            skFitSpline(sketch, "E925", {"points": [v(8.05, -111.18) * mm, v(11.18, -111.18) * mm, v(12.03, -110.77) * mm, v(12.92, -108.82) * mm]});
            skFitSpline(sketch, "E926", {"points": [v(12.92, -108.82) * mm, v(13.7, -107.12) * mm, v(14.74, -106.46) * mm, v(16.65, -106.46) * mm]});
            skFitSpline(sketch, "E927", {"points": [v(16.65, -106.46) * mm, v(21.5, -106.46) * mm, v(32.05, -95.66) * mm, v(29.9, -92.88) * mm]});
            skFitSpline(sketch, "E928", {"points": [v(29.9, -92.88) * mm, v(28.75, -91.37) * mm, v(29.35, -73.42) * mm, v(30.6, -72.17) * mm]});
            skFitSpline(sketch, "E929", {"points": [v(30.6, -72.17) * mm, v(32.06, -70.7) * mm, v(31.88, -68.18) * mm, v(30.22, -66.8) * mm]});
            skFitSpline(sketch, "E930", {"points": [v(30.22, -66.8) * mm, v(29.44, -66.15) * mm, v(28.8, -64.66) * mm, v(28.8, -63.49) * mm]});
            skFitSpline(sketch, "E931", {"points": [v(28.8, -63.49) * mm, v(28.8, -62.32) * mm, v(29.44, -60.83) * mm, v(30.22, -60.18) * mm]});
            skFitSpline(sketch, "E932", {"points": [v(30.22, -60.18) * mm, v(31, -59.54) * mm, v(31.64, -57.83) * mm, v(31.64, -56.4) * mm]});
            skFitSpline(sketch, "E933", {"points": [v(31.64, -56.4) * mm, v(31.64, -54.94) * mm, v(31, -53.53) * mm, v(30.22, -53.23) * mm]});
            skFitSpline(sketch, "E934", {"points": [v(30.22, -53.23) * mm, v(28.4, -52.54) * mm, v(28.4, -48.8) * mm, v(30.2, -46.43) * mm]});
            skFitSpline(sketch, "E935", {"points": [v(30.2, -46.43) * mm, v(32.12, -43.9) * mm, v(32.1, -33.93) * mm, v(30.18, -31.8) * mm]});
            skFitSpline(sketch, "E936", {"points": [v(30.18, -31.8) * mm, v(28.86, -30.35) * mm, v(28.86, -30.05) * mm, v(30.18, -28.73) * mm]});
            skFitSpline(sketch, "E937", {"points": [v(30.18, -28.73) * mm, v(31.9, -27.01) * mm, v(32.08, -24.17) * mm, v(30.58, -22.67) * mm]});
            skFitSpline(sketch, "E938", {"points": [v(30.58, -22.67) * mm, v(28.67, -20.76) * mm, v(28.93, -3.4) * mm, v(30.9, -1.42) * mm]});
            skFitSpline(sketch, "E939", {"points": [v(30.9, -1.42) * mm, v(33.34, 1.01) * mm, v(33.16, 7) * mm, v(30.6, 8.6) * mm]});
            skFitSpline(sketch, "E940", {"points": [v(30.6, 8.6) * mm, v(29, 9.6) * mm, v(28.73, 10.41) * mm, v(29.23, 12.84) * mm]});
            skFitSpline(sketch, "E941", {"points": [v(29.23, 12.84) * mm, v(30.72, 20.1) * mm, v(30.83, 21.79) * mm, v(29.84, 22.4) * mm]});
            skFitSpline(sketch, "E942", {"points": [v(29.84, 22.4) * mm, v(28.37, 23.3) * mm, v(28.56, 26.96) * mm, v(30.2, 29.11) * mm]});
            skFitSpline(sketch, "E943", {"points": [v(30.2, 29.11) * mm, v(31.85, 31.3) * mm, v(32.07, 34.9) * mm, v(30.58, 35.4) * mm]});
            skFitSpline(sketch, "E944", {"points": [v(30.58, 35.4) * mm, v(29.7, 35.69) * mm, v(29, 65.45) * mm, v(29.8, 68.96) * mm]});
            skFitSpline(sketch, "E945", {"points": [v(29.8, 68.96) * mm, v(30.25, 70.98) * mm, v(29.9, 78.59) * mm, v(29.3, 79.54) * mm]});
            skFitSpline(sketch, "E946", {"points": [v(29.3, 79.54) * mm, v(28.93, 80.15) * mm, v(29.25, 81.36) * mm, v(30, 82.24) * mm]});
            skFitSpline(sketch, "E947", {"points": [v(30, 82.24) * mm, v(32.28, 84.88) * mm, v(32.52, 87.67) * mm, v(30.57, 88.89) * mm]});
            skFitSpline(sketch, "E948", {"points": [v(30.57, 88.89) * mm, v(28.45, 90.2) * mm, v(28.26, 94) * mm, v(30.23, 95.64) * mm]});
            skFitSpline(sketch, "E949", {"points": [v(30.23, 95.64) * mm, v(31.89, 97.01) * mm, v(32.07, 99.55) * mm, v(30.62, 101) * mm]});
            skFitSpline(sketch, "E950", {"points": [v(30.62, 101) * mm, v(30, 101.61) * mm, v(29.53, 106.78) * mm, v(29.44, 113.7) * mm]});
            skFitSpline(sketch, "E951", {"points": [v(29.44, 113.7) * mm, v(29.28, 125.38) * mm, v(29.28, 125.38) * mm, v(35.52, 131.76) * mm]});
            skFitSpline(sketch, "E952", {"points": [v(35.52, 131.76) * mm, v(39.3, 135.62) * mm, v(42.54, 138.13) * mm, v(43.74, 138.13) * mm]});
            skFitSpline(sketch, "E953", {"points": [v(43.74, 138.13) * mm, v(44.83, 138.13) * mm, v(47.33, 139.22) * mm, v(49.3, 140.56) * mm]});
            skFitSpline(sketch, "E954", {"points": [v(49.3, 140.56) * mm, v(52.07, 142.44) * mm, v(53.56, 142.85) * mm, v(55.99, 142.4) * mm]});
            skFitSpline(sketch, "E955", {"points": [v(55.99, 142.4) * mm, v(58.66, 141.9) * mm, v(59.48, 142.22) * mm, v(61.64, 144.7) * mm]});
            skFitSpline(sketch, "E956", {"points": [v(61.64, 144.7) * mm, v(65.33, 148.9) * mm, v(68.25, 148.54) * mm, v(73.05, 143.27) * mm]});
            skFitSpline(sketch, "E957", {"points": [v(73.05, 143.27) * mm, v(75.2, 140.9) * mm, v(76.97, 138.63) * mm, v(76.97, 138.22) * mm]});
            skFitSpline(sketch, "E958", {"points": [v(76.97, 138.22) * mm, v(76.97, 137.82) * mm, v(78.05, 137) * mm, v(79.38, 136.4) * mm]});
            skFitSpline(sketch, "E959", {"points": [v(79.38, 136.4) * mm, v(81.78, 135.3) * mm, v(81.78, 135.3) * mm, v(81.6, 115) * mm]});
            skFitSpline(sketch, "E960", {"points": [v(81.6, 115) * mm, v(81.43, 97.27) * mm, v(81.6, 94.46) * mm, v(82.97, 92.96) * mm]});
            skFitSpline(sketch, "E961", {"points": [v(82.97, 92.96) * mm, v(84.9, 90.81) * mm, v(84.98, 88.2) * mm, v(83.1, 87.48) * mm]});
            skFitSpline(sketch, "E962", {"points": [v(83.1, 87.48) * mm, v(82.3, 87.17) * mm, v(81.7, 85.76) * mm, v(81.7, 84.2) * mm]});
            skFitSpline(sketch, "E963", {"points": [v(81.7, 84.2) * mm, v(81.7, 82.7) * mm, v(81.25, 81.47) * mm, v(80.7, 81.47) * mm]});
            skFitSpline(sketch, "E964", {"points": [v(80.7, 81.47) * mm, v(80.1, 81.47) * mm, v(79.95, 80.26) * mm, v(80.31, 78.3) * mm]});
            skFitSpline(sketch, "E965", {"points": [v(80.31, 78.3) * mm, v(80.82, 75.62) * mm, v(80.52, 74.82) * mm, v(78.43, 73.18) * mm]});
            skFitSpline(sketch, "E966", {"points": [v(78.43, 73.18) * mm, v(75.97, 71.24) * mm, v(75.95, 71.16) * mm, v(76.08, 58.64) * mm]});
            skFitSpline(sketch, "E967", {"points": [v(76.08, 58.64) * mm, v(76.13, 51.72) * mm, v(76.1, 45.63) * mm, v(76, 45.11) * mm]});
            skFitSpline(sketch, "E968", {"points": [v(76, 45.11) * mm, v(75.47, 42.5) * mm, v(76.26, 40.73) * mm, v(78.3, 39.95) * mm]});
            skFitSpline(sketch, "E969", {"points": [v(78.3, 39.95) * mm, v(81.33, 38.8) * mm, v(82.3, 37.04) * mm, v(80.63, 35.76) * mm]});
            skFitSpline(sketch, "E970", {"points": [v(80.63, 35.76) * mm, v(79.32, 34.76) * mm, v(79.33, 31.94) * mm, v(80.66, 30) * mm]});
            skFitSpline(sketch, "E971", {"points": [v(80.66, 30) * mm, v(81.02, 29.48) * mm, v(81.18, 25.02) * mm, v(81.02, 20.09) * mm]});
            skFitSpline(sketch, "E972", {"points": [v(81.02, 20.09) * mm, v(80.87, 15.15) * mm, v(80.75, 9.15) * mm, v(80.77, 6.74) * mm]});
            skFitSpline(sketch, "E973", {"points": [v(80.77, 6.74) * mm, v(80.8, 2.83) * mm, v(80.54, 2.3) * mm, v(78.42, 1.76) * mm]});
            skFitSpline(sketch, "E974", {"points": [v(78.42, 1.76) * mm, v(76.1, 1.18) * mm, v(75.1, -3.6) * mm, v(75.91, -10.13) * mm]});
            skFitSpline(sketch, "E975", {"points": [v(75.91, -10.13) * mm, v(76.65, -15.97) * mm, v(76.06, -34.23) * mm, v(75.06, -36.65) * mm]});
            skFitSpline(sketch, "E976", {"points": [v(75.06, -36.65) * mm, v(74.17, -38.8) * mm, v(74.14, -39.78) * mm, v(74.95, -40.6) * mm]});
            skFitSpline(sketch, "E977", {"points": [v(74.95, -40.6) * mm, v(76.34, -41.98) * mm, v(76.33, -44.62) * mm, v(74.94, -46.84) * mm]});
            skFitSpline(sketch, "E978", {"points": [v(74.94, -46.84) * mm, v(74.08, -48.22) * mm, v(74.18, -49.06) * mm, v(75.42, -50.82) * mm]});
            skFitSpline(sketch, "E979", {"points": [v(75.42, -50.82) * mm, v(77.5, -53.79) * mm, v(77.39, -55.63) * mm, v(74.93, -58.75) * mm]});
            skFitSpline(sketch, "E980", {"points": [v(74.93, -58.75) * mm, v(73.07, -61.12) * mm, v(73.03, -61.43) * mm, v(74.46, -62.23) * mm]});
            skFitSpline(sketch, "E981", {"points": [v(74.46, -62.23) * mm, v(76.26, -63.24) * mm, v(76.55, -66.84) * mm, v(74.95, -68.44) * mm]});
            skFitSpline(sketch, "E982", {"points": [v(74.95, -68.44) * mm, v(74.15, -69.25) * mm, v(74.23, -70.3) * mm, v(75.3, -72.64) * mm]});
            skFitSpline(sketch, "E983", {"points": [v(75.3, -72.64) * mm, v(76.38, -75.05) * mm, v(76.58, -77.82) * mm, v(76.13, -84.74) * mm]});
            skFitSpline(sketch, "E984", {"points": [v(76.13, -84.74) * mm, v(75.82, -89.67) * mm, v(75.79, -95.67) * mm, v(76.07, -98.07) * mm]});
            skFitSpline(sketch, "E985", {"points": [v(76.07, -98.07) * mm, v(76.67, -103.26) * mm, v(75.56, -108.23) * mm, v(73.64, -108.96) * mm]});
            skFitSpline(sketch, "E986", {"points": [v(73.64, -108.96) * mm, v(72.6, -109.36) * mm, v(72.27, -111.24) * mm, v(72.27, -116.57) * mm]});
            skFitSpline(sketch, "E987", {"points": [v(72.27, -116.57) * mm, v(72.27, -123.66) * mm, v(72.27, -123.66) * mm, v(67.54, -128.09) * mm]});
            skFitSpline(sketch, "E988", {"points": [v(67.54, -128.09) * mm, v(63.53, -131.86) * mm, v(62.82, -133.04) * mm, v(62.82, -136.02) * mm]});
            skFitSpline(sketch, "E989", {"points": [v(62.82, -136.02) * mm, v(62.82, -138.85) * mm, v(62.47, -139.5) * mm, v(60.98, -139.5) * mm]});
            skFitSpline(sketch, "E990", {"points": [v(60.98, -139.5) * mm, v(57.69, -139.5) * mm, v(54.32, -141.6) * mm, v(54.3, -143.67) * mm]});
            skFitSpline(sketch, "E991", {"points": [v(54.3, -143.67) * mm, v(54.26, -146.28) * mm, v(52.15, -148.95) * mm, v(50.14, -148.95) * mm]});
            skFitSpline(sketch, "E992", {"points": [v(50.14, -148.95) * mm, v(47.27, -148.95) * mm, v(44.88, -150.85) * mm, v(44.88, -153.13) * mm]});
            skFitSpline(sketch, "E993", {"points": [v(44.88, -153.13) * mm, v(44.88, -154.5) * mm, v(43.5, -156.6) * mm, v(41.23, -158.64) * mm]});
            skFitSpline(sketch, "E994", {"points": [v(41.23, -158.64) * mm, v(37.57, -161.94) * mm, v(37.57, -161.94) * mm, v(8.8, -162.06) * mm]});
            skFitSpline(sketch, "E995", {"points": [v(8.8, -162.06) * mm, v(-19.06, -162.17) * mm, v(-20.06, -162.11) * mm, v(-22.25, -160.22) * mm]});
            skFitSpline(sketch, "E996", {"points": [v(526.87, -156.12) * mm, v(520.81, -150.07) * mm, v(520.81, -150.07) * mm, v(520.81, -129.9) * mm]});
            skFitSpline(sketch, "E997", {"points": [v(520.81, -129.9) * mm, v(520.81, -111.68) * mm, v(520.65, -109.57) * mm, v(519.13, -108.26) * mm]});
            skFitSpline(sketch, "E998", {"points": [v(519.13, -108.26) * mm, v(516.98, -106.42) * mm, v(516.14, -35.16) * mm, v(518.23, -31.8) * mm]});
            skFitSpline(sketch, "E999", {"points": [v(518.23, -31.8) * mm, v(519.08, -30.45) * mm, v(519.1, -29.53) * mm, v(518.34, -28.3) * mm]});
            skFitSpline(sketch, "E1000", {"points": [v(518.34, -28.3) * mm, v(517.42, -26.82) * mm, v(516.48, 26.2) * mm, v(517, 47.97) * mm]});
            skFitSpline(sketch, "E1001", {"points": [v(517, 47.97) * mm, v(517.13, 53.96) * mm, v(516.93, 54.81) * mm, v(514.73, 56.87) * mm]});
            skFitSpline(sketch, "E1002", {"points": [v(514.73, 56.87) * mm, v(511.41, 59.98) * mm, v(511.37, 66.03) * mm, v(514.63, 69.91) * mm]});
            skFitSpline(sketch, "E1003", {"points": [v(514.63, 69.91) * mm, v(517.96, 73.87) * mm, v(518.49, 97.82) * mm, v(515.3, 100.28) * mm]});
            skFitSpline(sketch, "E1004", {"points": [v(515.3, 100.28) * mm, v(510.72, 103.8) * mm, v(510.18, 110.81) * mm, v(514.2, 114.35) * mm]});
            skFitSpline(sketch, "E1005", {"points": [v(514.2, 114.35) * mm, v(516.6, 116.45) * mm, v(517.04, 117.52) * mm, v(517.04, 121.27) * mm]});
            skFitSpline(sketch, "E1006", {"points": [v(517.04, 121.27) * mm, v(517.04, 124.52) * mm, v(517.63, 126.43) * mm, v(519.22, 128.38) * mm]});
            skFitSpline(sketch, "E1007", {"points": [v(519.22, 128.38) * mm, v(520.43, 129.85) * mm, v(522, 132.54) * mm, v(522.7, 134.36) * mm]});
            skFitSpline(sketch, "E1008", {"points": [v(522.7, 134.36) * mm, v(524.3, 138.43) * mm, v(532.27, 146.22) * mm, v(535.73, 147.09) * mm]});
            skFitSpline(sketch, "E1009", {"points": [v(535.73, 147.09) * mm, v(537.14, 147.44) * mm, v(539.07, 148.43) * mm, v(540.03, 149.3) * mm]});
            skFitSpline(sketch, "E1010", {"points": [v(540.03, 149.3) * mm, v(543, 151.97) * mm, v(562.7, 152.16) * mm, v(566.23, 149.55) * mm]});
            skFitSpline(sketch, "E1011", {"points": [v(566.23, 149.55) * mm, v(567.7, 148.46) * mm, v(570.17, 147.58) * mm, v(571.72, 147.58) * mm]});
            skFitSpline(sketch, "E1012", {"points": [v(571.72, 147.58) * mm, v(573.27, 147.58) * mm, v(574.78, 147.18) * mm, v(575.08, 146.69) * mm]});
            skFitSpline(sketch, "E1013", {"points": [v(575.08, 146.69) * mm, v(575.42, 146.14) * mm, v(576.67, 146.16) * mm, v(578.36, 146.75) * mm]});
            skFitSpline(sketch, "E1014", {"points": [v(578.36, 146.75) * mm, v(579.88, 147.28) * mm, v(585.42, 147.5) * mm, v(590.85, 147.25) * mm]});
            skFitSpline(sketch, "E1015", {"points": [v(590.85, 147.25) * mm, v(596.22, 147) * mm, v(601.25, 146.8) * mm, v(602.03, 146.8) * mm]});
            skFitSpline(sketch, "E1016", {"points": [v(602.03, 146.8) * mm, v(618.82, 146.72) * mm, v(618.1, 146.9) * mm, v(623.72, 141.62) * mm]});
            skFitSpline(sketch, "E1017", {"points": [v(623.72, 141.62) * mm, v(626.6, 138.92) * mm, v(629.07, 136.08) * mm, v(629.23, 135.3) * mm]});
            skFitSpline(sketch, "E1018", {"points": [v(629.23, 135.3) * mm, v(629.75, 132.7) * mm, v(631.76, 129.17) * mm, v(633.43, 127.93) * mm]});
            skFitSpline(sketch, "E1019", {"points": [v(633.43, 127.93) * mm, v(638.23, 124.35) * mm, v(634.18, 112.63) * mm, v(628.15, 112.63) * mm]});
            skFitSpline(sketch, "E1020", {"points": [v(628.15, 112.63) * mm, v(626.73, 112.63) * mm, v(625.35, 112.04) * mm, v(625.07, 111.31) * mm]});
            skFitSpline(sketch, "E1021", {"points": [v(625.07, 111.31) * mm, v(624.8, 110.58) * mm, v(623.05, 109.7) * mm, v(621.2, 109.36) * mm]});
            skFitSpline(sketch, "E1022", {"points": [v(621.2, 109.36) * mm, v(619.28, 109) * mm, v(616.94, 107.64) * mm, v(615.7, 106.17) * mm]});
            skFitSpline(sketch, "E1023", {"points": [v(615.7, 106.17) * mm, v(613.54, 103.6) * mm, v(613.54, 103.6) * mm, v(600.47, 103.8) * mm]});
            skFitSpline(sketch, "E1024", {"points": [v(600.47, 103.8) * mm, v(593.27, 103.92) * mm, v(585.64, 104.3) * mm, v(583.5, 104.64) * mm]});
            skFitSpline(sketch, "E1025", {"points": [v(583.5, 104.64) * mm, v(581, 105.05) * mm, v(579.37, 104.9) * mm, v(578.95, 104.24) * mm]});
            skFitSpline(sketch, "E1026", {"points": [v(578.95, 104.24) * mm, v(578.01, 102.71) * mm, v(574.86, 102.96) * mm, v(571.74, 104.8) * mm]});
            skFitSpline(sketch, "E1027", {"points": [v(571.74, 104.8) * mm, v(569.06, 106.38) * mm, v(568.94, 106.36) * mm, v(564.72, 103.38) * mm]});
            skFitSpline(sketch, "E1028", {"points": [v(564.72, 103.38) * mm, v(562.35, 101.72) * mm, v(559.9, 100.36) * mm, v(559.27, 100.36) * mm]});
            skFitSpline(sketch, "E1029", {"points": [v(559.27, 100.36) * mm, v(558.38, 100.36) * mm, v(558.15, 94.03) * mm, v(558.27, 73.2) * mm]});
            skFitSpline(sketch, "E1030", {"points": [v(558.27, 73.2) * mm, v(558.5, 30.84) * mm, v(558.44, 32.36) * mm, v(559.86, 32.36) * mm]});
            skFitSpline(sketch, "E1031", {"points": [v(559.86, 32.36) * mm, v(561.8, 32.36) * mm, v(564.26, 29.18) * mm, v(564.26, 26.68) * mm]});
            skFitSpline(sketch, "E1032", {"points": [v(564.26, 26.68) * mm, v(564.26, 25.46) * mm, v(565.2, 23.07) * mm, v(566.37, 21.37) * mm]});
            skFitSpline(sketch, "E1033", {"points": [v(566.37, 21.37) * mm, v(568.48, 18.29) * mm, v(568.48, 18.29) * mm, v(592.1, 17.96) * mm]});
            skFitSpline(sketch, "E1034", {"points": [v(592.1, 17.96) * mm, v(605.1, 17.78) * mm, v(616.67, 17.36) * mm, v(617.82, 17.03) * mm]});
            skFitSpline(sketch, "E1035", {"points": [v(617.82, 17.03) * mm, v(624.4, 15.15) * mm, v(635.89, 4.03) * mm, v(631.25, 4.03) * mm]});
            skFitSpline(sketch, "E1036", {"points": [v(631.25, 4.03) * mm, v(630.4, 4.03) * mm, v(630.4, 3.71) * mm, v(631.2, 2.74) * mm]});
            skFitSpline(sketch, "E1037", {"points": [v(631.2, 2.74) * mm, v(632.01, 1.77) * mm, v(631.97, 1.2) * mm, v(631.01, 0.4) * mm]});
            skFitSpline(sketch, "E1038", {"points": [v(631.01, 0.4) * mm, v(630.13, -0.33) * mm, v(629.83, -2.48) * mm, v(630.04, -6.67) * mm]});
            skFitSpline(sketch, "E1039", {"points": [v(630.04, -6.67) * mm, v(630.3, -11.72) * mm, v(630.03, -12.97) * mm, v(628.46, -14.4) * mm]});
            skFitSpline(sketch, "E1040", {"points": [v(628.46, -14.4) * mm, v(627.43, -15.33) * mm, v(626.59, -17.12) * mm, v(626.59, -18.39) * mm]});
            skFitSpline(sketch, "E1041", {"points": [v(626.59, -18.39) * mm, v(626.59, -19.82) * mm, v(625.35, -21.78) * mm, v(623.28, -23.6) * mm]});
            skFitSpline(sketch, "E1042", {"points": [v(623.28, -23.6) * mm, v(621.46, -25.22) * mm, v(619.98, -27.1) * mm, v(619.98, -27.78) * mm]});
            skFitSpline(sketch, "E1043", {"points": [v(619.98, -27.78) * mm, v(619.98, -28.7) * mm, v(618.13, -29.02) * mm, v(612.93, -29.02) * mm]});
            skFitSpline(sketch, "E1044", {"points": [v(612.93, -29.02) * mm, v(607.3, -29.02) * mm, v(605.55, -29.37) * mm, v(604.2, -30.78) * mm]});
            skFitSpline(sketch, "E1045", {"points": [v(604.2, -30.78) * mm, v(600.55, -34.58) * mm, v(594.14, -35.48) * mm, v(585.95, -33.32) * mm]});
            skFitSpline(sketch, "E1046", {"points": [v(585.95, -33.32) * mm, v(584.07, -32.83) * mm, v(582.97, -33.3) * mm, v(580.76, -35.55) * mm]});
            skFitSpline(sketch, "E1047", {"points": [v(580.76, -35.55) * mm, v(577.34, -39.04) * mm, v(568.92, -39.81) * mm, v(567.17, -36.8) * mm]});
            skFitSpline(sketch, "E1048", {"points": [v(567.17, -36.8) * mm, v(566.63, -35.9) * mm, v(566.2, -35.68) * mm, v(566.18, -36.34) * mm]});
            skFitSpline(sketch, "E1049", {"points": [v(566.18, -36.34) * mm, v(566.17, -36.99) * mm, v(565.12, -37.52) * mm, v(563.87, -37.52) * mm]});
            skFitSpline(sketch, "E1050", {"points": [v(563.87, -37.52) * mm, v(558.73, -37.52) * mm, v(558.6, -37.83) * mm, v(558.6, -49.72) * mm]});
            skFitSpline(sketch, "E1051", {"points": [v(558.6, -49.72) * mm, v(558.6, -60.77) * mm, v(558.6, -60.77) * mm, v(561.4, -62.84) * mm]});
            skFitSpline(sketch, "E1052", {"points": [v(561.4, -62.84) * mm, v(564.2, -64.9) * mm, v(564.2, -64.9) * mm, v(564.06, -83.37) * mm]});
            skFitSpline(sketch, "E1053", {"points": [v(564.06, -83.37) * mm, v(564, -93.52) * mm, v(563.63, -102.01) * mm, v(563.27, -102.24) * mm]});
            skFitSpline(sketch, "E1054", {"points": [v(563.27, -102.24) * mm, v(562.9, -102.46) * mm, v(563, -104.67) * mm, v(563.47, -107.15) * mm]});
            skFitSpline(sketch, "E1055", {"points": [v(563.47, -107.15) * mm, v(563.95, -109.62) * mm, v(564.1, -112.99) * mm, v(563.8, -114.63) * mm]});
            skFitSpline(sketch, "E1056", {"points": [v(563.8, -114.63) * mm, v(562.84, -119.98) * mm, v(563.62, -120.17) * mm, v(586.01, -119.96) * mm]});
            skFitSpline(sketch, "E1057", {"points": [v(586.01, -119.96) * mm, v(598.85, -119.85) * mm, v(606.64, -120.14) * mm, v(607.4, -120.76) * mm]});
            skFitSpline(sketch, "E1058", {"points": [v(607.4, -120.76) * mm, v(608.21, -121.44) * mm, v(610.06, -121.42) * mm, v(613.38, -120.7) * mm]});
            skFitSpline(sketch, "E1059", {"points": [v(613.38, -120.7) * mm, v(622, -118.86) * mm, v(636.28, -119.35) * mm, v(638.17, -121.57) * mm]});
            skFitSpline(sketch, "E1060", {"points": [v(638.17, -121.57) * mm, v(639.06, -122.6) * mm, v(640.64, -123.46) * mm, v(641.69, -123.46) * mm]});
            skFitSpline(sketch, "E1061", {"points": [v(641.69, -123.46) * mm, v(642.73, -123.46) * mm, v(645.24, -124.95) * mm, v(647.26, -126.78) * mm]});
            skFitSpline(sketch, "E1062", {"points": [v(647.26, -126.78) * mm, v(650.9, -130.07) * mm, v(651.43, -131.43) * mm, v(652.58, -140.45) * mm]});
            skFitSpline(sketch, "E1063", {"points": [v(652.58, -140.45) * mm, v(653.1, -144.63) * mm, v(651.27, -151.8) * mm, v(649.5, -152.47) * mm]});
            skFitSpline(sketch, "E1064", {"points": [v(649.5, -152.47) * mm, v(648.77, -152.76) * mm, v(647.76, -154.04) * mm, v(647.28, -155.33) * mm]});
            skFitSpline(sketch, "E1065", {"points": [v(647.28, -155.33) * mm, v(646.64, -157) * mm, v(645.87, -157.53) * mm, v(644.58, -157.2) * mm]});
            skFitSpline(sketch, "E1066", {"points": [v(644.58, -157.2) * mm, v(643.42, -156.89) * mm, v(641.75, -157.73) * mm, v(639.85, -159.59) * mm]});
            skFitSpline(sketch, "E1067", {"points": [v(639.85, -159.59) * mm, v(637.41, -161.97) * mm, v(636.57, -162.3) * mm, v(634.82, -161.52) * mm]});
            skFitSpline(sketch, "E1068", {"points": [v(634.82, -161.52) * mm, v(633.67, -161) * mm, v(631.64, -160.88) * mm, v(630.32, -161.25) * mm]});
            skFitSpline(sketch, "E1069", {"points": [v(630.32, -161.25) * mm, v(627.13, -162.12) * mm, v(586.33, -161.89) * mm, v(585.42, -160.99) * mm]});
            skFitSpline(sketch, "E1070", {"points": [v(585.42, -160.99) * mm, v(584.38, -159.94) * mm, v(580.84, -160.14) * mm, v(579.67, -161.3) * mm]});
            skFitSpline(sketch, "E1071", {"points": [v(579.67, -161.3) * mm, v(578.95, -162.03) * mm, v(577.6, -162.04) * mm, v(575.06, -161.33) * mm]});
            skFitSpline(sketch, "E1072", {"points": [v(575.06, -161.33) * mm, v(573.08, -160.79) * mm, v(571.02, -160.7) * mm, v(570.46, -161.13) * mm]});
            skFitSpline(sketch, "E1073", {"points": [v(570.46, -161.13) * mm, v(569.18, -162.13) * mm, v(551.14, -161.85) * mm, v(548.8, -160.79) * mm]});
            skFitSpline(sketch, "E1074", {"points": [v(548.8, -160.79) * mm, v(547.74, -160.31) * mm, v(545.8, -160.43) * mm, v(544, -161.08) * mm]});
            skFitSpline(sketch, "E1075", {"points": [v(544, -161.08) * mm, v(536.82, -163.68) * mm, v(533.46, -162.7) * mm, v(526.87, -156.12) * mm]});
            skFitSpline(sketch, "E1076", {"points": [v(199.41, -158.96) * mm, v(197.42, -158.34) * mm, v(195.02, -156.82) * mm, v(194.07, -155.57) * mm]});
            skFitSpline(sketch, "E1077", {"points": [v(194.07, -155.57) * mm, v(192.75, -153.81) * mm, v(191.4, -153.28) * mm, v(188.02, -153.16) * mm]});
            skFitSpline(sketch, "E1078", {"points": [v(188.02, -153.16) * mm, v(183.97, -153.03) * mm, v(183.21, -152.57) * mm, v(177.44, -146.74) * mm]});
            skFitSpline(sketch, "E1079", {"points": [v(177.44, -146.74) * mm, v(173.1, -142.36) * mm, v(170.5, -140.45) * mm, v(168.89, -140.45) * mm]});
            skFitSpline(sketch, "E1080", {"points": [v(168.89, -140.45) * mm, v(165.98, -140.45) * mm, v(152.26, -127.48) * mm, v(150.54, -123.1) * mm]});
            skFitSpline(sketch, "E1081", {"points": [v(150.54, -123.1) * mm, v(149.9, -121.48) * mm, v(148.37, -118.77) * mm, v(147.13, -117.1) * mm]});
            skFitSpline(sketch, "E1082", {"points": [v(147.13, -117.1) * mm, v(145, -114.19) * mm, v(144.9, -113.47) * mm, v(145.26, -102.46) * mm]});
            skFitSpline(sketch, "E1083", {"points": [v(145.26, -102.46) * mm, v(145.46, -96.09) * mm, v(145.97, -90.07) * mm, v(146.4, -89.1) * mm]});
            skFitSpline(sketch, "E1084", {"points": [v(146.4, -89.1) * mm, v(146.84, -88.05) * mm, v(146.7, -86.6) * mm, v(146.05, -85.57) * mm]});
            skFitSpline(sketch, "E1085", {"points": [v(146.05, -85.57) * mm, v(143.15, -80.92) * mm, v(148.94, -71.51) * mm, v(154.7, -71.51) * mm]});
            skFitSpline(sketch, "E1086", {"points": [v(154.7, -71.51) * mm, v(156.04, -71.51) * mm, v(157.37, -71.12) * mm, v(157.66, -70.64) * mm]});
            skFitSpline(sketch, "E1087", {"points": [v(157.66, -70.64) * mm, v(157.96, -70.16) * mm, v(159.44, -69.5) * mm, v(160.95, -69.17) * mm]});
            skFitSpline(sketch, "E1088", {"points": [v(160.95, -69.17) * mm, v(162.45, -68.84) * mm, v(163.9, -68) * mm, v(164.18, -67.3) * mm]});
            skFitSpline(sketch, "E1089", {"points": [v(164.18, -67.3) * mm, v(164.85, -65.54) * mm, v(177.74, -65.58) * mm, v(180.54, -67.34) * mm]});
            skFitSpline(sketch, "E1090", {"points": [v(180.54, -67.34) * mm, v(181.95, -68.23) * mm, v(182.94, -70.32) * mm, v(183.72, -74.09) * mm]});
            skFitSpline(sketch, "E1091", {"points": [v(183.72, -74.09) * mm, v(184.34, -77.08) * mm, v(185.66, -80.56) * mm, v(186.64, -81.8) * mm]});
            skFitSpline(sketch, "E1092", {"points": [v(186.64, -81.8) * mm, v(188.14, -83.72) * mm, v(188.33, -85.02) * mm, v(187.81, -90.04) * mm]});
            skFitSpline(sketch, "E1093", {"points": [v(187.81, -90.04) * mm, v(187.2, -96) * mm, v(187.2, -96) * mm, v(193.09, -101.7) * mm]});
            skFitSpline(sketch, "E1094", {"points": [v(193.09, -101.7) * mm, v(196.74, -105.24) * mm, v(199.77, -107.4) * mm, v(201.1, -107.4) * mm]});
            skFitSpline(sketch, "E1095", {"points": [v(201.1, -107.4) * mm, v(202.26, -107.4) * mm, v(203.99, -108.25) * mm, v(204.93, -109.29) * mm]});
            skFitSpline(sketch, "E1096", {"points": [v(204.93, -109.29) * mm, v(207.27, -111.88) * mm, v(214.84, -111.96) * mm, v(216.44, -109.4) * mm]});
            skFitSpline(sketch, "E1097", {"points": [v(216.44, -109.4) * mm, v(217.05, -108.44) * mm, v(218.74, -107.34) * mm, v(220.2, -106.97) * mm]});
            skFitSpline(sketch, "E1098", {"points": [v(220.2, -106.97) * mm, v(224, -106.02) * mm, v(225.23, -104.71) * mm, v(225.23, -101.64) * mm]});
            skFitSpline(sketch, "E1099", {"points": [v(225.23, -101.64) * mm, v(225.23, -99.55) * mm, v(225.76, -98.8) * mm, v(227.6, -98.35) * mm]});
            skFitSpline(sketch, "E1100", {"points": [v(227.6, -98.35) * mm, v(230.09, -97.72) * mm, v(230.55, -96.11) * mm, v(229.03, -93.28) * mm]});
            skFitSpline(sketch, "E1101", {"points": [v(229.03, -93.28) * mm, v(228.3, -91.93) * mm, v(228.71, -90.87) * mm, v(230.9, -88.38) * mm]});
            skFitSpline(sketch, "E1102", {"points": [v(230.9, -88.38) * mm, v(233.63, -85.29) * mm, v(233.7, -84.95) * mm, v(233.72, -75.04) * mm]});
            skFitSpline(sketch, "E1103", {"points": [v(233.72, -75.04) * mm, v(233.72, -68.62) * mm, v(234.16, -64.19) * mm, v(234.9, -63) * mm]});
            skFitSpline(sketch, "E1104", {"points": [v(234.9, -63) * mm, v(235.83, -61.51) * mm, v(235.83, -60.74) * mm, v(234.9, -59.25) * mm]});
            skFitSpline(sketch, "E1105", {"points": [v(234.9, -59.25) * mm, v(234.26, -58.22) * mm, v(233.73, -56.11) * mm, v(233.73, -54.56) * mm]});
            skFitSpline(sketch, "E1106", {"points": [v(233.73, -54.56) * mm, v(233.73, -52.6) * mm, v(233.08, -51.4) * mm, v(231.6, -50.63) * mm]});
            skFitSpline(sketch, "E1107", {"points": [v(231.6, -50.63) * mm, v(228.46, -48.97) * mm, v(227.96, -47.83) * mm, v(228.53, -43.64) * mm]});
            skFitSpline(sketch, "E1108", {"points": [v(228.53, -43.64) * mm, v(229.38, -37.5) * mm, v(221.11, -29.02) * mm, v(214.26, -29.02) * mm]});
            skFitSpline(sketch, "E1109", {"points": [v(214.26, -29.02) * mm, v(210.67, -29.02) * mm, v(209.04, -28.55) * mm, v(207.76, -27.13) * mm]});
            skFitSpline(sketch, "E1110", {"points": [v(207.76, -27.13) * mm, v(206.24, -25.46) * mm, v(204.85, -25.24) * mm, v(195.54, -25.24) * mm]});
            skFitSpline(sketch, "E1111", {"points": [v(195.54, -25.24) * mm, v(185.04, -25.24) * mm, v(185.04, -25.24) * mm, v(180.04, -20.48) * mm]});
            skFitSpline(sketch, "E1112", {"points": [v(180.04, -20.48) * mm, v(176.47, -17.07) * mm, v(174.55, -15.87) * mm, v(173.29, -16.27) * mm]});
            skFitSpline(sketch, "E1113", {"points": [v(173.29, -16.27) * mm, v(170.81, -17.06) * mm, v(144.96, 8.7) * mm, v(144.96, 11.96) * mm]});
            skFitSpline(sketch, "E1114", {"points": [v(144.96, 11.96) * mm, v(144.96, 14.59) * mm, v(142.57, 20.65) * mm, v(141.2, 21.5) * mm]});
            skFitSpline(sketch, "E1115", {"points": [v(141.2, 21.5) * mm, v(139.95, 22.26) * mm, v(139.94, 37.74) * mm, v(141.18, 38.5) * mm]});
            skFitSpline(sketch, "E1116", {"points": [v(141.18, 38.5) * mm, v(142.36, 39.23) * mm, v(142.44, 44.64) * mm, v(141.28, 44.64) * mm]});
            skFitSpline(sketch, "E1117", {"points": [v(141.28, 44.64) * mm, v(139.71, 44.64) * mm, v(139.24, 47.73) * mm, v(140.51, 49.73) * mm]});
            skFitSpline(sketch, "E1118", {"points": [v(141.12, 55.5) * mm, v(139.73, 63.56) * mm, v(140.59, 95.3) * mm, v(142.25, 97.19) * mm]});
            skFitSpline(sketch, "E1119", {"points": [v(142.25, 97.19) * mm, v(143.1, 98.15) * mm, v(144.1, 101.06) * mm, v(144.46, 103.64) * mm]});
            skFitSpline(sketch, "E1120", {"points": [v(144.46, 103.64) * mm, v(145.02, 107.5) * mm, v(145.92, 109.15) * mm, v(149.54, 112.86) * mm]});
            skFitSpline(sketch, "E1121", {"points": [v(149.54, 112.86) * mm, v(153.5, 116.95) * mm, v(153.98, 117.9) * mm, v(154.4, 122.8) * mm]});
            skFitSpline(sketch, "E1122", {"points": [v(154.4, 122.8) * mm, v(154.87, 128.2) * mm, v(154.88, 128.22) * mm, v(158.18, 128.5) * mm]});
            skFitSpline(sketch, "E1123", {"points": [v(158.18, 128.5) * mm, v(160.35, 128.67) * mm, v(162.18, 129.6) * mm, v(163.49, 131.19) * mm]});
            skFitSpline(sketch, "E1124", {"points": [v(163.49, 131.19) * mm, v(165.22, 133.28) * mm, v(165.77, 133.46) * mm, v(167.56, 132.5) * mm]});
            skFitSpline(sketch, "E1125", {"points": [v(167.56, 132.5) * mm, v(170.36, 131) * mm, v(172.34, 132.7) * mm, v(172.36, 136.6) * mm]});
            skFitSpline(sketch, "E1126", {"points": [v(172.36, 136.6) * mm, v(172.38, 141.02) * mm, v(173.4, 141.9) * mm, v(178.96, 142.3) * mm]});
            skFitSpline(sketch, "E1127", {"points": [v(178.96, 142.3) * mm, v(183.1, 142.58) * mm, v(184.35, 143.1) * mm, v(185.82, 145.11) * mm]});
            skFitSpline(sketch, "E1128", {"points": [v(185.82, 145.11) * mm, v(186.8, 146.47) * mm, v(188.05, 147.58) * mm, v(188.58, 147.58) * mm]});
            skFitSpline(sketch, "E1129", {"points": [v(188.58, 147.58) * mm, v(189.11, 147.58) * mm, v(190.36, 148.61) * mm, v(191.36, 149.88) * mm]});
            skFitSpline(sketch, "E1130", {"points": [v(191.36, 149.88) * mm, v(192.45, 151.26) * mm, v(193.89, 152.04) * mm, v(194.97, 151.83) * mm]});
            skFitSpline(sketch, "E1131", {"points": [v(194.97, 151.83) * mm, v(197.63, 151.32) * mm, v(200.68, 149.53) * mm, v(200.68, 148.49) * mm]});
            skFitSpline(sketch, "E1132", {"points": [v(200.68, 148.49) * mm, v(200.68, 147.99) * mm, v(201.32, 147.58) * mm, v(202.1, 147.58) * mm]});
            skFitSpline(sketch, "E1133", {"points": [v(202.1, 147.58) * mm, v(202.87, 147.58) * mm, v(203.51, 148.22) * mm, v(203.51, 149.02) * mm]});
            skFitSpline(sketch, "E1134", {"points": [v(203.51, 149.02) * mm, v(203.51, 152.4) * mm, v(209.5, 152.55) * mm, v(214.04, 149.3) * mm]});
            skFitSpline(sketch, "E1135", {"points": [v(214.04, 149.3) * mm, v(215.27, 148.41) * mm, v(215.9, 148.5) * mm, v(217.17, 149.77) * mm]});
            skFitSpline(sketch, "E1136", {"points": [v(217.17, 149.77) * mm, v(219.53, 152.13) * mm, v(228.03, 151.93) * mm, v(230.68, 149.46) * mm]});
            skFitSpline(sketch, "E1137", {"points": [v(230.68, 149.46) * mm, v(231.8, 148.43) * mm, v(233.5, 147.58) * mm, v(234.49, 147.58) * mm]});
            skFitSpline(sketch, "E1138", {"points": [v(234.49, 147.58) * mm, v(235.47, 147.58) * mm, v(238.35, 145.45) * mm, v(240.9, 142.86) * mm]});
            skFitSpline(sketch, "E1139", {"points": [v(240.9, 142.86) * mm, v(244.02, 139.68) * mm, v(246.3, 138.13) * mm, v(247.9, 138.13) * mm]});
            skFitSpline(sketch, "E1140", {"points": [v(247.9, 138.13) * mm, v(249.53, 138.13) * mm, v(251.83, 136.52) * mm, v(255.28, 132.94) * mm]});
            skFitSpline(sketch, "E1141", {"points": [v(255.28, 132.94) * mm, v(258.04, 130.08) * mm, v(260.67, 127.74) * mm, v(261.14, 127.74) * mm]});
            skFitSpline(sketch, "E1142", {"points": [v(261.14, 127.74) * mm, v(261.6, 127.74) * mm, v(262.26, 126.15) * mm, v(262.62, 124.2) * mm]});
            skFitSpline(sketch, "E1143", {"points": [v(262.62, 124.2) * mm, v(262.97, 122.25) * mm, v(264.05, 119.9) * mm, v(265.02, 118.97) * mm]});
            skFitSpline(sketch, "E1144", {"points": [v(265.02, 118.97) * mm, v(267.58, 116.52) * mm, v(267.5, 107.9) * mm, v(264.9, 105.55) * mm]});
            skFitSpline(sketch, "E1145", {"points": [v(264.9, 105.55) * mm, v(263.2, 104.02) * mm, v(263, 102.64) * mm, v(263, 92.42) * mm]});
            skFitSpline(sketch, "E1146", {"points": [v(263, 92.42) * mm, v(263, 81) * mm, v(263, 81) * mm, v(258.8, 76.98) * mm]});
            skFitSpline(sketch, "E1147", {"points": [v(258.8, 76.98) * mm, v(253.45, 71.88) * mm, v(245.31, 71.02) * mm, v(243.34, 75.35) * mm]});
            skFitSpline(sketch, "E1148", {"points": [v(243.34, 75.35) * mm, v(242.74, 76.65) * mm, v(241.29, 78.16) * mm, v(240.1, 78.7) * mm]});
            skFitSpline(sketch, "E1149", {"points": [v(240.1, 78.7) * mm, v(237.46, 79.9) * mm, v(233.73, 85.17) * mm, v(233.73, 87.7) * mm]});
            skFitSpline(sketch, "E1150", {"points": [v(233.73, 87.7) * mm, v(233.73, 88.77) * mm, v(232.03, 90.9) * mm, v(229.72, 92.7) * mm]});
            skFitSpline(sketch, "E1151", {"points": [v(229.72, 92.7) * mm, v(225.7, 95.83) * mm, v(225.7, 95.83) * mm, v(215.55, 95.29) * mm]});
            skFitSpline(sketch, "E1152", {"points": [v(215.55, 95.29) * mm, v(205.53, 94.74) * mm, v(199.9, 92.95) * mm, v(201.25, 90.74) * mm]});
            skFitSpline(sketch, "E1153", {"points": [v(201.25, 90.74) * mm, v(201.56, 90.25) * mm, v(200.5, 88.66) * mm, v(198.88, 87.22) * mm]});
            skFitSpline(sketch, "E1154", {"points": [v(198.88, 87.22) * mm, v(197.04, 85.57) * mm, v(195.96, 83.7) * mm, v(195.96, 82.16) * mm]});
            skFitSpline(sketch, "E1155", {"points": [v(193.14, 77.7) * mm, v(190.74, 76) * mm, v(190.5, 75.45) * mm, v(191.45, 73.93) * mm]});
            skFitSpline(sketch, "E1156", {"points": [v(191.45, 73.93) * mm, v(192.32, 72.52) * mm, v(192.27, 71.6) * mm, v(191.19, 69.57) * mm]});
            skFitSpline(sketch, "E1157", {"points": [v(191.19, 69.57) * mm, v(190.12, 67.57) * mm, v(190.08, 66.9) * mm, v(191, 66.6) * mm]});
            skFitSpline(sketch, "E1158", {"points": [v(191, 66.6) * mm, v(192.5, 66.1) * mm, v(192.55, 60.98) * mm, v(191.05, 60.48) * mm]});
            skFitSpline(sketch, "E1159", {"points": [v(191.05, 60.48) * mm, v(190.32, 60.24) * mm, v(190.22, 59.48) * mm, v(190.74, 58.28) * mm]});
            skFitSpline(sketch, "E1160", {"points": [v(190.74, 58.28) * mm, v(191.19, 57.27) * mm, v(191.65, 53.12) * mm, v(191.76, 49.06) * mm]});
            skFitSpline(sketch, "E1161", {"points": [v(191.76, 49.06) * mm, v(191.93, 43.03) * mm, v(192.34, 41.28) * mm, v(193.96, 39.55) * mm]});
            skFitSpline(sketch, "E1162", {"points": [v(193.96, 39.55) * mm, v(195.43, 37.98) * mm, v(195.95, 36.21) * mm, v(195.95, 32.72) * mm]});
            skFitSpline(sketch, "E1163", {"points": [v(195.95, 32.72) * mm, v(195.95, 28) * mm, v(195.95, 28) * mm, v(199.94, 27.12) * mm]});
            skFitSpline(sketch, "E1164", {"points": [v(199.94, 27.12) * mm, v(203.35, 26.35) * mm, v(204.06, 25.77) * mm, v(204.82, 23.08) * mm]});
            skFitSpline(sketch, "E1165", {"points": [v(204.82, 23.08) * mm, v(205.73, 19.84) * mm, v(206.77, 19.59) * mm, v(211.35, 21.5) * mm]});
            skFitSpline(sketch, "E1166", {"points": [v(211.35, 21.5) * mm, v(212.63, 22.04) * mm, v(213.19, 21.72) * mm, v(213.58, 20.2) * mm]});
            skFitSpline(sketch, "E1167", {"points": [v(213.58, 20.2) * mm, v(214.24, 17.71) * mm, v(219.12, 16.21) * mm, v(222.17, 17.57) * mm]});
            skFitSpline(sketch, "E1168", {"points": [v(222.17, 17.57) * mm, v(223.99, 18.37) * mm, v(224.76, 18.06) * mm, v(227.24, 15.53) * mm]});
            skFitSpline(sketch, "E1169", {"points": [v(227.24, 15.53) * mm, v(228.85, 13.88) * mm, v(230.96, 12.53) * mm, v(231.94, 12.53) * mm]});
            skFitSpline(sketch, "E1170", {"points": [v(231.94, 12.53) * mm, v(232.9, 12.53) * mm, v(234.24, 11.68) * mm, v(234.88, 10.64) * mm]});
            skFitSpline(sketch, "E1171", {"points": [v(234.88, 10.64) * mm, v(235.66, 9.4) * mm, v(237.09, 8.75) * mm, v(239.07, 8.75) * mm]});
            skFitSpline(sketch, "E1172", {"points": [v(239.07, 8.75) * mm, v(242.69, 8.75) * mm, v(249.75, 2.04) * mm, v(249.76, -1.4) * mm]});
            skFitSpline(sketch, "E1173", {"points": [v(249.76, -1.4) * mm, v(249.77, -2.58) * mm, v(250.62, -4.27) * mm, v(251.66, -5.16) * mm]});
            skFitSpline(sketch, "E1174", {"points": [v(251.66, -5.16) * mm, v(252.7, -6.05) * mm, v(253.55, -7.72) * mm, v(253.55, -8.88) * mm]});
            skFitSpline(sketch, "E1175", {"points": [v(253.55, -8.88) * mm, v(253.55, -10.04) * mm, v(254.63, -12.58) * mm, v(255.94, -14.52) * mm]});
            skFitSpline(sketch, "E1176", {"points": [v(255.94, -14.52) * mm, v(257.26, -16.46) * mm, v(258.14, -18.55) * mm, v(257.9, -19.17) * mm]});
            skFitSpline(sketch, "E1177", {"points": [v(257.9, -19.17) * mm, v(257.67, -19.8) * mm, v(258.71, -21.5) * mm, v(260.23, -22.95) * mm]});
            skFitSpline(sketch, "E1178", {"points": [v(260.23, -22.95) * mm, v(263, -25.6) * mm, v(263, -25.6) * mm, v(263, -37.19) * mm]});
            skFitSpline(sketch, "E1179", {"points": [v(263, -37.19) * mm, v(263, -47.82) * mm, v(263.15, -48.87) * mm, v(264.88, -49.8) * mm]});
            skFitSpline(sketch, "E1180", {"points": [v(264.88, -49.8) * mm, v(266.62, -50.72) * mm, v(266.77, -51.77) * mm, v(266.77, -62.4) * mm]});
            skFitSpline(sketch, "E1181", {"points": [v(266.77, -62.4) * mm, v(266.77, -74) * mm, v(266.77, -74) * mm, v(269.57, -76.68) * mm]});
            skFitSpline(sketch, "E1182", {"points": [v(269.57, -76.68) * mm, v(272.32, -79.3) * mm, v(272.37, -79.55) * mm, v(272.23, -88.24) * mm]});
            skFitSpline(sketch, "E1183", {"points": [v(272.23, -88.24) * mm, v(272.16, -93.13) * mm, v(271.8, -97.3) * mm, v(271.45, -97.51) * mm]});
            skFitSpline(sketch, "E1184", {"points": [v(271.45, -97.51) * mm, v(271.1, -97.73) * mm, v(271.13, -99.93) * mm, v(271.5, -102.41) * mm]});
            skFitSpline(sketch, "E1185", {"points": [v(271.5, -102.41) * mm, v(271.86, -104.9) * mm, v(272.06, -109.48) * mm, v(271.93, -112.6) * mm]});
            skFitSpline(sketch, "E1186", {"points": [v(271.93, -112.6) * mm, v(271.8, -115.71) * mm, v(271.65, -119.37) * mm, v(271.6, -120.72) * mm]});
            skFitSpline(sketch, "E1187", {"points": [v(271.6, -120.72) * mm, v(271.54, -122.07) * mm, v(270.48, -124.27) * mm, v(269.25, -125.6) * mm]});
            skFitSpline(sketch, "E1188", {"points": [v(269.25, -125.6) * mm, v(268.02, -126.93) * mm, v(266.72, -129.53) * mm, v(266.38, -131.37) * mm]});
            skFitSpline(sketch, "E1189", {"points": [v(266.38, -131.37) * mm, v(265.84, -134.26) * mm, v(265.25, -134.87) * mm, v(262.23, -135.68) * mm]});
            skFitSpline(sketch, "E1190", {"points": [v(262.23, -135.68) * mm, v(257.95, -136.83) * mm, v(250.29, -144.44) * mm, v(249.34, -148.47) * mm]});
            skFitSpline(sketch, "E1191", {"points": [v(249.34, -148.47) * mm, v(248.62, -151.54) * mm, v(247.38, -152.7) * mm, v(244.8, -152.72) * mm]});
            skFitSpline(sketch, "E1192", {"points": [v(244.8, -152.72) * mm, v(243.89, -152.72) * mm, v(241.43, -153.97) * mm, v(239.34, -155.48) * mm]});
            skFitSpline(sketch, "E1193", {"points": [v(239.34, -155.48) * mm, v(235.64, -158.16) * mm, v(235.23, -158.24) * mm, v(223.53, -158.33) * mm]});
            skFitSpline(sketch, "E1194", {"points": [v(223.53, -158.33) * mm, v(216.62, -158.4) * mm, v(211.39, -158.83) * mm, v(211.2, -159.36) * mm]});
            skFitSpline(sketch, "E1195", {"points": [v(211.2, -159.36) * mm, v(210.79, -160.6) * mm, v(203.92, -160.36) * mm, v(199.4, -158.96) * mm]});
            skFitSpline(sketch, "E1196", {"points": [v(-771.57, -135.62) * mm, v(-771.62, -148.62) * mm], "startDerivative": vector(-0.05, -13) * mm, "endDerivative": vector(-0.05, -13) * mm});
            skFitSpline(sketch, "E1197", {"points": [v(-770.14, -96.03) * mm, v(-770.49, -99.09) * mm], "startDerivative": vector(-0.34, -3.06) * mm, "endDerivative": vector(-0.34, -3.06) * mm});
            skFitSpline(sketch, "E1198", {"points": [v(814.87, 57.1) * mm, v(815.52, 52.2) * mm], "startDerivative": vector(0.64, -4.9) * mm, "endDerivative": vector(0.64, -4.9) * mm});
            skFitSpline(sketch, "E1199", {"points": [v(722.48, -159) * mm, v(724.83, -164.25) * mm], "startDerivative": vector(2.34, -5.26) * mm, "endDerivative": vector(2.34, -5.26) * mm});
            skFitSpline(sketch, "E1200", {"points": [v(386.06, 141.81) * mm, v(380.7, 141.73) * mm], "startDerivative": vector(-5.35, -0.08) * mm, "endDerivative": vector(-5.35, -0.08) * mm});
            skFitSpline(sketch, "E1201", {"points": [v(141.12, 55.5) * mm, v(140.51, 49.73) * mm], "startDerivative": vector(-0.6, -5.77) * mm, "endDerivative": vector(-0.6, -5.77) * mm});
            skFitSpline(sketch, "E1202", {"points": [v(-62.79, 11.12) * mm, v(-62.8, 17.73) * mm], "startDerivative": vector(0, 6.61) * mm, "endDerivative": vector(0, 6.61) * mm});
            skFitSpline(sketch, "E1203", {"points": [v(-60.91, -76.7) * mm, v(-58.08, -80.74) * mm], "startDerivative": vector(2.83, -4.03) * mm, "endDerivative": vector(2.83, -4.03) * mm});
            skFitSpline(sketch, "E1204", {"points": [v(-60.34, -95.17) * mm, v(-57.3, -103.8) * mm], "startDerivative": vector(3.04, -8.62) * mm, "endDerivative": vector(3.04, -8.62) * mm});
            skFitSpline(sketch, "E1205", {"points": [v(195.96, 82.16) * mm, v(193.14, 77.7) * mm], "startDerivative": vector(-2.81, -4.45) * mm, "endDerivative": vector(-2.81, -4.45) * mm});
            skFitSpline(sketch, "E1206", {"points": [v(-222.25, -85.1) * mm, v(-222.29, -80.22) * mm], "startDerivative": vector(-0.04, 4.89) * mm, "endDerivative": vector(-0.04, 4.89) * mm});
            skFitSpline(sketch, "E1207", {"points": [v(-813.1, 60.35) * mm, v(-811.68, 56.54) * mm], "startDerivative": vector(1.42, -3.81) * mm, "endDerivative": vector(1.42, -3.81) * mm});
            skFitSpline(sketch, "E1208", {"points": [v(-976.94, 49.24) * mm, v(-970.1, 39.62) * mm], "startDerivative": vector(6.85, -9.62) * mm, "endDerivative": vector(6.85, -9.62) * mm});
            skFitSpline(sketch, "E1209", {"points": [v(-928.78, 146.37) * mm, v(-930.66, 142.6) * mm], "startDerivative": vector(-1.89, -3.78) * mm, "endDerivative": vector(-1.89, -3.78) * mm});
            skFitSpline(sketch, "E1210", {"points": [v(-1058.38, -3.53) * mm, v(-1058.4, -7.62) * mm], "startDerivative": vector(-0.01, -4.09) * mm, "endDerivative": vector(-0.01, -4.09) * mm});
            skFitSpline(sketch, "E1211", {"points": [v(-1048.7, 154.95) * mm, v(-1047.9, 156.08) * mm], "startDerivative": vector(0.8, 1.12) * mm, "endDerivative": vector(0.8, 1.12) * mm});
            skSolve(sketch);
        }
        {
            var Q0;
            Q0=qCreatedBy(makeId("Top.planeOp"), FACE);
            var sketch = newSketch(context, id + "F1", { "sketchPlane" : qUnion([Q0])});
            skLineSegment(sketch, "E1212", {"start": v(-142.29, 23.39) * mm, "end": v(-142.29, -38.4) * mm});
            skLineSegment(sketch, "E1213", {"start": v(-152.67, -39.05) * mm, "end": v(-152.67, 21.6) * mm});
            skFitSpline(sketch, "E1214", {"points": [v(-152.67, 21.6) * mm, v(-154.72, 24.42) * mm, v(-159.85, 25.06) * mm, v(-164.08, 26.47) * mm, v(-165.75, 30.95) * mm, v(-163.57, 34.29) * mm, v(-159.08, 35.7) * mm, v(-141.13, 35.7) * mm, v(-132.41, 35.19) * mm, v(-130.75, 33.26) * mm, v(-130.36, 30.83) * mm, v(-132.41, 27.24) * mm, v(-135.75, 24.03) * mm, v(-139.34, 23.77) * mm, v(-142.29, 23.39) * mm], "startDerivative": vector(-25, 55.71) * mm, "endDerivative": vector(0, -51.6) * mm});
            skFitSpline(sketch, "E1215", {"points": [v(-152.67, -39.05) * mm, v(-150.1, -42.64) * mm, v(-146.13, -43.8) * mm, v(-143.18, -42.64) * mm, v(-142.29, -38.4) * mm], "startDerivative": vector(0, -17.9) * mm, "endDerivative": vector(-3.82, 17.37) * mm});
            skFitSpline(sketch, "E1216", {"points": [v(-67.81, -35.86) * mm, v(-63.27, -40.51) * mm, v(-56.91, -41.44) * mm, v(-44.97, -41.75) * mm, v(-33.8, -36.32) * mm, v(-32.24, -27.95) * mm, v(-32.09, -13.2) * mm, v(-32.7, -1.57) * mm, v(-35.2, 2) * mm, v(-33.64, 6.8) * mm, v(-31.47, 14.1) * mm, v(-29.92, 27.28) * mm, v(-31.78, 37.99) * mm, v(-38.3, 44.66) * mm, v(-48.22, 46.05) * mm, v(-51.48, 46.52) * mm, v(-60.17, 45.12) * mm, v(-66.37, 42.18) * mm, v(-67.42, 37.99) * mm], "startDerivative": vector(78.13, -117.28) * mm, "endDerivative": vector(-0.6, -114.28) * mm});
            skLineSegment(sketch, "E1217", {"start": v(-67.42, 37.99) * mm, "end": v(-67.81, -35.86) * mm});
            skFitSpline(sketch, "E1218", {"points": [v(-55.98, -7.62) * mm, v(-56.45, -16.78) * mm, v(-54.74, -23.91) * mm, v(-53.19, -27.17) * mm, v(-48.84, -28.88) * mm, v(-44.81, -26.55) * mm, v(-42.64, -25.3) * mm, v(-42.8, -15.23) * mm, v(-42.95, -8.86) * mm, v(-43.26, -4.06) * mm, v(-46.83, -1.73) * mm, v(-52.88, -2.81) * mm, v(-55.98, -7.62) * mm]});
            skFitSpline(sketch, "E1219", {"points": [v(-47.3, 6.03) * mm, v(-42.02, 9.29) * mm, v(-41.4, 15.5) * mm, v(-42.64, 21.54) * mm, v(-41.86, 26.35) * mm, v(-42.64, 31) * mm, v(-48.69, 31.32) * mm, v(-53.96, 27.6) * mm, v(-54.43, 22.63) * mm, v(-55.36, 18.6) * mm, v(-53.8, 6.65) * mm, v(-49.93, 5.72) * mm, v(-47.3, 6.03) * mm]});
            skFitSpline(sketch, "E1220", {"points": [v(-269.4, -37.9) * mm, v(-269.61, -18.43) * mm, v(-268.75, -14.1) * mm, v(-268.1, 3.42) * mm, v(-266.58, 7.31) * mm, v(-267.45, 11) * mm, v(-268.75, 15.32) * mm, v(-268.53, 24.19) * mm, v(-268.75, 34.36) * mm, v(-266.37, 38.47) * mm, v(-260.3, 41.93) * mm, v(-254.9, 41.06) * mm, v(-251.66, 34.57) * mm, v(-251, 23.1) * mm, v(-247.98, 14.89) * mm, v(-244.73, 8.83) * mm, v(-243.65, 5.15) * mm, v(-242.35, 8.4) * mm, v(-239.1, 20.3) * mm, v(-237.16, 27.65) * mm, v(-236.73, 30.25) * mm, v(-237.8, 33.7) * mm, v(-233.7, 41.28) * mm, v(-225.48, 42.36) * mm, v(-221.15, 44.53) * mm, v(-218.3, 39.85) * mm, v(-218.34, 28.73) * mm, v(-218.55, 7.31) * mm, v(-217.69, -3.72) * mm, v(-216.6, -13.46) * mm, v(-218.34, -23.62) * mm, v(-217.04, -33.8) * mm, v(-217.69, -38.99) * mm, v(-221.37, -44.4) * mm, v(-227.42, -45.04) * mm, v(-230.24, -39.85) * mm, v(-231.75, -28.6) * mm, v(-231.53, -14.97) * mm, v(-233.27, -12.16) * mm, v(-235.86, -17.35) * mm, v(-238.03, -23.2) * mm, v(-241.92, -24.92) * mm, v(-246.46, -26.22) * mm, v(-249.28, -26.22) * mm, v(-252.3, -21.9) * mm, v(-253.39, -13.89) * mm, v(-255.77, -10) * mm, v(-255.33, -19.3) * mm, v(-255.98, -28.38) * mm, v(-255.33, -32.06) * mm, v(-256.42, -35.96) * mm, v(-258.58, -41.15) * mm, v(-264.42, -44.4) * mm, v(-269.4, -37.9) * mm]});
            skFitSpline(sketch, "E1221", {"points": [v(-196.05, -34.44) * mm, v(-195.62, -23.84) * mm, v(-196.27, -14.32) * mm, v(-198.22, -6.1) * mm, v(-202.33, 0) * mm, v(-202.11, 7.96) * mm, v(-207.52, 16.18) * mm, v(-207.95, 23.1) * mm, v(-208.82, 27) * mm, v(-203.84, 33.92) * mm, v(-198.87, 36.95) * mm, v(-196.27, 32.41) * mm, v(-196.49, 25.05) * mm, v(-194.1, 17.27) * mm, v(-192.37, 12.29) * mm, v(-191.94, 7.96) * mm, v(-188.91, 11) * mm, v(-188.26, 16.83) * mm, v(-185.88, 27.22) * mm, v(-181.12, 34.8) * mm, v(-174.2, 35.22) * mm, v(-174.2, 30.9) * mm, v(-173.77, 21.38) * mm, v(-175.93, 14.45) * mm, v(-177.66, 8.61) * mm, v(-181.56, 0) * mm, v(-183.07, -9.13) * mm, v(-183.94, -14.54) * mm, v(-183.94, -30.33) * mm, v(-183.72, -37.9) * mm, v(-190, -43.96) * mm, v(-194.97, -39.64) * mm, v(-196.05, -34.44) * mm]});
            skFitSpline(sketch, "E1222", {"points": [v(-118.17, -37.9) * mm, v(-117.3, -31.41) * mm, v(-118.6, -28.17) * mm, v(-118.6, 4.28) * mm, v(-117.3, 11.86) * mm, v(-118.6, 18.13) * mm, v(-117.95, 33.5) * mm, v(-112.76, 37.39) * mm, v(-107.35, 36.74) * mm, v(-105.83, 32.84) * mm, v(-106.05, 20.94) * mm, v(-106.48, 9.9) * mm, v(-103.24, 4.28) * mm, v(-98.26, 4.72) * mm, v(-96.1, 8.4) * mm, v(-95.02, 17.7) * mm, v(-93.93, 21.6) * mm, v(-93.93, 26.57) * mm, v(-92.85, 35) * mm, v(-88.1, 35.87) * mm, v(-86.8, 36.95) * mm, v(-81.5, 32.54) * mm, v(-84.2, 25.05) * mm, v(-82.9, 19.43) * mm, v(-82.68, 11) * mm, v(-84.2, 5.8) * mm, v(-84.2, -11.3) * mm, v(-82.9, -14.1) * mm, v(-83.33, -21.03) * mm, v(-83.33, -26.87) * mm, v(-82.9, -32.06) * mm, v(-83.33, -37.9) * mm, v(-85.06, -41.15) * mm, v(-90.69, -41.37) * mm, v(-94.37, -34.23) * mm, v(-93.29, -14.97) * mm, v(-96.53, -6.97) * mm, v(-103.02, -5.88) * mm, v(-106.27, -14.1) * mm, v(-106.92, -30.55) * mm, v(-109.51, -39.85) * mm, v(-115.79, -41.15) * mm, v(-118.17, -37.9) * mm]});
            skFitSpline(sketch, "E1223", {"points": [v(-15.7, -22.45) * mm, v(-15.7, -18.45) * mm, v(-15.25, -12.07) * mm, v(-15.7, -3.01) * mm, v(-16.43, 10.5) * mm, v(-16.14, 24.15) * mm, v(-13.91, 33.5) * mm, v(-10.94, 37.06) * mm, v(-6.05, 36.17) * mm, v(-3.82, 34.54) * mm, v(-3.37, 28) * mm, v(-3.23, 18.95) * mm, v(-2.04, 9.16) * mm, v(-3.82, 3.22) * mm, v(-3.23, -5.54) * mm, v(-2.78, -16.52) * mm, v(-2.04, -25.13) * mm, v(0, -27.06) * mm, v(4.64, -26.76) * mm, v(7.02, -23.5) * mm, v(7.31, -12.66) * mm, v(7.76, -4.65) * mm, v(8.05, 5.15) * mm, v(7.6, 16.43) * mm, v(8.05, 25.19) * mm, v(8.05, 32.46) * mm, v(13.25, 35.87) * mm, v(19.19, 37.2) * mm, v(21.56, 32.76) * mm, v(21.11, 23.7) * mm, v(20.08, 15.84) * mm, v(20.67, 9) * mm, v(20.08, 0) * mm, v(19.04, -10.58) * mm, v(19.19, -16.96) * mm, v(19.63, -24.68) * mm, v(18, -32.1) * mm, v(11.91, -38.63) * mm, v(8.8, -41.45) * mm, v(-3.52, -41.3) * mm, v(-11.24, -36.1) * mm, v(-13.61, -28.69) * mm, v(-15.7, -22.45) * mm]});
            skFitSpline(sketch, "E1224", {"points": [v(45, -16.82) * mm, v(47.98, -20.08) * mm, v(48.13, -23.8) * mm, v(52.13, -27.06) * mm, v(58.22, -26.02) * mm, v(58.81, -21.71) * mm, v(59.4, -12.8) * mm, v(55.25, -7.02) * mm, v(49.31, -6.57) * mm, v(42.34, -3.6) * mm, v(36.1, 4.56) * mm, v(34.62, 18.21) * mm, v(38.78, 31.72) * mm, v(46.5, 36.17) * mm, v(52.73, 37.8) * mm, v(59.7, 37.5) * mm, v(67.42, 30.53) * mm, v(67.12, 25.33) * mm, v(66.83, 19.84) * mm, v(63.12, 18.8) * mm, v(59.4, 23.1) * mm, v(54.36, 24.44) * mm, v(48.57, 19.84) * mm, v(49.46, 11.38) * mm, v(51.69, 6.78) * mm, v(55.7, 5) * mm, v(61.48, 2.33) * mm, v(65.79, -3.01) * mm, v(67.72, -12.51) * mm, v(69.2, -18.45) * mm, v(69.35, -28.24) * mm, v(66.38, -35.07) * mm, v(63.12, -38.04) * mm, v(54.66, -40.41) * mm, v(44.56, -36.85) * mm, v(37.14, -28.1) * mm, v(37.44, -19.64) * mm, v(42.63, -16.07) * mm, v(45, -16.82) * mm]});
            skFitSpline(sketch, "E1225", {"points": [v(94.88, -40.12) * mm, v(94.58, -35.52) * mm, v(94.88, -28.24) * mm, v(94.43, 6.04) * mm, v(93.4, 20.29) * mm, v(91.61, 22.51) * mm, v(87.16, 24.44) * mm, v(81.82, 26.82) * mm, v(81.52, 32.16) * mm, v(86.27, 34.39) * mm, v(92.65, 36.91) * mm, v(103.63, 35.72) * mm, v(113.58, 34.54) * mm, v(116.25, 30.08) * mm, v(115.2, 26.23) * mm, v(111.65, 24.6) * mm, v(105.86, 22.51) * mm, v(104.52, 9.12) * mm, v(104.97, -19.04) * mm, v(105.41, -35.37) * mm, v(104.97, -40.86) * mm, v(99.03, -42.64) * mm, v(94.88, -40.12) * mm]});
            skFitSpline(sketch, "E1226", {"points": [v(130.94, -31.21) * mm, v(131.68, 8.86) * mm, v(129.16, 18.21) * mm, v(130.05, 22.96) * mm, v(132.43, 32.9) * mm, v(140.59, 38.54) * mm, v(147.12, 37.36) * mm, v(152.61, 37.65) * mm, v(158.25, 35.58) * mm, v(161.07, 30.53) * mm, v(154.84, 25.78) * mm, v(148.16, 26.37) * mm, v(142.67, 25.63) * mm, v(142.07, 21.77) * mm, v(141.48, 8.86) * mm, v(144.3, 5) * mm, v(152.16, 4.56) * mm, v(159.14, 2.78) * mm, v(159.44, -2.86) * mm, v(157.8, -7.32) * mm, v(152.16, -8.8) * mm, v(144.3, -9.7) * mm, v(142.22, -13.25) * mm, v(142.96, -17.56) * mm, v(142.96, -29.28) * mm, v(146.53, -29.58) * mm, v(163.6, -30.91) * mm, v(166.26, -36.85) * mm, v(162.4, -41.3) * mm, v(151.13, -41.3) * mm, v(135.54, -41.45) * mm, v(132.13, -36.7) * mm, v(130.94, -31.21) * mm]});
            skFitSpline(sketch, "E1227", {"points": [v(182.5, -35.84) * mm, v(183.32, -17.2) * mm, v(182.34, 4.38) * mm, v(182.18, 21.55) * mm, v(183.65, 28.74) * mm, v(183.65, 33.48) * mm, v(187.08, 34.63) * mm, v(195.1, 37.9) * mm, v(202.61, 36.1) * mm, v(209.97, 34.14) * mm, v(214.55, 29.07) * mm, v(216.35, 19.26) * mm, v(215.53, 2.75) * mm, v(212.26, -7.06) * mm, v(211.93, -12.95) * mm, v(215.37, -19.82) * mm, v(217.33, -29.3) * mm, v(218.8, -36.33) * mm, v(214.88, -43.85) * mm, v(210.46, -44.83) * mm, v(204.9, -42.05) * mm, v(203.76, -36) * mm, v(201.96, -28) * mm, v(200.98, -17.04) * mm, v(197.38, -9.52) * mm, v(193.95, -8.7) * mm, v(193.3, -12.3) * mm, v(194.28, -25.7) * mm, v(195.1, -31.26) * mm, v(193.13, -40.74) * mm, v(186.27, -43.36) * mm, v(183.81, -39.44) * mm, v(182.5, -35.84) * mm]});
            skFitSpline(sketch, "E1228", {"points": [v(193.13, 15.5) * mm, v(194.11, 24.49) * mm, v(198.53, 26.29) * mm, v(204.9, 24.6) * mm, v(206.05, 18.28) * mm, v(207.36, 9.12) * mm, v(205.4, 3.73) * mm, v(200.65, 0) * mm, v(193.3, 0) * mm, v(193.13, 5.69) * mm, v(193.13, 15.5) * mm]});
            skFitSpline(sketch, "E1229", {"points": [v(234.99, 24.6) * mm, v(241.04, 32.34) * mm, v(245.94, 36.59) * mm, v(252.97, 37.57) * mm, v(262.62, 34.63) * mm, v(266.87, 31.03) * mm, v(267.52, 26.29) * mm, v(265.56, 18.6) * mm, v(262.78, 17.62) * mm, v(258.04, 20.4) * mm, v(253.79, 24.6) * mm, v(247.9, 21.87) * mm, v(247.25, 15.66) * mm, v(248.07, 9.12) * mm, v(251.17, 5.52) * mm, v(254.93, 2.42) * mm, v(262.13, 0) * mm, v(266.38, -6.57) * mm, v(268.83, -18.67) * mm, v(269.97, -30.28) * mm, v(267.68, -36.66) * mm, v(259.84, -42.7) * mm, v(245.45, -41.89) * mm, v(238.75, -37.47) * mm, v(234.33, -30.28) * mm, v(234.82, -22.76) * mm, v(238.1, -19.65) * mm, v(244.3, -20.8) * mm, v(246.76, -23.09) * mm, v(248.07, -28.15) * mm, v(252.15, -30.44) * mm, v(257.71, -30.28) * mm, v(258.2, -25.38) * mm, v(258.86, -17.2) * mm, v(255.91, -9.19) * mm, v(250.03, -8.86) * mm, v(244.8, -6.74) * mm, v(235.64, 0) * mm, v(233.84, 12.88) * mm, v(234.99, 24.6) * mm]});
            skLineSegment(sketch, "E1230.bottom", {"start": v(304.8, -76.2) * mm, "end": v(-304.8, -76.2) * mm, "construction": true});
            skLineSegment(sketch, "E1230.top", {"start": v(304.8, 76.2) * mm, "end": v(-304.8, 76.2) * mm, "construction": true});
            skLineSegment(sketch, "E1230.left", {"start": v(304.8, -76.2) * mm, "end": v(304.8, 76.2) * mm, "construction": true});
            skLineSegment(sketch, "E1230.right", {"start": v(-304.8, -76.2) * mm, "end": v(-304.8, 76.2) * mm, "construction": true});
            skPoint(sketch, "E1230.middle", {"position": v(0, 0) * mm});
            skSolve(sketch);
        }
        {
            var Q0;
            Q0 = qSketchRegion(id + "F1", true);
            extrude(context, id + "F2", {"entities" : qUnion([Q0]), "depth" : 25.4 * mm, "offsetDistance" : 25.4 * mm});
        }
    });
